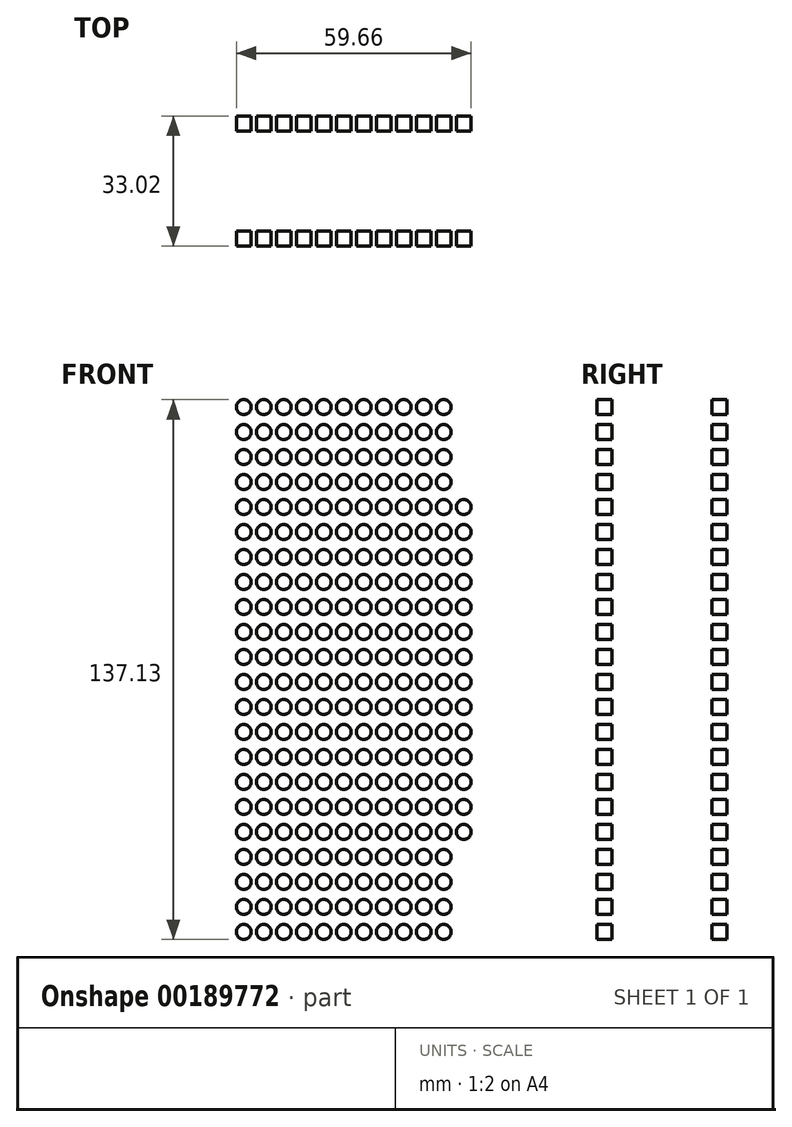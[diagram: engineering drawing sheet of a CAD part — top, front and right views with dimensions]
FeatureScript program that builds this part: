
annotation { "Feature Type Name" : "Feature", "Feature Type Description" : "" }
export const myFeature = defineFeature(function(context is Context, id is Id, definition is map)
    precondition{}
    {
        {
            var Q0;
            Q0=qCreatedBy(makeId("Front.planeOp"),FACE);
            var sketch = newSketch(context, id + "F0", { "sketchPlane" : qUnion([Q0])});
            skLineSegment(sketch, "E0.bottom", {"start": v(-63.5, 0) * mm, "end": v(63.5, 0) * mm});
            skLineSegment(sketch, "E0.top", {"start": v(-63.5, 152.4) * mm, "end": v(63.5, 152.4) * mm});
            skLineSegment(sketch, "E0.left", {"start": v(-63.5, 0) * mm, "end": v(-63.5, 152.4) * mm});
            skLineSegment(sketch, "E0.right", {"start": v(63.5, 0) * mm, "end": v(63.5, 152.4) * mm});
            skSolve(sketch);
        }
        {
            var Q0;
            Q0=makeQuery(id+"F0.imprint","IMPRINT",FACE,{"disambiguationData":[TD([[makeQuery(id+"F0.imprint","IMPRINT",EDGE,{"derivedFrom":sQuery(id+"F0.wireOp",EDGE,"E0.bottom")}),1.0]])]});
            extrude(context, id + "F1", {"entities" : qUnion([Q0]), "depth" : 33.02 * mm});
        }
        {
            var Q0;
            Q0=makeQuery(id+"F1.opExtrude","SWEPT_FACE",FACE,{"disambiguationData":[OSD([sQuery(id+"F0.wireOp",EDGE,"E0.top")])]});
            var sketch = newSketch(context, id + "F2", { "sketchPlane" : qUnion([Q0])});
            skLineSegment(sketch, "E1.bottom", {"start": v(-59.7, -3.81) * mm, "end": v(59.69, -3.81) * mm});
            skLineSegment(sketch, "E1.top", {"start": v(-59.7, -29.21) * mm, "end": v(59.69, -29.21) * mm});
            skLineSegment(sketch, "E1.left", {"start": v(-59.7, -3.81) * mm, "end": v(-59.7, -29.21) * mm});
            skLineSegment(sketch, "E1.right", {"start": v(59.69, -3.81) * mm, "end": v(59.69, -29.21) * mm});
            skSolve(sketch);
        }
        {
            var Q0;
            Q0=makeQuery(id+"F2.imprint","IMPRINT",FACE,{"disambiguationData":[TD([[makeQuery(id+"F2.imprint","IMPRINT",EDGE,{"derivedFrom":sQuery(id+"F2.wireOp",EDGE,"E1.bottom")}),-1.0]])]});
            extrude(context, id + "F3", {"entities" : qUnion([Q0]), "operationType" : NewBodyOperationType.REMOVE, "oppositeDirection" : true, "depth" : 147.32 * mm});
        }
        {
            var Q0;
            Q0=makeQuery(id+"F1.opExtrude","CAP_FACE",FACE,{"disambiguationData":[OSD([sQuery(id+"F0.wireOp",EDGE,"E0.bottom"),sQuery(id+"F0.wireOp",EDGE,"E0.top"),sQuery(id+"F0.wireOp",EDGE,"E0.left"),sQuery(id+"F0.wireOp",EDGE,"E0.right")])],"isStart":false});
            var sketch = newSketch(context, id + "F4", { "sketchPlane" : qUnion([Q0])});
            skCircle(sketch, "E2", {"center": v(0, 7.62) * mm, "radius": 1.89 * mm});
            skCircle(sketch, "E3.0.1.0", {"center": v(0, 13.97) * mm, "radius": 1.89 * mm});
            skCircle(sketch, "E3.0.2.0", {"center": v(0, 20.32) * mm, "radius": 1.89 * mm});
            skCircle(sketch, "E3.0.3.0", {"center": v(0, 26.67) * mm, "radius": 1.89 * mm});
            skCircle(sketch, "E3.0.4.0", {"center": v(0, 33.02) * mm, "radius": 1.89 * mm});
            skCircle(sketch, "E3.0.5.0", {"center": v(0, 39.37) * mm, "radius": 1.89 * mm});
            skCircle(sketch, "E3.0.6.0", {"center": v(0, 45.72) * mm, "radius": 1.89 * mm});
            skCircle(sketch, "E3.0.7.0", {"center": v(0, 52.07) * mm, "radius": 1.89 * mm});
            skCircle(sketch, "E3.0.8.0", {"center": v(0, 58.42) * mm, "radius": 1.89 * mm});
            skCircle(sketch, "E3.0.9.0", {"center": v(0, 64.77) * mm, "radius": 1.89 * mm});
            skCircle(sketch, "E3.0.10.0", {"center": v(0, 71.12) * mm, "radius": 1.89 * mm});
            skCircle(sketch, "E3.0.11.0", {"center": v(0, 77.47) * mm, "radius": 1.89 * mm});
            skCircle(sketch, "E3.0.12.0", {"center": v(0, 83.82) * mm, "radius": 1.89 * mm});
            skCircle(sketch, "E3.0.13.0", {"center": v(0, 90.17) * mm, "radius": 1.89 * mm});
            skCircle(sketch, "E3.0.14.0", {"center": v(0, 96.52) * mm, "radius": 1.89 * mm});
            skCircle(sketch, "E3.0.15.0", {"center": v(0, 102.87) * mm, "radius": 1.89 * mm});
            skCircle(sketch, "E3.0.16.0", {"center": v(0, 109.22) * mm, "radius": 1.89 * mm});
            skCircle(sketch, "E3.0.17.0", {"center": v(0, 115.57) * mm, "radius": 1.89 * mm});
            skCircle(sketch, "E3.1.0.0", {"center": v(5.08, 7.62) * mm, "radius": 1.89 * mm});
            skCircle(sketch, "E3.1.1.0", {"center": v(5.08, 13.97) * mm, "radius": 1.89 * mm});
            skCircle(sketch, "E3.1.2.0", {"center": v(5.08, 20.32) * mm, "radius": 1.89 * mm});
            skCircle(sketch, "E3.1.3.0", {"center": v(5.08, 26.67) * mm, "radius": 1.89 * mm});
            skCircle(sketch, "E3.1.4.0", {"center": v(5.08, 33.02) * mm, "radius": 1.89 * mm});
            skCircle(sketch, "E3.1.5.0", {"center": v(5.08, 39.37) * mm, "radius": 1.89 * mm});
            skCircle(sketch, "E3.1.6.0", {"center": v(5.08, 45.72) * mm, "radius": 1.89 * mm});
            skCircle(sketch, "E3.1.7.0", {"center": v(5.08, 52.07) * mm, "radius": 1.89 * mm});
            skCircle(sketch, "E3.1.8.0", {"center": v(5.08, 58.42) * mm, "radius": 1.89 * mm});
            skCircle(sketch, "E3.1.9.0", {"center": v(5.08, 64.77) * mm, "radius": 1.89 * mm});
            skCircle(sketch, "E3.1.10.0", {"center": v(5.08, 71.12) * mm, "radius": 1.89 * mm});
            skCircle(sketch, "E3.1.11.0", {"center": v(5.08, 77.47) * mm, "radius": 1.89 * mm});
            skCircle(sketch, "E3.1.12.0", {"center": v(5.08, 83.82) * mm, "radius": 1.89 * mm});
            skCircle(sketch, "E3.1.13.0", {"center": v(5.08, 90.17) * mm, "radius": 1.89 * mm});
            skCircle(sketch, "E3.1.14.0", {"center": v(5.08, 96.52) * mm, "radius": 1.89 * mm});
            skCircle(sketch, "E3.1.15.0", {"center": v(5.08, 102.87) * mm, "radius": 1.89 * mm});
            skCircle(sketch, "E3.1.16.0", {"center": v(5.08, 109.22) * mm, "radius": 1.89 * mm});
            skCircle(sketch, "E3.1.17.0", {"center": v(5.08, 115.57) * mm, "radius": 1.89 * mm});
            skCircle(sketch, "E3.2.0.0", {"center": v(10.16, 7.62) * mm, "radius": 1.89 * mm});
            skCircle(sketch, "E3.2.1.0", {"center": v(10.16, 13.97) * mm, "radius": 1.89 * mm});
            skCircle(sketch, "E3.2.2.0", {"center": v(10.16, 20.32) * mm, "radius": 1.89 * mm});
            skCircle(sketch, "E3.2.3.0", {"center": v(10.16, 26.67) * mm, "radius": 1.89 * mm});
            skCircle(sketch, "E3.2.4.0", {"center": v(10.16, 33.02) * mm, "radius": 1.89 * mm});
            skCircle(sketch, "E3.2.5.0", {"center": v(10.16, 39.37) * mm, "radius": 1.89 * mm});
            skCircle(sketch, "E3.2.6.0", {"center": v(10.16, 45.72) * mm, "radius": 1.89 * mm});
            skCircle(sketch, "E3.2.7.0", {"center": v(10.16, 52.07) * mm, "radius": 1.89 * mm});
            skCircle(sketch, "E3.2.8.0", {"center": v(10.16, 58.42) * mm, "radius": 1.89 * mm});
            skCircle(sketch, "E3.2.9.0", {"center": v(10.16, 64.77) * mm, "radius": 1.89 * mm});
            skCircle(sketch, "E3.2.10.0", {"center": v(10.16, 71.12) * mm, "radius": 1.89 * mm});
            skCircle(sketch, "E3.2.11.0", {"center": v(10.16, 77.47) * mm, "radius": 1.89 * mm});
            skCircle(sketch, "E3.2.12.0", {"center": v(10.16, 83.82) * mm, "radius": 1.89 * mm});
            skCircle(sketch, "E3.2.13.0", {"center": v(10.16, 90.17) * mm, "radius": 1.89 * mm});
            skCircle(sketch, "E3.2.14.0", {"center": v(10.16, 96.52) * mm, "radius": 1.89 * mm});
            skCircle(sketch, "E3.2.15.0", {"center": v(10.16, 102.87) * mm, "radius": 1.89 * mm});
            skCircle(sketch, "E3.2.16.0", {"center": v(10.16, 109.22) * mm, "radius": 1.89 * mm});
            skCircle(sketch, "E3.2.17.0", {"center": v(10.16, 115.57) * mm, "radius": 1.89 * mm});
            skCircle(sketch, "E3.3.0.0", {"center": v(15.24, 7.62) * mm, "radius": 1.89 * mm});
            skCircle(sketch, "E3.3.1.0", {"center": v(15.24, 13.97) * mm, "radius": 1.89 * mm});
            skCircle(sketch, "E3.3.2.0", {"center": v(15.24, 20.32) * mm, "radius": 1.89 * mm});
            skCircle(sketch, "E3.3.3.0", {"center": v(15.24, 26.67) * mm, "radius": 1.89 * mm});
            skCircle(sketch, "E3.3.4.0", {"center": v(15.24, 33.02) * mm, "radius": 1.89 * mm});
            skCircle(sketch, "E3.3.5.0", {"center": v(15.24, 39.37) * mm, "radius": 1.89 * mm});
            skCircle(sketch, "E3.3.6.0", {"center": v(15.24, 45.72) * mm, "radius": 1.89 * mm});
            skCircle(sketch, "E3.3.7.0", {"center": v(15.24, 52.07) * mm, "radius": 1.89 * mm});
            skCircle(sketch, "E3.3.8.0", {"center": v(15.24, 58.42) * mm, "radius": 1.89 * mm});
            skCircle(sketch, "E3.3.9.0", {"center": v(15.24, 64.77) * mm, "radius": 1.89 * mm});
            skCircle(sketch, "E3.3.10.0", {"center": v(15.24, 71.12) * mm, "radius": 1.89 * mm});
            skCircle(sketch, "E3.3.11.0", {"center": v(15.24, 77.47) * mm, "radius": 1.89 * mm});
            skCircle(sketch, "E3.3.12.0", {"center": v(15.24, 83.82) * mm, "radius": 1.89 * mm});
            skCircle(sketch, "E3.3.13.0", {"center": v(15.24, 90.17) * mm, "radius": 1.89 * mm});
            skCircle(sketch, "E3.3.14.0", {"center": v(15.24, 96.52) * mm, "radius": 1.89 * mm});
            skCircle(sketch, "E3.3.15.0", {"center": v(15.24, 102.87) * mm, "radius": 1.89 * mm});
            skCircle(sketch, "E3.3.16.0", {"center": v(15.24, 109.22) * mm, "radius": 1.89 * mm});
            skCircle(sketch, "E3.3.17.0", {"center": v(15.24, 115.57) * mm, "radius": 1.89 * mm});
            skCircle(sketch, "E3.4.0.0", {"center": v(20.32, 7.62) * mm, "radius": 1.89 * mm});
            skCircle(sketch, "E3.4.1.0", {"center": v(20.32, 13.97) * mm, "radius": 1.89 * mm});
            skCircle(sketch, "E3.4.2.0", {"center": v(20.32, 20.32) * mm, "radius": 1.89 * mm});
            skCircle(sketch, "E3.4.3.0", {"center": v(20.32, 26.67) * mm, "radius": 1.89 * mm});
            skCircle(sketch, "E3.4.4.0", {"center": v(20.32, 33.02) * mm, "radius": 1.89 * mm});
            skCircle(sketch, "E3.4.5.0", {"center": v(20.32, 39.37) * mm, "radius": 1.89 * mm});
            skCircle(sketch, "E3.4.6.0", {"center": v(20.32, 45.72) * mm, "radius": 1.89 * mm});
            skCircle(sketch, "E3.4.7.0", {"center": v(20.32, 52.07) * mm, "radius": 1.89 * mm});
            skCircle(sketch, "E3.4.8.0", {"center": v(20.32, 58.42) * mm, "radius": 1.89 * mm});
            skCircle(sketch, "E3.4.9.0", {"center": v(20.32, 64.77) * mm, "radius": 1.89 * mm});
            skCircle(sketch, "E3.4.10.0", {"center": v(20.32, 71.12) * mm, "radius": 1.89 * mm});
            skCircle(sketch, "E3.4.11.0", {"center": v(20.32, 77.47) * mm, "radius": 1.89 * mm});
            skCircle(sketch, "E3.4.12.0", {"center": v(20.32, 83.82) * mm, "radius": 1.89 * mm});
            skCircle(sketch, "E3.4.13.0", {"center": v(20.32, 90.17) * mm, "radius": 1.89 * mm});
            skCircle(sketch, "E3.4.14.0", {"center": v(20.32, 96.52) * mm, "radius": 1.89 * mm});
            skCircle(sketch, "E3.4.15.0", {"center": v(20.32, 102.87) * mm, "radius": 1.89 * mm});
            skCircle(sketch, "E3.4.16.0", {"center": v(20.32, 109.22) * mm, "radius": 1.89 * mm});
            skCircle(sketch, "E3.4.17.0", {"center": v(20.32, 115.57) * mm, "radius": 1.89 * mm});
            skCircle(sketch, "E3.5.0.0", {"center": v(25.4, 7.62) * mm, "radius": 1.89 * mm});
            skCircle(sketch, "E3.5.1.0", {"center": v(25.4, 13.97) * mm, "radius": 1.89 * mm});
            skCircle(sketch, "E3.5.2.0", {"center": v(25.4, 20.32) * mm, "radius": 1.89 * mm});
            skCircle(sketch, "E3.5.3.0", {"center": v(25.4, 26.67) * mm, "radius": 1.89 * mm});
            skCircle(sketch, "E3.5.4.0", {"center": v(25.4, 33.02) * mm, "radius": 1.89 * mm});
            skCircle(sketch, "E3.5.5.0", {"center": v(25.4, 39.37) * mm, "radius": 1.89 * mm});
            skCircle(sketch, "E3.5.6.0", {"center": v(25.4, 45.72) * mm, "radius": 1.89 * mm});
            skCircle(sketch, "E3.5.7.0", {"center": v(25.4, 52.07) * mm, "radius": 1.89 * mm});
            skCircle(sketch, "E3.5.8.0", {"center": v(25.4, 58.42) * mm, "radius": 1.89 * mm});
            skCircle(sketch, "E3.5.9.0", {"center": v(25.4, 64.77) * mm, "radius": 1.89 * mm});
            skCircle(sketch, "E3.5.10.0", {"center": v(25.4, 71.12) * mm, "radius": 1.89 * mm});
            skCircle(sketch, "E3.5.11.0", {"center": v(25.4, 77.47) * mm, "radius": 1.89 * mm});
            skCircle(sketch, "E3.5.12.0", {"center": v(25.4, 83.82) * mm, "radius": 1.89 * mm});
            skCircle(sketch, "E3.5.13.0", {"center": v(25.4, 90.17) * mm, "radius": 1.89 * mm});
            skCircle(sketch, "E3.5.14.0", {"center": v(25.4, 96.52) * mm, "radius": 1.89 * mm});
            skCircle(sketch, "E3.5.15.0", {"center": v(25.4, 102.87) * mm, "radius": 1.89 * mm});
            skCircle(sketch, "E3.5.16.0", {"center": v(25.4, 109.22) * mm, "radius": 1.89 * mm});
            skCircle(sketch, "E3.5.17.0", {"center": v(25.4, 115.57) * mm, "radius": 1.89 * mm});
            skCircle(sketch, "E3.6.0.0", {"center": v(30.48, 7.62) * mm, "radius": 1.89 * mm});
            skCircle(sketch, "E3.6.1.0", {"center": v(30.48, 13.97) * mm, "radius": 1.89 * mm});
            skCircle(sketch, "E3.6.2.0", {"center": v(30.48, 20.32) * mm, "radius": 1.89 * mm});
            skCircle(sketch, "E3.6.3.0", {"center": v(30.48, 26.67) * mm, "radius": 1.89 * mm});
            skCircle(sketch, "E3.6.4.0", {"center": v(30.48, 33.02) * mm, "radius": 1.89 * mm});
            skCircle(sketch, "E3.6.5.0", {"center": v(30.48, 39.37) * mm, "radius": 1.89 * mm});
            skCircle(sketch, "E3.6.6.0", {"center": v(30.48, 45.72) * mm, "radius": 1.89 * mm});
            skCircle(sketch, "E3.6.7.0", {"center": v(30.48, 52.07) * mm, "radius": 1.89 * mm});
            skCircle(sketch, "E3.6.8.0", {"center": v(30.48, 58.42) * mm, "radius": 1.89 * mm});
            skCircle(sketch, "E3.6.9.0", {"center": v(30.48, 64.77) * mm, "radius": 1.89 * mm});
            skCircle(sketch, "E3.6.10.0", {"center": v(30.48, 71.12) * mm, "radius": 1.89 * mm});
            skCircle(sketch, "E3.6.11.0", {"center": v(30.48, 77.47) * mm, "radius": 1.89 * mm});
            skCircle(sketch, "E3.6.12.0", {"center": v(30.48, 83.82) * mm, "radius": 1.89 * mm});
            skCircle(sketch, "E3.6.13.0", {"center": v(30.48, 90.17) * mm, "radius": 1.89 * mm});
            skCircle(sketch, "E3.6.14.0", {"center": v(30.48, 96.52) * mm, "radius": 1.89 * mm});
            skCircle(sketch, "E3.6.15.0", {"center": v(30.48, 102.87) * mm, "radius": 1.89 * mm});
            skCircle(sketch, "E3.6.16.0", {"center": v(30.48, 109.22) * mm, "radius": 1.89 * mm});
            skCircle(sketch, "E3.6.17.0", {"center": v(30.48, 115.57) * mm, "radius": 1.89 * mm});
            skCircle(sketch, "E3.7.0.0", {"center": v(35.56, 7.62) * mm, "radius": 1.89 * mm});
            skCircle(sketch, "E3.7.1.0", {"center": v(35.56, 13.97) * mm, "radius": 1.89 * mm});
            skCircle(sketch, "E3.7.2.0", {"center": v(35.56, 20.32) * mm, "radius": 1.89 * mm});
            skCircle(sketch, "E3.7.3.0", {"center": v(35.56, 26.67) * mm, "radius": 1.89 * mm});
            skCircle(sketch, "E3.7.4.0", {"center": v(35.56, 33.02) * mm, "radius": 1.89 * mm});
            skCircle(sketch, "E3.7.5.0", {"center": v(35.56, 39.37) * mm, "radius": 1.89 * mm});
            skCircle(sketch, "E3.7.6.0", {"center": v(35.56, 45.72) * mm, "radius": 1.89 * mm});
            skCircle(sketch, "E3.7.7.0", {"center": v(35.56, 52.07) * mm, "radius": 1.89 * mm});
            skCircle(sketch, "E3.7.8.0", {"center": v(35.56, 58.42) * mm, "radius": 1.89 * mm});
            skCircle(sketch, "E3.7.9.0", {"center": v(35.56, 64.77) * mm, "radius": 1.89 * mm});
            skCircle(sketch, "E3.7.10.0", {"center": v(35.56, 71.12) * mm, "radius": 1.89 * mm});
            skCircle(sketch, "E3.7.11.0", {"center": v(35.56, 77.47) * mm, "radius": 1.89 * mm});
            skCircle(sketch, "E3.7.12.0", {"center": v(35.56, 83.82) * mm, "radius": 1.89 * mm});
            skCircle(sketch, "E3.7.13.0", {"center": v(35.56, 90.17) * mm, "radius": 1.89 * mm});
            skCircle(sketch, "E3.7.14.0", {"center": v(35.56, 96.52) * mm, "radius": 1.89 * mm});
            skCircle(sketch, "E3.7.15.0", {"center": v(35.56, 102.87) * mm, "radius": 1.89 * mm});
            skCircle(sketch, "E3.7.16.0", {"center": v(35.56, 109.22) * mm, "radius": 1.89 * mm});
            skCircle(sketch, "E3.7.17.0", {"center": v(35.56, 115.57) * mm, "radius": 1.89 * mm});
            skLineSegment(sketch, "E3.direction1", {"start": v(0, 7.62) * mm, "end": v(5.08, 7.62) * mm, "construction": true});
            skLineSegment(sketch, "E3.direction2", {"start": v(0, 7.62) * mm, "end": v(0, 13.97) * mm, "construction": true});
            skLineSegment(sketch, "E4.MirrorCS", {"start": v(0, 7.62) * mm, "end": v(-5.08, 7.62) * mm, "construction": true});
            skCircle(sketch, "E5.0.8.0", {"center": v(40.64, 7.62) * mm, "radius": 1.89 * mm});
            skCircle(sketch, "E5.0.8.1", {"center": v(40.64, 13.97) * mm, "radius": 1.89 * mm});
            skCircle(sketch, "E5.0.8.2", {"center": v(40.64, 20.32) * mm, "radius": 1.89 * mm});
            skCircle(sketch, "E5.0.8.3", {"center": v(40.64, 26.67) * mm, "radius": 1.89 * mm});
            skCircle(sketch, "E5.0.8.4", {"center": v(40.64, 33.02) * mm, "radius": 1.89 * mm});
            skCircle(sketch, "E5.0.8.5", {"center": v(40.64, 39.37) * mm, "radius": 1.89 * mm});
            skCircle(sketch, "E5.0.8.6", {"center": v(40.64, 45.72) * mm, "radius": 1.89 * mm});
            skCircle(sketch, "E5.0.8.7", {"center": v(40.64, 52.07) * mm, "radius": 1.89 * mm});
            skCircle(sketch, "E5.0.8.8", {"center": v(40.64, 58.42) * mm, "radius": 1.89 * mm});
            skCircle(sketch, "E5.0.8.9", {"center": v(40.64, 64.77) * mm, "radius": 1.89 * mm});
            skCircle(sketch, "E5.0.8.10", {"center": v(40.64, 71.12) * mm, "radius": 1.89 * mm});
            skCircle(sketch, "E5.0.8.11", {"center": v(40.64, 77.47) * mm, "radius": 1.89 * mm});
            skCircle(sketch, "E5.0.8.12", {"center": v(40.64, 83.82) * mm, "radius": 1.89 * mm});
            skCircle(sketch, "E5.0.8.13", {"center": v(40.64, 90.17) * mm, "radius": 1.89 * mm});
            skCircle(sketch, "E5.0.8.14", {"center": v(40.64, 96.52) * mm, "radius": 1.89 * mm});
            skCircle(sketch, "E5.0.8.15", {"center": v(40.64, 102.87) * mm, "radius": 1.89 * mm});
            skCircle(sketch, "E5.0.8.16", {"center": v(40.64, 109.22) * mm, "radius": 1.89 * mm});
            skCircle(sketch, "E5.0.8.17", {"center": v(40.64, 115.57) * mm, "radius": 1.89 * mm});
            skCircle(sketch, "E5.0.9.0", {"center": v(45.72, 7.62) * mm, "radius": 1.89 * mm});
            skCircle(sketch, "E5.0.9.1", {"center": v(45.72, 13.97) * mm, "radius": 1.89 * mm});
            skCircle(sketch, "E5.0.9.2", {"center": v(45.72, 20.32) * mm, "radius": 1.89 * mm});
            skCircle(sketch, "E5.0.9.3", {"center": v(45.72, 26.67) * mm, "radius": 1.89 * mm});
            skCircle(sketch, "E5.0.9.4", {"center": v(45.72, 33.02) * mm, "radius": 1.89 * mm});
            skCircle(sketch, "E5.0.9.5", {"center": v(45.72, 39.37) * mm, "radius": 1.89 * mm});
            skCircle(sketch, "E5.0.9.6", {"center": v(45.72, 45.72) * mm, "radius": 1.89 * mm});
            skCircle(sketch, "E5.0.9.7", {"center": v(45.72, 52.07) * mm, "radius": 1.89 * mm});
            skCircle(sketch, "E5.0.9.8", {"center": v(45.72, 58.42) * mm, "radius": 1.89 * mm});
            skCircle(sketch, "E5.0.9.9", {"center": v(45.72, 64.77) * mm, "radius": 1.89 * mm});
            skCircle(sketch, "E5.0.9.10", {"center": v(45.72, 71.12) * mm, "radius": 1.89 * mm});
            skCircle(sketch, "E5.0.9.11", {"center": v(45.72, 77.47) * mm, "radius": 1.89 * mm});
            skCircle(sketch, "E5.0.9.12", {"center": v(45.72, 83.82) * mm, "radius": 1.89 * mm});
            skCircle(sketch, "E5.0.9.13", {"center": v(45.72, 90.17) * mm, "radius": 1.89 * mm});
            skCircle(sketch, "E5.0.9.14", {"center": v(45.72, 96.52) * mm, "radius": 1.89 * mm});
            skCircle(sketch, "E5.0.9.15", {"center": v(45.72, 102.87) * mm, "radius": 1.89 * mm});
            skCircle(sketch, "E5.0.9.16", {"center": v(45.72, 109.22) * mm, "radius": 1.89 * mm});
            skCircle(sketch, "E5.0.9.17", {"center": v(45.72, 115.57) * mm, "radius": 1.89 * mm});
            skCircle(sketch, "E5.0.10.0", {"center": v(50.8, 7.62) * mm, "radius": 1.89 * mm});
            skCircle(sketch, "E5.0.10.1", {"center": v(50.8, 13.97) * mm, "radius": 1.89 * mm});
            skCircle(sketch, "E5.0.10.2", {"center": v(50.8, 20.32) * mm, "radius": 1.89 * mm});
            skCircle(sketch, "E5.0.10.3", {"center": v(50.8, 26.67) * mm, "radius": 1.89 * mm});
            skCircle(sketch, "E5.0.10.4", {"center": v(50.8, 33.02) * mm, "radius": 1.89 * mm});
            skCircle(sketch, "E5.0.10.5", {"center": v(50.8, 39.37) * mm, "radius": 1.89 * mm});
            skCircle(sketch, "E5.0.10.6", {"center": v(50.8, 45.72) * mm, "radius": 1.89 * mm});
            skCircle(sketch, "E5.0.10.7", {"center": v(50.8, 52.07) * mm, "radius": 1.89 * mm});
            skCircle(sketch, "E5.0.10.8", {"center": v(50.8, 58.42) * mm, "radius": 1.89 * mm});
            skCircle(sketch, "E5.0.10.9", {"center": v(50.8, 64.77) * mm, "radius": 1.89 * mm});
            skCircle(sketch, "E5.0.10.10", {"center": v(50.8, 71.12) * mm, "radius": 1.89 * mm});
            skCircle(sketch, "E5.0.10.11", {"center": v(50.8, 77.47) * mm, "radius": 1.89 * mm});
            skCircle(sketch, "E5.0.10.12", {"center": v(50.8, 83.82) * mm, "radius": 1.89 * mm});
            skCircle(sketch, "E5.0.10.13", {"center": v(50.8, 90.17) * mm, "radius": 1.89 * mm});
            skCircle(sketch, "E5.0.10.14", {"center": v(50.8, 96.52) * mm, "radius": 1.89 * mm});
            skCircle(sketch, "E5.0.10.15", {"center": v(50.8, 102.87) * mm, "radius": 1.89 * mm});
            skCircle(sketch, "E5.0.10.16", {"center": v(50.8, 109.22) * mm, "radius": 1.89 * mm});
            skCircle(sketch, "E5.0.10.17", {"center": v(50.8, 115.57) * mm, "radius": 1.89 * mm});
            skCircle(sketch, "E5.0.11.0", {"center": v(55.88, 7.62) * mm, "radius": 1.89 * mm});
            skCircle(sketch, "E5.0.11.1", {"center": v(55.88, 13.97) * mm, "radius": 1.89 * mm});
            skCircle(sketch, "E5.0.11.2", {"center": v(55.88, 20.32) * mm, "radius": 1.89 * mm});
            skCircle(sketch, "E5.0.11.3", {"center": v(55.88, 26.67) * mm, "radius": 1.89 * mm});
            skCircle(sketch, "E5.0.11.4", {"center": v(55.88, 33.02) * mm, "radius": 1.89 * mm});
            skCircle(sketch, "E5.0.11.5", {"center": v(55.88, 39.37) * mm, "radius": 1.89 * mm});
            skCircle(sketch, "E5.0.11.6", {"center": v(55.88, 45.72) * mm, "radius": 1.89 * mm});
            skCircle(sketch, "E5.0.11.7", {"center": v(55.88, 52.07) * mm, "radius": 1.89 * mm});
            skCircle(sketch, "E5.0.11.8", {"center": v(55.88, 58.42) * mm, "radius": 1.89 * mm});
            skCircle(sketch, "E5.0.11.9", {"center": v(55.88, 64.77) * mm, "radius": 1.89 * mm});
            skCircle(sketch, "E5.0.11.10", {"center": v(55.88, 71.12) * mm, "radius": 1.89 * mm});
            skCircle(sketch, "E5.0.11.11", {"center": v(55.88, 77.47) * mm, "radius": 1.89 * mm});
            skCircle(sketch, "E5.0.11.12", {"center": v(55.88, 83.82) * mm, "radius": 1.89 * mm});
            skCircle(sketch, "E5.0.11.13", {"center": v(55.88, 90.17) * mm, "radius": 1.89 * mm});
            skCircle(sketch, "E5.0.11.14", {"center": v(55.88, 96.52) * mm, "radius": 1.89 * mm});
            skCircle(sketch, "E5.0.11.15", {"center": v(55.88, 102.87) * mm, "radius": 1.89 * mm});
            skCircle(sketch, "E5.0.11.16", {"center": v(55.88, 109.22) * mm, "radius": 1.89 * mm});
            skCircle(sketch, "E5.0.11.17", {"center": v(55.88, 115.57) * mm, "radius": 1.89 * mm});
            skCircle(sketch, "E6.0.0.18", {"center": v(0, 121.92) * mm, "radius": 1.89 * mm});
            skCircle(sketch, "E6.0.0.19", {"center": v(0, 128.27) * mm, "radius": 1.89 * mm});
            skCircle(sketch, "E6.0.0.20", {"center": v(0, 134.62) * mm, "radius": 1.89 * mm});
            skCircle(sketch, "E6.0.0.21", {"center": v(0, 140.97) * mm, "radius": 1.89 * mm});
            skCircle(sketch, "E6.0.1.18", {"center": v(5.08, 121.92) * mm, "radius": 1.89 * mm});
            skCircle(sketch, "E6.0.1.19", {"center": v(5.08, 128.27) * mm, "radius": 1.89 * mm});
            skCircle(sketch, "E6.0.1.20", {"center": v(5.08, 134.62) * mm, "radius": 1.89 * mm});
            skCircle(sketch, "E6.0.1.21", {"center": v(5.08, 140.97) * mm, "radius": 1.89 * mm});
            skCircle(sketch, "E6.0.2.18", {"center": v(10.16, 121.92) * mm, "radius": 1.89 * mm});
            skCircle(sketch, "E6.0.2.19", {"center": v(10.16, 128.27) * mm, "radius": 1.89 * mm});
            skCircle(sketch, "E6.0.2.20", {"center": v(10.16, 134.62) * mm, "radius": 1.89 * mm});
            skCircle(sketch, "E6.0.2.21", {"center": v(10.16, 140.97) * mm, "radius": 1.89 * mm});
            skCircle(sketch, "E6.0.3.18", {"center": v(15.24, 121.92) * mm, "radius": 1.89 * mm});
            skCircle(sketch, "E6.0.3.19", {"center": v(15.24, 128.27) * mm, "radius": 1.89 * mm});
            skCircle(sketch, "E6.0.3.20", {"center": v(15.24, 134.62) * mm, "radius": 1.89 * mm});
            skCircle(sketch, "E6.0.3.21", {"center": v(15.24, 140.97) * mm, "radius": 1.89 * mm});
            skCircle(sketch, "E6.0.4.18", {"center": v(20.32, 121.92) * mm, "radius": 1.89 * mm});
            skCircle(sketch, "E6.0.4.19", {"center": v(20.32, 128.27) * mm, "radius": 1.89 * mm});
            skCircle(sketch, "E6.0.4.20", {"center": v(20.32, 134.62) * mm, "radius": 1.89 * mm});
            skCircle(sketch, "E6.0.4.21", {"center": v(20.32, 140.97) * mm, "radius": 1.89 * mm});
            skCircle(sketch, "E6.0.5.18", {"center": v(25.4, 121.92) * mm, "radius": 1.89 * mm});
            skCircle(sketch, "E6.0.5.19", {"center": v(25.4, 128.27) * mm, "radius": 1.89 * mm});
            skCircle(sketch, "E6.0.5.20", {"center": v(25.4, 134.62) * mm, "radius": 1.89 * mm});
            skCircle(sketch, "E6.0.5.21", {"center": v(25.4, 140.97) * mm, "radius": 1.89 * mm});
            skCircle(sketch, "E6.0.6.18", {"center": v(30.48, 121.92) * mm, "radius": 1.89 * mm});
            skCircle(sketch, "E6.0.6.19", {"center": v(30.48, 128.27) * mm, "radius": 1.89 * mm});
            skCircle(sketch, "E6.0.6.20", {"center": v(30.48, 134.62) * mm, "radius": 1.89 * mm});
            skCircle(sketch, "E6.0.6.21", {"center": v(30.48, 140.97) * mm, "radius": 1.89 * mm});
            skCircle(sketch, "E6.0.7.18", {"center": v(35.56, 121.92) * mm, "radius": 1.89 * mm});
            skCircle(sketch, "E6.0.7.19", {"center": v(35.56, 128.27) * mm, "radius": 1.89 * mm});
            skCircle(sketch, "E6.0.7.20", {"center": v(35.56, 134.62) * mm, "radius": 1.89 * mm});
            skCircle(sketch, "E6.0.7.21", {"center": v(35.56, 140.97) * mm, "radius": 1.89 * mm});
            skCircle(sketch, "E6.0.8.18", {"center": v(40.64, 121.92) * mm, "radius": 1.89 * mm});
            skCircle(sketch, "E6.0.8.19", {"center": v(40.64, 128.27) * mm, "radius": 1.89 * mm});
            skCircle(sketch, "E6.0.8.20", {"center": v(40.64, 134.62) * mm, "radius": 1.89 * mm});
            skCircle(sketch, "E6.0.8.21", {"center": v(40.64, 140.97) * mm, "radius": 1.89 * mm});
            skCircle(sketch, "E6.0.9.18", {"center": v(45.72, 121.92) * mm, "radius": 1.89 * mm});
            skCircle(sketch, "E6.0.9.19", {"center": v(45.72, 128.27) * mm, "radius": 1.89 * mm});
            skCircle(sketch, "E6.0.9.20", {"center": v(45.72, 134.62) * mm, "radius": 1.89 * mm});
            skCircle(sketch, "E6.0.9.21", {"center": v(45.72, 140.97) * mm, "radius": 1.89 * mm});
            skCircle(sketch, "E6.0.10.18", {"center": v(50.8, 121.92) * mm, "radius": 1.89 * mm});
            skCircle(sketch, "E6.0.10.19", {"center": v(50.8, 128.27) * mm, "radius": 1.89 * mm});
            skCircle(sketch, "E6.0.10.20", {"center": v(50.8, 134.62) * mm, "radius": 1.89 * mm});
            skCircle(sketch, "E6.0.10.21", {"center": v(50.8, 140.97) * mm, "radius": 1.89 * mm});
            skCircle(sketch, "E6.0.11.18", {"center": v(55.88, 121.92) * mm, "radius": 1.89 * mm});
            skCircle(sketch, "E6.0.11.19", {"center": v(55.88, 128.27) * mm, "radius": 1.89 * mm});
            skCircle(sketch, "E6.0.11.20", {"center": v(55.88, 134.62) * mm, "radius": 1.89 * mm});
            skCircle(sketch, "E6.0.11.21", {"center": v(55.88, 140.97) * mm, "radius": 1.89 * mm});
            skCircle(sketch, "E7.MirrorC", {"center": v(-5.08, 7.62) * mm, "radius": 1.89 * mm});
            skCircle(sketch, "E8.MirrorC", {"center": v(-5.08, 33.02) * mm, "radius": 1.89 * mm});
            skCircle(sketch, "E9.MirrorC", {"center": v(-15.24, 7.62) * mm, "radius": 1.89 * mm});
            skCircle(sketch, "E10.MirrorC", {"center": v(-35.56, 83.82) * mm, "radius": 1.89 * mm});
            skCircle(sketch, "E11.MirrorC", {"center": v(-5.08, 58.42) * mm, "radius": 1.89 * mm});
            skCircle(sketch, "E12.MirrorC", {"center": v(-10.16, 20.32) * mm, "radius": 1.89 * mm});
            skCircle(sketch, "E13.MirrorC", {"center": v(-10.16, 13.97) * mm, "radius": 1.89 * mm});
            skCircle(sketch, "E14.MirrorC", {"center": v(-40.64, 64.77) * mm, "radius": 1.89 * mm});
            skCircle(sketch, "E15.MirrorC", {"center": v(-5.08, 20.32) * mm, "radius": 1.89 * mm});
            skCircle(sketch, "E16.MirrorC", {"center": v(-10.16, 7.62) * mm, "radius": 1.89 * mm});
            skCircle(sketch, "E17.MirrorC", {"center": v(-5.08, 52.07) * mm, "radius": 1.89 * mm});
            skCircle(sketch, "E18.MirrorC", {"center": v(-5.08, 13.97) * mm, "radius": 1.89 * mm});
            skCircle(sketch, "E19.MirrorC", {"center": v(-30.48, 83.82) * mm, "radius": 1.89 * mm});
            skCircle(sketch, "E20.MirrorC", {"center": v(-15.24, 20.32) * mm, "radius": 1.89 * mm});
            skCircle(sketch, "E21.MirrorC", {"center": v(-20.32, 7.62) * mm, "radius": 1.89 * mm});
            skCircle(sketch, "E22.MirrorC", {"center": v(-50.8, 39.37) * mm, "radius": 1.89 * mm});
            skCircle(sketch, "E23.MirrorC", {"center": v(-45.72, 52.07) * mm, "radius": 1.89 * mm});
            skCircle(sketch, "E24.MirrorC", {"center": v(-40.64, 128.27) * mm, "radius": 1.89 * mm});
            skCircle(sketch, "E25.MirrorC", {"center": v(-40.64, 20.32) * mm, "radius": 1.89 * mm});
            skCircle(sketch, "E26.MirrorC", {"center": v(-20.32, 128.27) * mm, "radius": 1.89 * mm});
            skCircle(sketch, "E27.MirrorC", {"center": v(-20.32, 109.22) * mm, "radius": 1.89 * mm});
            skCircle(sketch, "E28.MirrorC", {"center": v(-25.4, 96.52) * mm, "radius": 1.89 * mm});
            skCircle(sketch, "E29.MirrorC", {"center": v(-5.08, 83.82) * mm, "radius": 1.89 * mm});
            skCircle(sketch, "E30.MirrorC", {"center": v(-40.64, 90.17) * mm, "radius": 1.89 * mm});
            skCircle(sketch, "E31.MirrorC", {"center": v(-5.08, 64.77) * mm, "radius": 1.89 * mm});
            skCircle(sketch, "E32.MirrorC", {"center": v(-20.32, 134.62) * mm, "radius": 1.89 * mm});
            skCircle(sketch, "E33.MirrorC", {"center": v(-40.64, 134.62) * mm, "radius": 1.89 * mm});
            skCircle(sketch, "E34.MirrorC", {"center": v(-5.08, 71.12) * mm, "radius": 1.89 * mm});
            skCircle(sketch, "E35.MirrorC", {"center": v(-5.08, 45.72) * mm, "radius": 1.89 * mm});
            skCircle(sketch, "E36.MirrorC", {"center": v(-40.64, 77.47) * mm, "radius": 1.89 * mm});
            skCircle(sketch, "E37.MirrorC", {"center": v(-10.16, 33.02) * mm, "radius": 1.89 * mm});
            skCircle(sketch, "E38.MirrorC", {"center": v(-40.64, 96.52) * mm, "radius": 1.89 * mm});
            skCircle(sketch, "E39.MirrorC", {"center": v(-40.64, 71.12) * mm, "radius": 1.89 * mm});
            skCircle(sketch, "E40.MirrorC", {"center": v(-45.72, 58.42) * mm, "radius": 1.89 * mm});
            skCircle(sketch, "E41.MirrorC", {"center": v(-50.8, 45.72) * mm, "radius": 1.89 * mm});
            skCircle(sketch, "E42.MirrorC", {"center": v(-25.4, 121.92) * mm, "radius": 1.89 * mm});
            skCircle(sketch, "E43.MirrorC", {"center": v(-5.08, 121.92) * mm, "radius": 1.89 * mm});
            skCircle(sketch, "E44.MirrorC", {"center": v(-40.64, 140.97) * mm, "radius": 1.89 * mm});
            skCircle(sketch, "E45.MirrorC", {"center": v(-20.32, 140.97) * mm, "radius": 1.89 * mm});
            skCircle(sketch, "E46.MirrorC", {"center": v(-40.64, 102.87) * mm, "radius": 1.89 * mm});
            skCircle(sketch, "E47.MirrorC", {"center": v(-45.72, 121.92) * mm, "radius": 1.89 * mm});
            skCircle(sketch, "E48.MirrorC", {"center": v(-40.64, 109.22) * mm, "radius": 1.89 * mm});
            skCircle(sketch, "E49.MirrorC", {"center": v(-40.64, 7.62) * mm, "radius": 1.89 * mm});
            skCircle(sketch, "E50.MirrorC", {"center": v(-30.48, 77.47) * mm, "radius": 1.89 * mm});
            skCircle(sketch, "E51.MirrorC", {"center": v(-40.64, 45.72) * mm, "radius": 1.89 * mm});
            skCircle(sketch, "E52.MirrorC", {"center": v(-15.24, 13.97) * mm, "radius": 1.89 * mm});
            skCircle(sketch, "E53.MirrorC", {"center": v(-15.24, 115.57) * mm, "radius": 1.89 * mm});
            skCircle(sketch, "E54.MirrorC", {"center": v(-45.72, 45.72) * mm, "radius": 1.89 * mm});
            skCircle(sketch, "E55.MirrorC", {"center": v(-20.32, 102.87) * mm, "radius": 1.89 * mm});
            skCircle(sketch, "E56.MirrorC", {"center": v(-25.4, 90.17) * mm, "radius": 1.89 * mm});
            skCircle(sketch, "E57.MirrorC", {"center": v(-10.16, 26.67) * mm, "radius": 1.89 * mm});
            skCircle(sketch, "E58.MirrorC", {"center": v(-5.08, 39.37) * mm, "radius": 1.89 * mm});
            skCircle(sketch, "E59.MirrorC", {"center": v(-40.64, 115.57) * mm, "radius": 1.89 * mm});
            skCircle(sketch, "E60.MirrorC", {"center": v(-40.64, 13.97) * mm, "radius": 1.89 * mm});
            skCircle(sketch, "E61.MirrorC", {"center": v(-5.08, 77.47) * mm, "radius": 1.89 * mm});
            skCircle(sketch, "E62.MirrorC", {"center": v(-35.56, 77.47) * mm, "radius": 1.89 * mm});
            skCircle(sketch, "E63.MirrorC", {"center": v(-40.64, 83.82) * mm, "radius": 1.89 * mm});
            skCircle(sketch, "E64.MirrorC", {"center": v(-25.4, 77.47) * mm, "radius": 1.89 * mm});
            skCircle(sketch, "E65.MirrorC", {"center": v(-15.24, 109.22) * mm, "radius": 1.89 * mm});
            skCircle(sketch, "E66.MirrorC", {"center": v(-55.88, 96.52) * mm, "radius": 1.89 * mm});
            skCircle(sketch, "E67.MirrorC", {"center": v(-15.24, 128.27) * mm, "radius": 1.89 * mm});
            skCircle(sketch, "E68.MirrorC", {"center": v(-50.8, 13.97) * mm, "radius": 1.89 * mm});
            skCircle(sketch, "E69.MirrorC", {"center": v(-10.16, 45.72) * mm, "radius": 1.89 * mm});
            skCircle(sketch, "E70.MirrorC", {"center": v(-15.24, 33.02) * mm, "radius": 1.89 * mm});
            skCircle(sketch, "E71.MirrorC", {"center": v(-15.24, 121.92) * mm, "radius": 1.89 * mm});
            skCircle(sketch, "E72.MirrorC", {"center": v(-25.4, 83.82) * mm, "radius": 1.89 * mm});
            skCircle(sketch, "E73.MirrorC", {"center": v(-35.56, 121.92) * mm, "radius": 1.89 * mm});
            skCircle(sketch, "E74.MirrorC", {"center": v(-30.48, 64.77) * mm, "radius": 1.89 * mm});
            skCircle(sketch, "E75.MirrorC", {"center": v(-25.4, 7.62) * mm, "radius": 1.89 * mm});
            skCircle(sketch, "E76.MirrorC", {"center": v(-20.32, 96.52) * mm, "radius": 1.89 * mm});
            skCircle(sketch, "E77.MirrorC", {"center": v(-55.88, 128.27) * mm, "radius": 1.89 * mm});
            skCircle(sketch, "E78.MirrorC", {"center": v(-50.8, 7.62) * mm, "radius": 1.89 * mm});
            skCircle(sketch, "E79.MirrorC", {"center": v(-40.64, 33.02) * mm, "radius": 1.89 * mm});
            skCircle(sketch, "E80.MirrorC", {"center": v(-40.64, 39.37) * mm, "radius": 1.89 * mm});
            skCircle(sketch, "E81.MirrorC", {"center": v(-35.56, 128.27) * mm, "radius": 1.89 * mm});
            skCircle(sketch, "E82.MirrorC", {"center": v(-35.56, 52.07) * mm, "radius": 1.89 * mm});
            skCircle(sketch, "E83.MirrorC", {"center": v(-55.88, 102.87) * mm, "radius": 1.89 * mm});
            skCircle(sketch, "E84.MirrorC", {"center": v(-50.8, 109.22) * mm, "radius": 1.89 * mm});
            skCircle(sketch, "E85.MirrorC", {"center": v(-45.72, 20.32) * mm, "radius": 1.89 * mm});
            skCircle(sketch, "E86.MirrorC", {"center": v(-45.72, 26.67) * mm, "radius": 1.89 * mm});
            skCircle(sketch, "E87.MirrorC", {"center": v(-35.56, 58.42) * mm, "radius": 1.89 * mm});
            skCircle(sketch, "E88.MirrorC", {"center": v(-20.32, 20.32) * mm, "radius": 1.89 * mm});
            skCircle(sketch, "E89.MirrorC", {"center": v(-15.24, 102.87) * mm, "radius": 1.89 * mm});
            skCircle(sketch, "E90.MirrorC", {"center": v(-50.8, 115.57) * mm, "radius": 1.89 * mm});
            skCircle(sketch, "E91.MirrorC", {"center": v(-30.48, 96.52) * mm, "radius": 1.89 * mm});
            skCircle(sketch, "E92.MirrorC", {"center": v(-25.4, 109.22) * mm, "radius": 1.89 * mm});
            skCircle(sketch, "E93.MirrorC", {"center": v(-10.16, 115.57) * mm, "radius": 1.89 * mm});
            skCircle(sketch, "E94.MirrorC", {"center": v(-30.48, 71.12) * mm, "radius": 1.89 * mm});
            skCircle(sketch, "E95.MirrorC", {"center": v(-20.32, 90.17) * mm, "radius": 1.89 * mm});
            skCircle(sketch, "E96.MirrorC", {"center": v(-5.08, 26.67) * mm, "radius": 1.89 * mm});
            skCircle(sketch, "E97.MirrorC", {"center": v(-20.32, 121.92) * mm, "radius": 1.89 * mm});
            skCircle(sketch, "E98.MirrorC", {"center": v(-55.88, 121.92) * mm, "radius": 1.89 * mm});
            skCircle(sketch, "E99.MirrorC", {"center": v(-40.64, 26.67) * mm, "radius": 1.89 * mm});
            skCircle(sketch, "E100.MirrorC", {"center": v(-45.72, 13.97) * mm, "radius": 1.89 * mm});
            skCircle(sketch, "E101.MirrorC", {"center": v(-45.72, 115.57) * mm, "radius": 1.89 * mm});
            skCircle(sketch, "E102.MirrorC", {"center": v(-20.32, 83.82) * mm, "radius": 1.89 * mm});
            skCircle(sketch, "E103.MirrorC", {"center": v(-25.4, 71.12) * mm, "radius": 1.89 * mm});
            skCircle(sketch, "E104.MirrorC", {"center": v(-30.48, 58.42) * mm, "radius": 1.89 * mm});
            skCircle(sketch, "E105.MirrorC", {"center": v(-35.56, 45.72) * mm, "radius": 1.89 * mm});
            skCircle(sketch, "E106.MirrorC", {"center": v(-10.16, 109.22) * mm, "radius": 1.89 * mm});
            skCircle(sketch, "E107.MirrorC", {"center": v(-15.24, 96.52) * mm, "radius": 1.89 * mm});
            skCircle(sketch, "E108.MirrorC", {"center": v(-50.8, 140.97) * mm, "radius": 1.89 * mm});
            skCircle(sketch, "E109.MirrorC", {"center": v(-50.8, 102.87) * mm, "radius": 1.89 * mm});
            skCircle(sketch, "E110.MirrorC", {"center": v(-55.88, 90.17) * mm, "radius": 1.89 * mm});
            skCircle(sketch, "E111.MirrorC", {"center": v(-10.16, 140.97) * mm, "radius": 1.89 * mm});
            skCircle(sketch, "E112.MirrorC", {"center": v(-30.48, 140.97) * mm, "radius": 1.89 * mm});
            skCircle(sketch, "E113.MirrorC", {"center": v(-15.24, 26.67) * mm, "radius": 1.89 * mm});
            skCircle(sketch, "E114.MirrorC", {"center": v(-20.32, 13.97) * mm, "radius": 1.89 * mm});
            skCircle(sketch, "E115.MirrorC", {"center": v(-20.32, 115.57) * mm, "radius": 1.89 * mm});
            skCircle(sketch, "E116.MirrorC", {"center": v(-25.4, 102.87) * mm, "radius": 1.89 * mm});
            skCircle(sketch, "E117.MirrorC", {"center": v(-10.16, 39.37) * mm, "radius": 1.89 * mm});
            skCircle(sketch, "E118.MirrorC", {"center": v(-20.32, 77.47) * mm, "radius": 1.89 * mm});
            skCircle(sketch, "E119.MirrorC", {"center": v(-25.4, 64.77) * mm, "radius": 1.89 * mm});
            skCircle(sketch, "E120.MirrorC", {"center": v(-30.48, 52.07) * mm, "radius": 1.89 * mm});
            skCircle(sketch, "E121.MirrorC", {"center": v(-35.56, 39.37) * mm, "radius": 1.89 * mm});
            skCircle(sketch, "E122.MirrorC", {"center": v(-5.08, 115.57) * mm, "radius": 1.89 * mm});
            skCircle(sketch, "E123.MirrorC", {"center": v(-10.16, 102.87) * mm, "radius": 1.89 * mm});
            skCircle(sketch, "E124.MirrorC", {"center": v(-15.24, 90.17) * mm, "radius": 1.89 * mm});
            skCircle(sketch, "E125.MirrorC", {"center": v(-40.64, 58.42) * mm, "radius": 1.89 * mm});
            skCircle(sketch, "E126.MirrorC", {"center": v(-15.24, 140.97) * mm, "radius": 1.89 * mm});
            skCircle(sketch, "E127.MirrorC", {"center": v(-35.56, 140.97) * mm, "radius": 1.89 * mm});
            skCircle(sketch, "E128.MirrorC", {"center": v(-55.88, 140.97) * mm, "radius": 1.89 * mm});
            skCircle(sketch, "E129.MirrorC", {"center": v(-45.72, 39.37) * mm, "radius": 1.89 * mm});
            skCircle(sketch, "E130.MirrorC", {"center": v(-50.8, 26.67) * mm, "radius": 1.89 * mm});
            skCircle(sketch, "E131.MirrorC", {"center": v(-55.88, 13.97) * mm, "radius": 1.89 * mm});
            skCircle(sketch, "E132.MirrorC", {"center": v(-55.88, 115.57) * mm, "radius": 1.89 * mm});
            skCircle(sketch, "E133.MirrorC", {"center": v(-35.56, 71.12) * mm, "radius": 1.89 * mm});
            skCircle(sketch, "E134.MirrorC", {"center": v(-40.64, 52.07) * mm, "radius": 1.89 * mm});
            skCircle(sketch, "E135.MirrorC", {"center": v(-55.88, 26.67) * mm, "radius": 1.89 * mm});
            skCircle(sketch, "E136.MirrorC", {"center": v(-50.8, 134.62) * mm, "radius": 1.89 * mm});
            skCircle(sketch, "E137.MirrorC", {"center": v(-50.8, 96.52) * mm, "radius": 1.89 * mm});
            skCircle(sketch, "E138.MirrorC", {"center": v(-55.88, 83.82) * mm, "radius": 1.89 * mm});
            skCircle(sketch, "E139.MirrorC", {"center": v(-10.16, 134.62) * mm, "radius": 1.89 * mm});
            skCircle(sketch, "E140.MirrorC", {"center": v(-30.48, 134.62) * mm, "radius": 1.89 * mm});
            skCircle(sketch, "E141.MirrorC", {"center": v(-45.72, 7.62) * mm, "radius": 1.89 * mm});
            skCircle(sketch, "E142.MirrorC", {"center": v(-45.72, 109.22) * mm, "radius": 1.89 * mm});
            skCircle(sketch, "E143.MirrorC", {"center": v(-15.24, 58.42) * mm, "radius": 1.89 * mm});
            skCircle(sketch, "E144.MirrorC", {"center": v(-45.72, 128.27) * mm, "radius": 1.89 * mm});
            skCircle(sketch, "E145.MirrorC", {"center": v(-10.16, 71.12) * mm, "radius": 1.89 * mm});
            skCircle(sketch, "E146.MirrorC", {"center": v(-25.4, 33.02) * mm, "radius": 1.89 * mm});
            skCircle(sketch, "E147.MirrorC", {"center": v(-30.48, 20.32) * mm, "radius": 1.89 * mm});
            skCircle(sketch, "E148.MirrorC", {"center": v(-35.56, 7.62) * mm, "radius": 1.89 * mm});
            skCircle(sketch, "E149.MirrorC", {"center": v(-20.32, 45.72) * mm, "radius": 1.89 * mm});
            skCircle(sketch, "E150.MirrorC", {"center": v(-45.72, 77.47) * mm, "radius": 1.89 * mm});
            skCircle(sketch, "E151.MirrorC", {"center": v(-10.16, 52.07) * mm, "radius": 1.89 * mm});
            skCircle(sketch, "E152.MirrorC", {"center": v(-25.4, 115.57) * mm, "radius": 1.89 * mm});
            skCircle(sketch, "E153.MirrorC", {"center": v(-25.4, 13.97) * mm, "radius": 1.89 * mm});
            skCircle(sketch, "E154.MirrorC", {"center": v(-50.8, 90.17) * mm, "radius": 1.89 * mm});
            skCircle(sketch, "E155.MirrorC", {"center": v(-20.32, 26.67) * mm, "radius": 1.89 * mm});
            skCircle(sketch, "E156.MirrorC", {"center": v(-35.56, 109.22) * mm, "radius": 1.89 * mm});
            skCircle(sketch, "E157.MirrorC", {"center": v(-25.4, 128.27) * mm, "radius": 1.89 * mm});
            skCircle(sketch, "E158.MirrorC", {"center": v(-55.88, 52.07) * mm, "radius": 1.89 * mm});
            skCircle(sketch, "E159.MirrorC", {"center": v(-50.8, 64.77) * mm, "radius": 1.89 * mm});
            skCircle(sketch, "E160.MirrorC", {"center": v(-5.08, 128.27) * mm, "radius": 1.89 * mm});
            skCircle(sketch, "E161.MirrorC", {"center": v(-10.16, 58.42) * mm, "radius": 1.89 * mm});
            skCircle(sketch, "E162.MirrorC", {"center": v(-30.48, 7.62) * mm, "radius": 1.89 * mm});
            skCircle(sketch, "E163.MirrorC", {"center": v(-15.24, 45.72) * mm, "radius": 1.89 * mm});
            skCircle(sketch, "E164.MirrorC", {"center": v(-25.4, 20.32) * mm, "radius": 1.89 * mm});
            skCircle(sketch, "E165.MirrorC", {"center": v(-20.32, 33.02) * mm, "radius": 1.89 * mm});
            skCircle(sketch, "E166.MirrorC", {"center": v(-15.24, 64.77) * mm, "radius": 1.89 * mm});
            skCircle(sketch, "E167.MirrorC", {"center": v(-10.16, 77.47) * mm, "radius": 1.89 * mm});
            skCircle(sketch, "E168.MirrorC", {"center": v(-5.08, 90.17) * mm, "radius": 1.89 * mm});
            skCircle(sketch, "E169.MirrorC", {"center": v(-35.56, 13.97) * mm, "radius": 1.89 * mm});
            skCircle(sketch, "E170.MirrorC", {"center": v(-30.48, 26.67) * mm, "radius": 1.89 * mm});
            skCircle(sketch, "E171.MirrorC", {"center": v(-25.4, 39.37) * mm, "radius": 1.89 * mm});
            skCircle(sketch, "E172.MirrorC", {"center": v(-20.32, 52.07) * mm, "radius": 1.89 * mm});
            skCircle(sketch, "E173.MirrorC", {"center": v(-45.72, 83.82) * mm, "radius": 1.89 * mm});
            skCircle(sketch, "E174.MirrorC", {"center": v(-15.24, 39.37) * mm, "radius": 1.89 * mm});
            skCircle(sketch, "E175.MirrorC", {"center": v(-30.48, 102.87) * mm, "radius": 1.89 * mm});
            skCircle(sketch, "E176.MirrorC", {"center": v(-35.56, 115.57) * mm, "radius": 1.89 * mm});
            skCircle(sketch, "E177.MirrorC", {"center": v(-25.4, 134.62) * mm, "radius": 1.89 * mm});
            skCircle(sketch, "E178.MirrorC", {"center": v(-5.08, 134.62) * mm, "radius": 1.89 * mm});
            skCircle(sketch, "E179.MirrorC", {"center": v(-55.88, 58.42) * mm, "radius": 1.89 * mm});
            skCircle(sketch, "E180.MirrorC", {"center": v(-50.8, 71.12) * mm, "radius": 1.89 * mm});
            skCircle(sketch, "E181.MirrorC", {"center": v(-45.72, 134.62) * mm, "radius": 1.89 * mm});
            skCircle(sketch, "E182.MirrorC", {"center": v(-15.24, 71.12) * mm, "radius": 1.89 * mm});
            skCircle(sketch, "E183.MirrorC", {"center": v(-10.16, 83.82) * mm, "radius": 1.89 * mm});
            skCircle(sketch, "E184.MirrorC", {"center": v(-5.08, 96.52) * mm, "radius": 1.89 * mm});
            skCircle(sketch, "E185.MirrorC", {"center": v(-35.56, 20.32) * mm, "radius": 1.89 * mm});
            skCircle(sketch, "E186.MirrorC", {"center": v(-30.48, 33.02) * mm, "radius": 1.89 * mm});
            skCircle(sketch, "E187.MirrorC", {"center": v(-35.56, 96.52) * mm, "radius": 1.89 * mm});
            skCircle(sketch, "E188.MirrorC", {"center": v(-25.4, 45.72) * mm, "radius": 1.89 * mm});
            skCircle(sketch, "E189.MirrorC", {"center": v(-20.32, 58.42) * mm, "radius": 1.89 * mm});
            skCircle(sketch, "E190.MirrorC", {"center": v(-30.48, 109.22) * mm, "radius": 1.89 * mm});
            skCircle(sketch, "E191.MirrorC", {"center": v(-55.88, 39.37) * mm, "radius": 1.89 * mm});
            skCircle(sketch, "E192.MirrorC", {"center": v(-45.72, 64.77) * mm, "radius": 1.89 * mm});
            skCircle(sketch, "E193.MirrorC", {"center": v(-50.8, 52.07) * mm, "radius": 1.89 * mm});
            skCircle(sketch, "E194.MirrorC", {"center": v(-35.56, 90.17) * mm, "radius": 1.89 * mm});
            skCircle(sketch, "E195.MirrorC", {"center": v(-55.88, 33.02) * mm, "radius": 1.89 * mm});
            skCircle(sketch, "E196.MirrorC", {"center": v(-55.88, 45.72) * mm, "radius": 1.89 * mm});
            skCircle(sketch, "E197.MirrorC", {"center": v(-50.8, 58.42) * mm, "radius": 1.89 * mm});
            skCircle(sketch, "E198.MirrorC", {"center": v(-45.72, 90.17) * mm, "radius": 1.89 * mm});
            skCircle(sketch, "E199.MirrorC", {"center": v(-25.4, 140.97) * mm, "radius": 1.89 * mm});
            skCircle(sketch, "E200.MirrorC", {"center": v(-5.08, 140.97) * mm, "radius": 1.89 * mm});
            skCircle(sketch, "E201.MirrorC", {"center": v(-50.8, 77.47) * mm, "radius": 1.89 * mm});
            skCircle(sketch, "E202.MirrorC", {"center": v(-55.88, 64.77) * mm, "radius": 1.89 * mm});
            skCircle(sketch, "E203.MirrorC", {"center": v(-45.72, 140.97) * mm, "radius": 1.89 * mm});
            skCircle(sketch, "E204.MirrorC", {"center": v(-30.48, 90.17) * mm, "radius": 1.89 * mm});
            skCircle(sketch, "E205.MirrorC", {"center": v(-55.88, 20.32) * mm, "radius": 1.89 * mm});
            skCircle(sketch, "E206.MirrorC", {"center": v(-15.24, 77.47) * mm, "radius": 1.89 * mm});
            skCircle(sketch, "E207.MirrorC", {"center": v(-10.16, 90.17) * mm, "radius": 1.89 * mm});
            skCircle(sketch, "E208.MirrorC", {"center": v(-5.08, 102.87) * mm, "radius": 1.89 * mm});
            skCircle(sketch, "E209.MirrorC", {"center": v(-35.56, 26.67) * mm, "radius": 1.89 * mm});
            skCircle(sketch, "E210.MirrorC", {"center": v(-30.48, 39.37) * mm, "radius": 1.89 * mm});
            skCircle(sketch, "E211.MirrorC", {"center": v(-25.4, 52.07) * mm, "radius": 1.89 * mm});
            skCircle(sketch, "E212.MirrorC", {"center": v(-20.32, 64.77) * mm, "radius": 1.89 * mm});
            skCircle(sketch, "E213.MirrorC", {"center": v(-45.72, 96.52) * mm, "radius": 1.89 * mm});
            skCircle(sketch, "E214.MirrorC", {"center": v(-15.24, 134.62) * mm, "radius": 1.89 * mm});
            skCircle(sketch, "E215.MirrorC", {"center": v(-10.16, 121.92) * mm, "radius": 1.89 * mm});
            skCircle(sketch, "E216.MirrorC", {"center": v(-30.48, 121.92) * mm, "radius": 1.89 * mm});
            skCircle(sketch, "E217.MirrorC", {"center": v(-55.88, 71.12) * mm, "radius": 1.89 * mm});
            skCircle(sketch, "E218.MirrorC", {"center": v(-50.8, 83.82) * mm, "radius": 1.89 * mm});
            skCircle(sketch, "E219.MirrorC", {"center": v(-50.8, 121.92) * mm, "radius": 1.89 * mm});
            skCircle(sketch, "E220.MirrorC", {"center": v(-50.8, 33.02) * mm, "radius": 1.89 * mm});
            skCircle(sketch, "E221.MirrorC", {"center": v(-55.88, 134.62) * mm, "radius": 1.89 * mm});
            skCircle(sketch, "E222.MirrorC", {"center": v(-35.56, 134.62) * mm, "radius": 1.89 * mm});
            skCircle(sketch, "E223.MirrorC", {"center": v(-50.8, 20.32) * mm, "radius": 1.89 * mm});
            skCircle(sketch, "E224.MirrorC", {"center": v(-45.72, 33.02) * mm, "radius": 1.89 * mm});
            skCircle(sketch, "E225.MirrorC", {"center": v(-55.88, 109.22) * mm, "radius": 1.89 * mm});
            skCircle(sketch, "E226.MirrorC", {"center": v(-55.88, 7.62) * mm, "radius": 1.89 * mm});
            skCircle(sketch, "E227.MirrorC", {"center": v(-35.56, 64.77) * mm, "radius": 1.89 * mm});
            skCircle(sketch, "E228.MirrorC", {"center": v(-50.8, 128.27) * mm, "radius": 1.89 * mm});
            skCircle(sketch, "E229.MirrorC", {"center": v(-35.56, 33.02) * mm, "radius": 1.89 * mm});
            skCircle(sketch, "E230.MirrorC", {"center": v(-30.48, 45.72) * mm, "radius": 1.89 * mm});
            skCircle(sketch, "E231.MirrorC", {"center": v(-25.4, 58.42) * mm, "radius": 1.89 * mm});
            skCircle(sketch, "E232.MirrorC", {"center": v(-20.32, 71.12) * mm, "radius": 1.89 * mm});
            skCircle(sketch, "E233.MirrorC", {"center": v(-45.72, 102.87) * mm, "radius": 1.89 * mm});
            skCircle(sketch, "E234.MirrorC", {"center": v(-10.16, 64.77) * mm, "radius": 1.89 * mm});
            skCircle(sketch, "E235.MirrorC", {"center": v(-15.24, 52.07) * mm, "radius": 1.89 * mm});
            skCircle(sketch, "E236.MirrorC", {"center": v(-30.48, 115.57) * mm, "radius": 1.89 * mm});
            skCircle(sketch, "E237.MirrorC", {"center": v(-30.48, 13.97) * mm, "radius": 1.89 * mm});
            skCircle(sketch, "E238.MirrorC", {"center": v(-25.4, 26.67) * mm, "radius": 1.89 * mm});
            skCircle(sketch, "E239.MirrorC", {"center": v(-30.48, 128.27) * mm, "radius": 1.89 * mm});
            skCircle(sketch, "E240.MirrorC", {"center": v(-10.16, 128.27) * mm, "radius": 1.89 * mm});
            skCircle(sketch, "E241.MirrorC", {"center": v(-20.32, 39.37) * mm, "radius": 1.89 * mm});
            skCircle(sketch, "E242.MirrorC", {"center": v(-55.88, 77.47) * mm, "radius": 1.89 * mm});
            skCircle(sketch, "E243.MirrorC", {"center": v(-40.64, 121.92) * mm, "radius": 1.89 * mm});
            skCircle(sketch, "E244.MirrorC", {"center": v(-45.72, 71.12) * mm, "radius": 1.89 * mm});
            skCircle(sketch, "E245.MirrorC", {"center": v(-35.56, 102.87) * mm, "radius": 1.89 * mm});
            skCircle(sketch, "E246.MirrorC", {"center": v(-15.24, 83.82) * mm, "radius": 1.89 * mm});
            skCircle(sketch, "E247.MirrorC", {"center": v(-5.08, 109.22) * mm, "radius": 1.89 * mm});
            skCircle(sketch, "E248.MirrorC", {"center": v(-10.16, 96.52) * mm, "radius": 1.89 * mm});
            skSolve(sketch);
        }
        {
            var Q0;
            Q0=makeQuery(id+"F4.imprint","IMPRINT",FACE,{"disambiguationData":[TD([[makeQuery(id+"F4.imprint","IMPRINT",EDGE,{"derivedFrom":sQuery(id+"F4.wireOp",EDGE,"E128.MirrorC")}),-1.0]])]});
            var Q1;
            Q1=makeQuery(id+"F4.imprint","IMPRINT",FACE,{"disambiguationData":[TD([[makeQuery(id+"F4.imprint","IMPRINT",EDGE,{"derivedFrom":sQuery(id+"F4.wireOp",EDGE,"E81.MirrorC")}),-1.0]])]});
            var Q2;
            Q2=makeQuery(id+"F4.imprint","IMPRINT",FACE,{"disambiguationData":[TD([[makeQuery(id+"F4.imprint","IMPRINT",EDGE,{"derivedFrom":sQuery(id+"F4.wireOp",EDGE,"E181.MirrorC")}),-1.0]])]});
            var Q3;
            Q3=makeQuery(id+"F4.imprint","IMPRINT",FACE,{"disambiguationData":[TD([[makeQuery(id+"F4.imprint","IMPRINT",EDGE,{"derivedFrom":sQuery(id+"F4.wireOp",EDGE,"E24.MirrorC")}),-1.0]])]});
            var Q4;
            Q4=makeQuery(id+"F4.imprint","IMPRINT",FACE,{"disambiguationData":[TD([[makeQuery(id+"F4.imprint","IMPRINT",EDGE,{"derivedFrom":sQuery(id+"F4.wireOp",EDGE,"E136.MirrorC")}),-1.0]])]});
            var Q5;
            Q5=makeQuery(id+"F4.imprint","IMPRINT",FACE,{"disambiguationData":[TD([[makeQuery(id+"F4.imprint","IMPRINT",EDGE,{"derivedFrom":sQuery(id+"F4.wireOp",EDGE,"E3.7.15.0")}),1.0]])]});
            var Q6;
            Q6=makeQuery(id+"F4.imprint","IMPRINT",FACE,{"disambiguationData":[TD([[makeQuery(id+"F4.imprint","IMPRINT",EDGE,{"derivedFrom":sQuery(id+"F4.wireOp",EDGE,"E5.0.10.11")}),1.0]])]});
            var Q7;
            Q7=makeQuery(id+"F4.imprint","IMPRINT",FACE,{"disambiguationData":[TD([[makeQuery(id+"F4.imprint","IMPRINT",EDGE,{"derivedFrom":sQuery(id+"F4.wireOp",EDGE,"E5.0.9.13")}),1.0]])]});
            var Q8;
            Q8=makeQuery(id+"F4.imprint","IMPRINT",FACE,{"disambiguationData":[TD([[makeQuery(id+"F4.imprint","IMPRINT",EDGE,{"derivedFrom":sQuery(id+"F4.wireOp",EDGE,"E5.0.8.15")}),1.0]])]});
            var Q9;
            Q9=makeQuery(id+"F4.imprint","IMPRINT",FACE,{"disambiguationData":[TD([[makeQuery(id+"F4.imprint","IMPRINT",EDGE,{"derivedFrom":sQuery(id+"F4.wireOp",EDGE,"E14.MirrorC")}),-1.0]])]});
            var Q10;
            Q10=makeQuery(id+"F4.imprint","IMPRINT",FACE,{"disambiguationData":[TD([[makeQuery(id+"F4.imprint","IMPRINT",EDGE,{"derivedFrom":sQuery(id+"F4.wireOp",EDGE,"E6.0.9.21")}),1.0]])]});
            var Q11;
            Q11=makeQuery(id+"F4.imprint","IMPRINT",FACE,{"disambiguationData":[TD([[makeQuery(id+"F4.imprint","IMPRINT",EDGE,{"derivedFrom":sQuery(id+"F4.wireOp",EDGE,"E6.0.5.21")}),1.0]])]});
            var Q12;
            Q12=makeQuery(id+"F4.imprint","IMPRINT",FACE,{"disambiguationData":[TD([[makeQuery(id+"F4.imprint","IMPRINT",EDGE,{"derivedFrom":sQuery(id+"F4.wireOp",EDGE,"E6.0.1.21")}),1.0]])]});
            var Q13;
            Q13=makeQuery(id+"F4.imprint","IMPRINT",FACE,{"disambiguationData":[TD([[makeQuery(id+"F4.imprint","IMPRINT",EDGE,{"derivedFrom":sQuery(id+"F4.wireOp",EDGE,"E62.MirrorC")}),-1.0]])]});
            var Q14;
            Q14=makeQuery(id+"F4.imprint","IMPRINT",FACE,{"disambiguationData":[TD([[makeQuery(id+"F4.imprint","IMPRINT",EDGE,{"derivedFrom":sQuery(id+"F4.wireOp",EDGE,"E46.MirrorC")}),-1.0]])]});
            var Q15;
            Q15=makeQuery(id+"F4.imprint","IMPRINT",FACE,{"disambiguationData":[TD([[makeQuery(id+"F4.imprint","IMPRINT",EDGE,{"derivedFrom":sQuery(id+"F4.wireOp",EDGE,"E30.MirrorC")}),-1.0]])]});
            var Q16;
            Q16=makeQuery(id+"F4.imprint","IMPRINT",FACE,{"disambiguationData":[TD([[makeQuery(id+"F4.imprint","IMPRINT",EDGE,{"derivedFrom":sQuery(id+"F4.wireOp",EDGE,"E126.MirrorC")}),-1.0]])]});
            var Q17;
            Q17=makeQuery(id+"F4.imprint","IMPRINT",FACE,{"disambiguationData":[TD([[makeQuery(id+"F4.imprint","IMPRINT",EDGE,{"derivedFrom":sQuery(id+"F4.wireOp",EDGE,"E174.MirrorC")}),-1.0]])]});
            var Q18;
            Q18=makeQuery(id+"F4.imprint","IMPRINT",FACE,{"disambiguationData":[TD([[makeQuery(id+"F4.imprint","IMPRINT",EDGE,{"derivedFrom":sQuery(id+"F4.wireOp",EDGE,"E238.MirrorC")}),-1.0]])]});
            var Q19;
            Q19=makeQuery(id+"F4.imprint","IMPRINT",FACE,{"disambiguationData":[TD([[makeQuery(id+"F4.imprint","IMPRINT",EDGE,{"derivedFrom":sQuery(id+"F4.wireOp",EDGE,"E206.MirrorC")}),-1.0]])]});
            var Q20;
            Q20=makeQuery(id+"F4.imprint","IMPRINT",FACE,{"disambiguationData":[TD([[makeQuery(id+"F4.imprint","IMPRINT",EDGE,{"derivedFrom":sQuery(id+"F4.wireOp",EDGE,"E3.5.3.0")}),1.0]])]});
            var Q21;
            Q21=makeQuery(id+"F4.imprint","IMPRINT",FACE,{"disambiguationData":[TD([[makeQuery(id+"F4.imprint","IMPRINT",EDGE,{"derivedFrom":sQuery(id+"F4.wireOp",EDGE,"E3.4.5.0")}),1.0]])]});
            var Q22;
            Q22=makeQuery(id+"F4.imprint","IMPRINT",FACE,{"disambiguationData":[TD([[makeQuery(id+"F4.imprint","IMPRINT",EDGE,{"derivedFrom":sQuery(id+"F4.wireOp",EDGE,"E3.3.7.0")}),1.0]])]});
            var Q23;
            Q23=makeQuery(id+"F4.imprint","IMPRINT",FACE,{"disambiguationData":[TD([[makeQuery(id+"F4.imprint","IMPRINT",EDGE,{"derivedFrom":sQuery(id+"F4.wireOp",EDGE,"E3.2.9.0")}),1.0]])]});
            var Q24;
            Q24=makeQuery(id+"F4.imprint","IMPRINT",FACE,{"disambiguationData":[TD([[makeQuery(id+"F4.imprint","IMPRINT",EDGE,{"derivedFrom":sQuery(id+"F4.wireOp",EDGE,"E3.4.3.0")}),1.0]])]});
            var Q25;
            Q25=makeQuery(id+"F4.imprint","IMPRINT",FACE,{"disambiguationData":[TD([[makeQuery(id+"F4.imprint","IMPRINT",EDGE,{"derivedFrom":sQuery(id+"F4.wireOp",EDGE,"E3.3.5.0")}),1.0]])]});
            var Q26;
            Q26=makeQuery(id+"F4.imprint","IMPRINT",FACE,{"disambiguationData":[TD([[makeQuery(id+"F4.imprint","IMPRINT",EDGE,{"derivedFrom":sQuery(id+"F4.wireOp",EDGE,"E3.2.7.0")}),1.0]])]});
            var Q27;
            Q27=makeQuery(id+"F4.imprint","IMPRINT",FACE,{"disambiguationData":[TD([[makeQuery(id+"F4.imprint","IMPRINT",EDGE,{"derivedFrom":sQuery(id+"F4.wireOp",EDGE,"E3.7.13.0")}),1.0]])]});
            var Q28;
            Q28=makeQuery(id+"F4.imprint","IMPRINT",FACE,{"disambiguationData":[TD([[makeQuery(id+"F4.imprint","IMPRINT",EDGE,{"derivedFrom":sQuery(id+"F4.wireOp",EDGE,"E3.5.17.0")}),1.0]])]});
            var Q29;
            Q29=makeQuery(id+"F4.imprint","IMPRINT",FACE,{"disambiguationData":[TD([[makeQuery(id+"F4.imprint","IMPRINT",EDGE,{"derivedFrom":sQuery(id+"F4.wireOp",EDGE,"E3.5.1.0")}),1.0]])]});
            var Q30;
            Q30=makeQuery(id+"F4.imprint","IMPRINT",FACE,{"disambiguationData":[TD([[makeQuery(id+"F4.imprint","IMPRINT",EDGE,{"derivedFrom":sQuery(id+"F4.wireOp",EDGE,"E5.0.10.9")}),1.0]])]});
            var Q31;
            Q31=makeQuery(id+"F4.imprint","IMPRINT",FACE,{"disambiguationData":[TD([[makeQuery(id+"F4.imprint","IMPRINT",EDGE,{"derivedFrom":sQuery(id+"F4.wireOp",EDGE,"E5.0.9.11")}),1.0]])]});
            var Q32;
            Q32=makeQuery(id+"F4.imprint","IMPRINT",FACE,{"disambiguationData":[TD([[makeQuery(id+"F4.imprint","IMPRINT",EDGE,{"derivedFrom":sQuery(id+"F4.wireOp",EDGE,"E5.0.8.13")}),1.0]])]});
            var Q33;
            Q33=makeQuery(id+"F4.imprint","IMPRINT",FACE,{"disambiguationData":[TD([[makeQuery(id+"F4.imprint","IMPRINT",EDGE,{"derivedFrom":sQuery(id+"F4.wireOp",EDGE,"E6.0.9.19")}),1.0]])]});
            var Q34;
            Q34=makeQuery(id+"F4.imprint","IMPRINT",FACE,{"disambiguationData":[TD([[makeQuery(id+"F4.imprint","IMPRINT",EDGE,{"derivedFrom":sQuery(id+"F4.wireOp",EDGE,"E6.0.5.19")}),1.0]])]});
            var Q35;
            Q35=makeQuery(id+"F4.imprint","IMPRINT",FACE,{"disambiguationData":[TD([[makeQuery(id+"F4.imprint","IMPRINT",EDGE,{"derivedFrom":sQuery(id+"F4.wireOp",EDGE,"E6.0.1.19")}),1.0]])]});
            var Q36;
            Q36=makeQuery(id+"F4.imprint","IMPRINT",FACE,{"disambiguationData":[TD([[makeQuery(id+"F4.imprint","IMPRINT",EDGE,{"derivedFrom":sQuery(id+"F4.wireOp",EDGE,"E60.MirrorC")}),-1.0]])]});
            var Q37;
            Q37=makeQuery(id+"F4.imprint","IMPRINT",FACE,{"disambiguationData":[TD([[makeQuery(id+"F4.imprint","IMPRINT",EDGE,{"derivedFrom":sQuery(id+"F4.wireOp",EDGE,"E44.MirrorC")}),-1.0]])]});
            var Q38;
            Q38=makeQuery(id+"F4.imprint","IMPRINT",FACE,{"disambiguationData":[TD([[makeQuery(id+"F4.imprint","IMPRINT",EDGE,{"derivedFrom":sQuery(id+"F4.wireOp",EDGE,"E124.MirrorC")}),-1.0]])]});
            var Q39;
            Q39=makeQuery(id+"F4.imprint","IMPRINT",FACE,{"disambiguationData":[TD([[makeQuery(id+"F4.imprint","IMPRINT",EDGE,{"derivedFrom":sQuery(id+"F4.wireOp",EDGE,"E108.MirrorC")}),-1.0]])]});
            var Q40;
            Q40=makeQuery(id+"F4.imprint","IMPRINT",FACE,{"disambiguationData":[TD([[makeQuery(id+"F4.imprint","IMPRINT",EDGE,{"derivedFrom":sQuery(id+"F4.wireOp",EDGE,"E172.MirrorC")}),-1.0]])]});
            var Q41;
            Q41=makeQuery(id+"F4.imprint","IMPRINT",FACE,{"disambiguationData":[TD([[makeQuery(id+"F4.imprint","IMPRINT",EDGE,{"derivedFrom":sQuery(id+"F4.wireOp",EDGE,"E61.MirrorC")}),-1.0]])]});
            var Q42;
            Q42=makeQuery(id+"F4.imprint","IMPRINT",FACE,{"disambiguationData":[TD([[makeQuery(id+"F4.imprint","IMPRINT",EDGE,{"derivedFrom":sQuery(id+"F4.wireOp",EDGE,"E45.MirrorC")}),-1.0]])]});
            var Q43;
            Q43=makeQuery(id+"F4.imprint","IMPRINT",FACE,{"disambiguationData":[TD([[makeQuery(id+"F4.imprint","IMPRINT",EDGE,{"derivedFrom":sQuery(id+"F4.wireOp",EDGE,"E13.MirrorC")}),-1.0]])]});
            var Q44;
            Q44=makeQuery(id+"F4.imprint","IMPRINT",FACE,{"disambiguationData":[TD([[makeQuery(id+"F4.imprint","IMPRINT",EDGE,{"derivedFrom":sQuery(id+"F4.wireOp",EDGE,"E109.MirrorC")}),-1.0]])]});
            var Q45;
            Q45=makeQuery(id+"F4.imprint","IMPRINT",FACE,{"disambiguationData":[TD([[makeQuery(id+"F4.imprint","IMPRINT",EDGE,{"derivedFrom":sQuery(id+"F4.wireOp",EDGE,"E93.MirrorC")}),-1.0]])]});
            var Q46;
            Q46=makeQuery(id+"F4.imprint","IMPRINT",FACE,{"disambiguationData":[TD([[makeQuery(id+"F4.imprint","IMPRINT",EDGE,{"derivedFrom":sQuery(id+"F4.wireOp",EDGE,"E157.MirrorC")}),-1.0]])]});
            var Q47;
            Q47=makeQuery(id+"F4.imprint","IMPRINT",FACE,{"disambiguationData":[TD([[makeQuery(id+"F4.imprint","IMPRINT",EDGE,{"derivedFrom":sQuery(id+"F4.wireOp",EDGE,"E159.MirrorC")}),-1.0]])]});
            var Q48;
            Q48=makeQuery(id+"F4.imprint","IMPRINT",FACE,{"disambiguationData":[TD([[makeQuery(id+"F4.imprint","IMPRINT",EDGE,{"derivedFrom":sQuery(id+"F4.wireOp",EDGE,"E207.MirrorC")}),-1.0]])]});
            var Q49;
            Q49=makeQuery(id+"F4.imprint","IMPRINT",FACE,{"disambiguationData":[TD([[makeQuery(id+"F4.imprint","IMPRINT",EDGE,{"derivedFrom":sQuery(id+"F4.wireOp",EDGE,"E31.MirrorC")}),-1.0]])]});
            var Q50;
            Q50=makeQuery(id+"F4.imprint","IMPRINT",FACE,{"disambiguationData":[TD([[makeQuery(id+"F4.imprint","IMPRINT",EDGE,{"derivedFrom":sQuery(id+"F4.wireOp",EDGE,"E127.MirrorC")}),-1.0]])]});
            var Q51;
            Q51=makeQuery(id+"F4.imprint","IMPRINT",FACE,{"disambiguationData":[TD([[makeQuery(id+"F4.imprint","IMPRINT",EDGE,{"derivedFrom":sQuery(id+"F4.wireOp",EDGE,"E111.MirrorC")}),-1.0]])]});
            var Q52;
            Q52=makeQuery(id+"F4.imprint","IMPRINT",FACE,{"disambiguationData":[TD([[makeQuery(id+"F4.imprint","IMPRINT",EDGE,{"derivedFrom":sQuery(id+"F4.wireOp",EDGE,"E95.MirrorC")}),-1.0]])]});
            var Q53;
            Q53=makeQuery(id+"F4.imprint","IMPRINT",FACE,{"disambiguationData":[TD([[makeQuery(id+"F4.imprint","IMPRINT",EDGE,{"derivedFrom":sQuery(id+"F4.wireOp",EDGE,"E208.MirrorC")}),-1.0]])]});
            var Q54;
            Q54=makeQuery(id+"F4.imprint","IMPRINT",FACE,{"disambiguationData":[TD([[makeQuery(id+"F4.imprint","IMPRINT",EDGE,{"derivedFrom":sQuery(id+"F4.wireOp",EDGE,"E192.MirrorC")}),-1.0]])]});
            var Q55;
            Q55=makeQuery(id+"F4.imprint","IMPRINT",FACE,{"disambiguationData":[TD([[makeQuery(id+"F4.imprint","IMPRINT",EDGE,{"derivedFrom":sQuery(id+"F4.wireOp",EDGE,"E176.MirrorC")}),-1.0]])]});
            var Q56;
            Q56=makeQuery(id+"F4.imprint","IMPRINT",FACE,{"disambiguationData":[TD([[makeQuery(id+"F4.imprint","IMPRINT",EDGE,{"derivedFrom":sQuery(id+"F4.wireOp",EDGE,"E240.MirrorC")}),-1.0]])]});
            var Q57;
            Q57=makeQuery(id+"F4.imprint","IMPRINT",FACE,{"disambiguationData":[TD([[makeQuery(id+"F4.imprint","IMPRINT",EDGE,{"derivedFrom":sQuery(id+"F4.wireOp",EDGE,"E3.4.7.0")}),1.0]])]});
            var Q58;
            Q58=makeQuery(id+"F4.imprint","IMPRINT",FACE,{"disambiguationData":[TD([[makeQuery(id+"F4.imprint","IMPRINT",EDGE,{"derivedFrom":sQuery(id+"F4.wireOp",EDGE,"E3.3.9.0")}),1.0]])]});
            var Q59;
            Q59=makeQuery(id+"F4.imprint","IMPRINT",FACE,{"disambiguationData":[TD([[makeQuery(id+"F4.imprint","IMPRINT",EDGE,{"derivedFrom":sQuery(id+"F4.wireOp",EDGE,"E3.2.11.0")}),1.0]])]});
            var Q60;
            Q60=makeQuery(id+"F4.imprint","IMPRINT",FACE,{"disambiguationData":[TD([[makeQuery(id+"F4.imprint","IMPRINT",EDGE,{"derivedFrom":sQuery(id+"F4.wireOp",EDGE,"E3.1.13.0")}),1.0]])]});
            var Q61;
            Q61=makeQuery(id+"F4.imprint","IMPRINT",FACE,{"disambiguationData":[TD([[makeQuery(id+"F4.imprint","IMPRINT",EDGE,{"derivedFrom":sQuery(id+"F4.wireOp",EDGE,"E3.7.17.0")}),1.0]])]});
            var Q62;
            Q62=makeQuery(id+"F4.imprint","IMPRINT",FACE,{"disambiguationData":[TD([[makeQuery(id+"F4.imprint","IMPRINT",EDGE,{"derivedFrom":sQuery(id+"F4.wireOp",EDGE,"E3.7.1.0")}),1.0]])]});
            var Q63;
            Q63=makeQuery(id+"F4.imprint","IMPRINT",FACE,{"disambiguationData":[TD([[makeQuery(id+"F4.imprint","IMPRINT",EDGE,{"derivedFrom":sQuery(id+"F4.wireOp",EDGE,"E3.5.5.0")}),1.0]])]});
            var Q64;
            Q64=makeQuery(id+"F4.imprint","IMPRINT",FACE,{"disambiguationData":[TD([[makeQuery(id+"F4.imprint","IMPRINT",EDGE,{"derivedFrom":sQuery(id+"F4.wireOp",EDGE,"E5.0.10.13")}),1.0]])]});
            var Q65;
            Q65=makeQuery(id+"F4.imprint","IMPRINT",FACE,{"disambiguationData":[TD([[makeQuery(id+"F4.imprint","IMPRINT",EDGE,{"derivedFrom":sQuery(id+"F4.wireOp",EDGE,"E5.0.9.15")}),1.0]])]});
            var Q66;
            Q66=makeQuery(id+"F4.imprint","IMPRINT",FACE,{"disambiguationData":[TD([[makeQuery(id+"F4.imprint","IMPRINT",EDGE,{"derivedFrom":sQuery(id+"F4.wireOp",EDGE,"E5.0.8.17")}),1.0]])]});
            var Q67;
            Q67=makeQuery(id+"F4.imprint","IMPRINT",FACE,{"disambiguationData":[TD([[makeQuery(id+"F4.imprint","IMPRINT",EDGE,{"derivedFrom":sQuery(id+"F4.wireOp",EDGE,"E5.0.8.1")}),1.0]])]});
            var Q68;
            Q68=makeQuery(id+"F4.imprint","IMPRINT",FACE,{"disambiguationData":[TD([[makeQuery(id+"F4.imprint","IMPRINT",EDGE,{"derivedFrom":sQuery(id+"F4.wireOp",EDGE,"E6.0.10.19")}),1.0]])]});
            var Q69;
            Q69=makeQuery(id+"F4.imprint","IMPRINT",FACE,{"disambiguationData":[TD([[makeQuery(id+"F4.imprint","IMPRINT",EDGE,{"derivedFrom":sQuery(id+"F4.wireOp",EDGE,"E6.0.2.19")}),1.0]])]});
            var Q70;
            Q70=makeQuery(id+"F4.imprint","IMPRINT",FACE,{"disambiguationData":[TD([[makeQuery(id+"F4.imprint","IMPRINT",EDGE,{"derivedFrom":sQuery(id+"F4.wireOp",EDGE,"E64.MirrorC")}),-1.0]])]});
            var Q71;
            Q71=makeQuery(id+"F4.imprint","IMPRINT",FACE,{"disambiguationData":[TD([[makeQuery(id+"F4.imprint","IMPRINT",EDGE,{"derivedFrom":sQuery(id+"F4.wireOp",EDGE,"E96.MirrorC")}),-1.0]])]});
            var Q72;
            Q72=makeQuery(id+"F4.imprint","IMPRINT",FACE,{"disambiguationData":[TD([[makeQuery(id+"F4.imprint","IMPRINT",EDGE,{"derivedFrom":sQuery(id+"F4.wireOp",EDGE,"E80.MirrorC")}),-1.0]])]});
            var Q73;
            Q73=makeQuery(id+"F4.imprint","IMPRINT",FACE,{"disambiguationData":[TD([[makeQuery(id+"F4.imprint","IMPRINT",EDGE,{"derivedFrom":sQuery(id+"F4.wireOp",EDGE,"E144.MirrorC")}),-1.0]])]});
            var Q74;
            Q74=makeQuery(id+"F4.imprint","IMPRINT",FACE,{"disambiguationData":[TD([[makeQuery(id+"F4.imprint","IMPRINT",EDGE,{"derivedFrom":sQuery(id+"F4.wireOp",EDGE,"E160.MirrorC")}),-1.0]])]});
            var Q75;
            Q75=makeQuery(id+"F4.imprint","IMPRINT",FACE,{"disambiguationData":[TD([[makeQuery(id+"F4.imprint","IMPRINT",EDGE,{"derivedFrom":sQuery(id+"F4.wireOp",EDGE,"E241.MirrorC")}),-1.0]])]});
            var Q76;
            Q76=makeQuery(id+"F4.imprint","IMPRINT",FACE,{"disambiguationData":[TD([[makeQuery(id+"F4.imprint","IMPRINT",EDGE,{"derivedFrom":sQuery(id+"F4.wireOp",EDGE,"E17.MirrorC")}),-1.0]])]});
            var Q77;
            Q77=makeQuery(id+"F4.imprint","IMPRINT",FACE,{"disambiguationData":[TD([[makeQuery(id+"F4.imprint","IMPRINT",EDGE,{"derivedFrom":sQuery(id+"F4.wireOp",EDGE,"E129.MirrorC")}),-1.0]])]});
            var Q78;
            Q78=makeQuery(id+"F4.imprint","IMPRINT",FACE,{"disambiguationData":[TD([[makeQuery(id+"F4.imprint","IMPRINT",EDGE,{"derivedFrom":sQuery(id+"F4.wireOp",EDGE,"E113.MirrorC")}),-1.0]])]});
            var Q79;
            Q79=makeQuery(id+"F4.imprint","IMPRINT",FACE,{"disambiguationData":[TD([[makeQuery(id+"F4.imprint","IMPRINT",EDGE,{"derivedFrom":sQuery(id+"F4.wireOp",EDGE,"E209.MirrorC")}),-1.0]])]});
            var Q80;
            Q80=makeQuery(id+"F4.imprint","IMPRINT",FACE,{"disambiguationData":[TD([[makeQuery(id+"F4.imprint","IMPRINT",EDGE,{"derivedFrom":sQuery(id+"F4.wireOp",EDGE,"E193.MirrorC")}),-1.0]])]});
            var Q81;
            Q81=makeQuery(id+"F4.imprint","IMPRINT",FACE,{"disambiguationData":[TD([[makeQuery(id+"F4.imprint","IMPRINT",EDGE,{"derivedFrom":sQuery(id+"F4.wireOp",EDGE,"E3.4.9.0")}),1.0]])]});
            var Q82;
            Q82=makeQuery(id+"F4.imprint","IMPRINT",FACE,{"disambiguationData":[TD([[makeQuery(id+"F4.imprint","IMPRINT",EDGE,{"derivedFrom":sQuery(id+"F4.wireOp",EDGE,"E3.3.11.0")}),1.0]])]});
            var Q83;
            Q83=makeQuery(id+"F4.imprint","IMPRINT",FACE,{"disambiguationData":[TD([[makeQuery(id+"F4.imprint","IMPRINT",EDGE,{"derivedFrom":sQuery(id+"F4.wireOp",EDGE,"E3.2.13.0")}),1.0]])]});
            var Q84;
            Q84=makeQuery(id+"F4.imprint","IMPRINT",FACE,{"disambiguationData":[TD([[makeQuery(id+"F4.imprint","IMPRINT",EDGE,{"derivedFrom":sQuery(id+"F4.wireOp",EDGE,"E3.1.15.0")}),1.0]])]});
            var Q85;
            Q85=makeQuery(id+"F4.imprint","IMPRINT",FACE,{"disambiguationData":[TD([[makeQuery(id+"F4.imprint","IMPRINT",EDGE,{"derivedFrom":sQuery(id+"F4.wireOp",EDGE,"E3.7.3.0")}),1.0]])]});
            var Q86;
            Q86=makeQuery(id+"F4.imprint","IMPRINT",FACE,{"disambiguationData":[TD([[makeQuery(id+"F4.imprint","IMPRINT",EDGE,{"derivedFrom":sQuery(id+"F4.wireOp",EDGE,"E3.5.7.0")}),1.0]])]});
            var Q87;
            Q87=makeQuery(id+"F4.imprint","IMPRINT",FACE,{"disambiguationData":[TD([[makeQuery(id+"F4.imprint","IMPRINT",EDGE,{"derivedFrom":sQuery(id+"F4.wireOp",EDGE,"E5.0.10.15")}),1.0]])]});
            var Q88;
            Q88=makeQuery(id+"F4.imprint","IMPRINT",FACE,{"disambiguationData":[TD([[makeQuery(id+"F4.imprint","IMPRINT",EDGE,{"derivedFrom":sQuery(id+"F4.wireOp",EDGE,"E5.0.9.17")}),1.0]])]});
            var Q89;
            Q89=makeQuery(id+"F4.imprint","IMPRINT",FACE,{"disambiguationData":[TD([[makeQuery(id+"F4.imprint","IMPRINT",EDGE,{"derivedFrom":sQuery(id+"F4.wireOp",EDGE,"E5.0.9.1")}),1.0]])]});
            var Q90;
            Q90=makeQuery(id+"F4.imprint","IMPRINT",FACE,{"disambiguationData":[TD([[makeQuery(id+"F4.imprint","IMPRINT",EDGE,{"derivedFrom":sQuery(id+"F4.wireOp",EDGE,"E5.0.8.3")}),1.0]])]});
            var Q91;
            Q91=makeQuery(id+"F4.imprint","IMPRINT",FACE,{"disambiguationData":[TD([[makeQuery(id+"F4.imprint","IMPRINT",EDGE,{"derivedFrom":sQuery(id+"F4.wireOp",EDGE,"E6.0.10.21")}),1.0]])]});
            var Q92;
            Q92=makeQuery(id+"F4.imprint","IMPRINT",FACE,{"disambiguationData":[TD([[makeQuery(id+"F4.imprint","IMPRINT",EDGE,{"derivedFrom":sQuery(id+"F4.wireOp",EDGE,"E6.0.2.21")}),1.0]])]});
            var Q93;
            Q93=makeQuery(id+"F4.imprint","IMPRINT",FACE,{"disambiguationData":[TD([[makeQuery(id+"F4.imprint","IMPRINT",EDGE,{"derivedFrom":sQuery(id+"F4.wireOp",EDGE,"E18.MirrorC")}),-1.0]])]});
            var Q94;
            Q94=makeQuery(id+"F4.imprint","IMPRINT",FACE,{"disambiguationData":[TD([[makeQuery(id+"F4.imprint","IMPRINT",EDGE,{"derivedFrom":sQuery(id+"F4.wireOp",EDGE,"E130.MirrorC")}),-1.0]])]});
            var Q95;
            Q95=makeQuery(id+"F4.imprint","IMPRINT",FACE,{"disambiguationData":[TD([[makeQuery(id+"F4.imprint","IMPRINT",EDGE,{"derivedFrom":sQuery(id+"F4.wireOp",EDGE,"E114.MirrorC")}),-1.0]])]});
            var Q96;
            Q96=makeQuery(id+"F4.imprint","IMPRINT",FACE,{"disambiguationData":[TD([[makeQuery(id+"F4.imprint","IMPRINT",EDGE,{"derivedFrom":sQuery(id+"F4.wireOp",EDGE,"E82.MirrorC")}),-1.0]])]});
            var Q97;
            Q97=makeQuery(id+"F4.imprint","IMPRINT",FACE,{"disambiguationData":[TD([[makeQuery(id+"F4.imprint","IMPRINT",EDGE,{"derivedFrom":sQuery(id+"F4.wireOp",EDGE,"E194.MirrorC")}),-1.0]])]});
            var Q98;
            Q98=makeQuery(id+"F4.imprint","IMPRINT",FACE,{"disambiguationData":[TD([[makeQuery(id+"F4.imprint","IMPRINT",EDGE,{"derivedFrom":sQuery(id+"F4.wireOp",EDGE,"E67.MirrorC")}),-1.0]])]});
            var Q99;
            Q99=makeQuery(id+"F4.imprint","IMPRINT",FACE,{"disambiguationData":[TD([[makeQuery(id+"F4.imprint","IMPRINT",EDGE,{"derivedFrom":sQuery(id+"F4.wireOp",EDGE,"E115.MirrorC")}),-1.0]])]});
            var Q100;
            Q100=makeQuery(id+"F4.imprint","IMPRINT",FACE,{"disambiguationData":[TD([[makeQuery(id+"F4.imprint","IMPRINT",EDGE,{"derivedFrom":sQuery(id+"F4.wireOp",EDGE,"E99.MirrorC")}),-1.0]])]});
            var Q101;
            Q101=makeQuery(id+"F4.imprint","IMPRINT",FACE,{"disambiguationData":[TD([[makeQuery(id+"F4.imprint","IMPRINT",EDGE,{"derivedFrom":sQuery(id+"F4.wireOp",EDGE,"E227.MirrorC")}),-1.0]])]});
            var Q102;
            Q102=makeQuery(id+"F4.imprint","IMPRINT",FACE,{"disambiguationData":[TD([[makeQuery(id+"F4.imprint","IMPRINT",EDGE,{"derivedFrom":sQuery(id+"F4.wireOp",EDGE,"E211.MirrorC")}),-1.0]])]});
            var Q103;
            Q103=makeQuery(id+"F4.imprint","IMPRINT",FACE,{"disambiguationData":[TD([[makeQuery(id+"F4.imprint","IMPRINT",EDGE,{"derivedFrom":sQuery(id+"F4.wireOp",EDGE,"E3.4.11.0")}),1.0]])]});
            var Q104;
            Q104=makeQuery(id+"F4.imprint","IMPRINT",FACE,{"disambiguationData":[TD([[makeQuery(id+"F4.imprint","IMPRINT",EDGE,{"derivedFrom":sQuery(id+"F4.wireOp",EDGE,"E3.3.13.0")}),1.0]])]});
            var Q105;
            Q105=makeQuery(id+"F4.imprint","IMPRINT",FACE,{"disambiguationData":[TD([[makeQuery(id+"F4.imprint","IMPRINT",EDGE,{"derivedFrom":sQuery(id+"F4.wireOp",EDGE,"E3.2.15.0")}),1.0]])]});
            var Q106;
            Q106=makeQuery(id+"F4.imprint","IMPRINT",FACE,{"disambiguationData":[TD([[makeQuery(id+"F4.imprint","IMPRINT",EDGE,{"derivedFrom":sQuery(id+"F4.wireOp",EDGE,"E3.1.17.0")}),1.0]])]});
            var Q107;
            Q107=makeQuery(id+"F4.imprint","IMPRINT",FACE,{"disambiguationData":[TD([[makeQuery(id+"F4.imprint","IMPRINT",EDGE,{"derivedFrom":sQuery(id+"F4.wireOp",EDGE,"E3.7.5.0")}),1.0]])]});
            var Q108;
            Q108=makeQuery(id+"F4.imprint","IMPRINT",FACE,{"disambiguationData":[TD([[makeQuery(id+"F4.imprint","IMPRINT",EDGE,{"derivedFrom":sQuery(id+"F4.wireOp",EDGE,"E3.5.9.0")}),1.0]])]});
            var Q109;
            Q109=makeQuery(id+"F4.imprint","IMPRINT",FACE,{"disambiguationData":[TD([[makeQuery(id+"F4.imprint","IMPRINT",EDGE,{"derivedFrom":sQuery(id+"F4.wireOp",EDGE,"E5.0.10.17")}),1.0]])]});
            var Q110;
            Q110=makeQuery(id+"F4.imprint","IMPRINT",FACE,{"disambiguationData":[TD([[makeQuery(id+"F4.imprint","IMPRINT",EDGE,{"derivedFrom":sQuery(id+"F4.wireOp",EDGE,"E5.0.10.1")}),1.0]])]});
            var Q111;
            Q111=makeQuery(id+"F4.imprint","IMPRINT",FACE,{"disambiguationData":[TD([[makeQuery(id+"F4.imprint","IMPRINT",EDGE,{"derivedFrom":sQuery(id+"F4.wireOp",EDGE,"E5.0.9.3")}),1.0]])]});
            var Q112;
            Q112=makeQuery(id+"F4.imprint","IMPRINT",FACE,{"disambiguationData":[TD([[makeQuery(id+"F4.imprint","IMPRINT",EDGE,{"derivedFrom":sQuery(id+"F4.wireOp",EDGE,"E5.0.8.5")}),1.0]])]});
            var Q113;
            Q113=makeQuery(id+"F4.imprint","IMPRINT",FACE,{"disambiguationData":[TD([[makeQuery(id+"F4.imprint","IMPRINT",EDGE,{"derivedFrom":sQuery(id+"F4.wireOp",EDGE,"E6.0.7.19")}),1.0]])]});
            var Q114;
            Q114=makeQuery(id+"F4.imprint","IMPRINT",FACE,{"disambiguationData":[TD([[makeQuery(id+"F4.imprint","IMPRINT",EDGE,{"derivedFrom":sQuery(id+"F4.wireOp",EDGE,"E6.0.3.19")}),1.0]])]});
            var Q115;
            Q115=makeQuery(id+"F4.imprint","IMPRINT",FACE,{"disambiguationData":[TD([[makeQuery(id+"F4.imprint","IMPRINT",EDGE,{"derivedFrom":sQuery(id+"F4.wireOp",EDGE,"E68.MirrorC")}),-1.0]])]});
            var Q116;
            Q116=makeQuery(id+"F4.imprint","IMPRINT",FACE,{"disambiguationData":[TD([[makeQuery(id+"F4.imprint","IMPRINT",EDGE,{"derivedFrom":sQuery(id+"F4.wireOp",EDGE,"E52.MirrorC")}),-1.0]])]});
            var Q117;
            Q117=makeQuery(id+"F4.imprint","IMPRINT",FACE,{"disambiguationData":[TD([[makeQuery(id+"F4.imprint","IMPRINT",EDGE,{"derivedFrom":sQuery(id+"F4.wireOp",EDGE,"E36.MirrorC")}),-1.0]])]});
            var Q118;
            Q118=makeQuery(id+"F4.imprint","IMPRINT",FACE,{"disambiguationData":[TD([[makeQuery(id+"F4.imprint","IMPRINT",EDGE,{"derivedFrom":sQuery(id+"F4.wireOp",EDGE,"E116.MirrorC")}),-1.0]])]});
            var Q119;
            Q119=makeQuery(id+"F4.imprint","IMPRINT",FACE,{"disambiguationData":[TD([[makeQuery(id+"F4.imprint","IMPRINT",EDGE,{"derivedFrom":sQuery(id+"F4.wireOp",EDGE,"E100.MirrorC")}),-1.0]])]});
            var Q120;
            Q120=makeQuery(id+"F4.imprint","IMPRINT",FACE,{"disambiguationData":[TD([[makeQuery(id+"F4.imprint","IMPRINT",EDGE,{"derivedFrom":sQuery(id+"F4.wireOp",EDGE,"E228.MirrorC")}),-1.0]])]});
            var Q121;
            Q121=makeQuery(id+"F4.imprint","IMPRINT",FACE,{"disambiguationData":[TD([[makeQuery(id+"F4.imprint","IMPRINT",EDGE,{"derivedFrom":sQuery(id+"F4.wireOp",EDGE,"E212.MirrorC")}),-1.0]])]});
            var Q122;
            Q122=makeQuery(id+"F4.imprint","IMPRINT",FACE,{"disambiguationData":[TD([[makeQuery(id+"F4.imprint","IMPRINT",EDGE,{"derivedFrom":sQuery(id+"F4.wireOp",EDGE,"E101.MirrorC")}),-1.0]])]});
            var Q123;
            Q123=makeQuery(id+"F4.imprint","IMPRINT",FACE,{"disambiguationData":[TD([[makeQuery(id+"F4.imprint","IMPRINT",EDGE,{"derivedFrom":sQuery(id+"F4.wireOp",EDGE,"E53.MirrorC")}),-1.0]])]});
            var Q124;
            Q124=makeQuery(id+"F4.imprint","IMPRINT",FACE,{"disambiguationData":[TD([[makeQuery(id+"F4.imprint","IMPRINT",EDGE,{"derivedFrom":sQuery(id+"F4.wireOp",EDGE,"E117.MirrorC")}),-1.0]])]});
            var Q125;
            Q125=makeQuery(id+"F4.imprint","IMPRINT",FACE,{"disambiguationData":[TD([[makeQuery(id+"F4.imprint","IMPRINT",EDGE,{"derivedFrom":sQuery(id+"F4.wireOp",EDGE,"E245.MirrorC")}),-1.0]])]});
            var Q126;
            Q126=makeQuery(id+"F4.imprint","IMPRINT",FACE,{"disambiguationData":[TD([[makeQuery(id+"F4.imprint","IMPRINT",EDGE,{"derivedFrom":sQuery(id+"F4.wireOp",EDGE,"E3.2.17.0")}),1.0]])]});
            var Q127;
            Q127=makeQuery(id+"F4.imprint","IMPRINT",FACE,{"disambiguationData":[TD([[makeQuery(id+"F4.imprint","IMPRINT",EDGE,{"derivedFrom":sQuery(id+"F4.wireOp",EDGE,"E3.2.1.0")}),1.0]])]});
            var Q128;
            Q128=makeQuery(id+"F4.imprint","IMPRINT",FACE,{"disambiguationData":[TD([[makeQuery(id+"F4.imprint","IMPRINT",EDGE,{"derivedFrom":sQuery(id+"F4.wireOp",EDGE,"E3.5.11.0")}),1.0]])]});
            var Q129;
            Q129=makeQuery(id+"F4.imprint","IMPRINT",FACE,{"disambiguationData":[TD([[makeQuery(id+"F4.imprint","IMPRINT",EDGE,{"derivedFrom":sQuery(id+"F4.wireOp",EDGE,"E3.4.13.0")}),1.0]])]});
            var Q130;
            Q130=makeQuery(id+"F4.imprint","IMPRINT",FACE,{"disambiguationData":[TD([[makeQuery(id+"F4.imprint","IMPRINT",EDGE,{"derivedFrom":sQuery(id+"F4.wireOp",EDGE,"E3.3.15.0")}),1.0]])]});
            var Q131;
            Q131=makeQuery(id+"F4.imprint","IMPRINT",FACE,{"disambiguationData":[TD([[makeQuery(id+"F4.imprint","IMPRINT",EDGE,{"derivedFrom":sQuery(id+"F4.wireOp",EDGE,"E5.0.9.5")}),1.0]])]});
            var Q132;
            Q132=makeQuery(id+"F4.imprint","IMPRINT",FACE,{"disambiguationData":[TD([[makeQuery(id+"F4.imprint","IMPRINT",EDGE,{"derivedFrom":sQuery(id+"F4.wireOp",EDGE,"E5.0.8.7")}),1.0]])]});
            var Q133;
            Q133=makeQuery(id+"F4.imprint","IMPRINT",FACE,{"disambiguationData":[TD([[makeQuery(id+"F4.imprint","IMPRINT",EDGE,{"derivedFrom":sQuery(id+"F4.wireOp",EDGE,"E3.7.7.0")}),1.0]])]});
            var Q134;
            Q134=makeQuery(id+"F4.imprint","IMPRINT",FACE,{"disambiguationData":[TD([[makeQuery(id+"F4.imprint","IMPRINT",EDGE,{"derivedFrom":sQuery(id+"F4.wireOp",EDGE,"E6.0.3.21")}),1.0]])]});
            var Q135;
            Q135=makeQuery(id+"F4.imprint","IMPRINT",FACE,{"disambiguationData":[TD([[makeQuery(id+"F4.imprint","IMPRINT",EDGE,{"derivedFrom":sQuery(id+"F4.wireOp",EDGE,"E5.0.10.3")}),1.0]])]});
            var Q136;
            Q136=makeQuery(id+"F4.imprint","IMPRINT",FACE,{"disambiguationData":[TD([[makeQuery(id+"F4.imprint","IMPRINT",EDGE,{"derivedFrom":sQuery(id+"F4.wireOp",EDGE,"E22.MirrorC")}),-1.0]])]});
            var Q137;
            Q137=makeQuery(id+"F4.imprint","IMPRINT",FACE,{"disambiguationData":[TD([[makeQuery(id+"F4.imprint","IMPRINT",EDGE,{"derivedFrom":sQuery(id+"F4.wireOp",EDGE,"E6.0.7.21")}),1.0]])]});
            var Q138;
            Q138=makeQuery(id+"F4.imprint","IMPRINT",FACE,{"disambiguationData":[TD([[makeQuery(id+"F4.imprint","IMPRINT",EDGE,{"derivedFrom":sQuery(id+"F4.wireOp",EDGE,"E86.MirrorC")}),-1.0]])]});
            var Q139;
            Q139=makeQuery(id+"F4.imprint","IMPRINT",FACE,{"disambiguationData":[TD([[makeQuery(id+"F4.imprint","IMPRINT",EDGE,{"derivedFrom":sQuery(id+"F4.wireOp",EDGE,"E150.MirrorC")}),-1.0]])]});
            var Q140;
            Q140=makeQuery(id+"F4.imprint","IMPRINT",FACE,{"disambiguationData":[TD([[makeQuery(id+"F4.imprint","IMPRINT",EDGE,{"derivedFrom":sQuery(id+"F4.wireOp",EDGE,"E134.MirrorC")}),-1.0]])]});
            var Q141;
            Q141=makeQuery(id+"F4.imprint","IMPRINT",FACE,{"disambiguationData":[TD([[makeQuery(id+"F4.imprint","IMPRINT",EDGE,{"derivedFrom":sQuery(id+"F4.wireOp",EDGE,"E118.MirrorC")}),-1.0]])]});
            var Q142;
            Q142=makeQuery(id+"F4.imprint","IMPRINT",FACE,{"disambiguationData":[TD([[makeQuery(id+"F4.imprint","IMPRINT",EDGE,{"derivedFrom":sQuery(id+"F4.wireOp",EDGE,"E198.MirrorC")}),-1.0]])]});
            var Q143;
            Q143=makeQuery(id+"F4.imprint","IMPRINT",FACE,{"disambiguationData":[TD([[makeQuery(id+"F4.imprint","IMPRINT",EDGE,{"derivedFrom":sQuery(id+"F4.wireOp",EDGE,"E166.MirrorC")}),-1.0]])]});
            var Q144;
            Q144=makeQuery(id+"F4.imprint","IMPRINT",FACE,{"disambiguationData":[TD([[makeQuery(id+"F4.imprint","IMPRINT",EDGE,{"derivedFrom":sQuery(id+"F4.wireOp",EDGE,"E23.MirrorC")}),-1.0]])]});
            var Q145;
            Q145=makeQuery(id+"F4.imprint","IMPRINT",FACE,{"disambiguationData":[TD([[makeQuery(id+"F4.imprint","IMPRINT",EDGE,{"derivedFrom":sQuery(id+"F4.wireOp",EDGE,"E55.MirrorC")}),-1.0]])]});
            var Q146;
            Q146=makeQuery(id+"F4.imprint","IMPRINT",FACE,{"disambiguationData":[TD([[makeQuery(id+"F4.imprint","IMPRINT",EDGE,{"derivedFrom":sQuery(id+"F4.wireOp",EDGE,"E151.MirrorC")}),-1.0]])]});
            var Q147;
            Q147=makeQuery(id+"F4.imprint","IMPRINT",FACE,{"disambiguationData":[TD([[makeQuery(id+"F4.imprint","IMPRINT",EDGE,{"derivedFrom":sQuery(id+"F4.wireOp",EDGE,"E119.MirrorC")}),-1.0]])]});
            var Q148;
            Q148=makeQuery(id+"F4.imprint","IMPRINT",FACE,{"disambiguationData":[TD([[makeQuery(id+"F4.imprint","IMPRINT",EDGE,{"derivedFrom":sQuery(id+"F4.wireOp",EDGE,"E199.MirrorC")}),-1.0]])]});
            var Q149;
            Q149=makeQuery(id+"F4.imprint","IMPRINT",FACE,{"disambiguationData":[TD([[makeQuery(id+"F4.imprint","IMPRINT",EDGE,{"derivedFrom":sQuery(id+"F4.wireOp",EDGE,"E167.MirrorC")}),-1.0]])]});
            var Q150;
            Q150=makeQuery(id+"F4.imprint","IMPRINT",FACE,{"disambiguationData":[TD([[makeQuery(id+"F4.imprint","IMPRINT",EDGE,{"derivedFrom":sQuery(id+"F4.wireOp",EDGE,"E5.0.9.7")}),1.0]])]});
            var Q151;
            Q151=makeQuery(id+"F4.imprint","IMPRINT",FACE,{"disambiguationData":[TD([[makeQuery(id+"F4.imprint","IMPRINT",EDGE,{"derivedFrom":sQuery(id+"F4.wireOp",EDGE,"E5.0.8.9")}),1.0]])]});
            var Q152;
            Q152=makeQuery(id+"F4.imprint","IMPRINT",FACE,{"disambiguationData":[TD([[makeQuery(id+"F4.imprint","IMPRINT",EDGE,{"derivedFrom":sQuery(id+"F4.wireOp",EDGE,"E3.7.9.0")}),1.0]])]});
            var Q153;
            Q153=makeQuery(id+"F4.imprint","IMPRINT",FACE,{"disambiguationData":[TD([[makeQuery(id+"F4.imprint","IMPRINT",EDGE,{"derivedFrom":sQuery(id+"F4.wireOp",EDGE,"E6.0.4.19")}),1.0]])]});
            var Q154;
            Q154=makeQuery(id+"F4.imprint","IMPRINT",FACE,{"disambiguationData":[TD([[makeQuery(id+"F4.imprint","IMPRINT",EDGE,{"derivedFrom":sQuery(id+"F4.wireOp",EDGE,"E5.0.10.5")}),1.0]])]});
            var Q155;
            Q155=makeQuery(id+"F4.imprint","IMPRINT",FACE,{"disambiguationData":[TD([[makeQuery(id+"F4.imprint","IMPRINT",EDGE,{"derivedFrom":sQuery(id+"F4.wireOp",EDGE,"E6.0.8.19")}),1.0]])]});
            var Q156;
            Q156=makeQuery(id+"F4.imprint","IMPRINT",FACE,{"disambiguationData":[TD([[makeQuery(id+"F4.imprint","IMPRINT",EDGE,{"derivedFrom":sQuery(id+"F4.wireOp",EDGE,"E56.MirrorC")}),-1.0]])]});
            var Q157;
            Q157=makeQuery(id+"F4.imprint","IMPRINT",FACE,{"disambiguationData":[TD([[makeQuery(id+"F4.imprint","IMPRINT",EDGE,{"derivedFrom":sQuery(id+"F4.wireOp",EDGE,"E152.MirrorC")}),-1.0]])]});
            var Q158;
            Q158=makeQuery(id+"F4.imprint","IMPRINT",FACE,{"disambiguationData":[TD([[makeQuery(id+"F4.imprint","IMPRINT",EDGE,{"derivedFrom":sQuery(id+"F4.wireOp",EDGE,"E200.MirrorC")}),-1.0]])]});
            var Q159;
            Q159=makeQuery(id+"F4.imprint","IMPRINT",FACE,{"disambiguationData":[TD([[makeQuery(id+"F4.imprint","IMPRINT",EDGE,{"derivedFrom":sQuery(id+"F4.wireOp",EDGE,"E168.MirrorC")}),-1.0]])]});
            var Q160;
            Q160=makeQuery(id+"F4.imprint","IMPRINT",FACE,{"disambiguationData":[TD([[makeQuery(id+"F4.imprint","IMPRINT",EDGE,{"derivedFrom":sQuery(id+"F4.wireOp",EDGE,"E3.3.1.0")}),1.0]])]});
            var Q161;
            Q161=makeQuery(id+"F4.imprint","IMPRINT",FACE,{"disambiguationData":[TD([[makeQuery(id+"F4.imprint","IMPRINT",EDGE,{"derivedFrom":sQuery(id+"F4.wireOp",EDGE,"E3.2.3.0")}),1.0]])]});
            var Q162;
            Q162=makeQuery(id+"F4.imprint","IMPRINT",FACE,{"disambiguationData":[TD([[makeQuery(id+"F4.imprint","IMPRINT",EDGE,{"derivedFrom":sQuery(id+"F4.wireOp",EDGE,"E3.5.13.0")}),1.0]])]});
            var Q163;
            Q163=makeQuery(id+"F4.imprint","IMPRINT",FACE,{"disambiguationData":[TD([[makeQuery(id+"F4.imprint","IMPRINT",EDGE,{"derivedFrom":sQuery(id+"F4.wireOp",EDGE,"E3.4.15.0")}),1.0]])]});
            var Q164;
            Q164=makeQuery(id+"F4.imprint","IMPRINT",FACE,{"disambiguationData":[TD([[makeQuery(id+"F4.imprint","IMPRINT",EDGE,{"derivedFrom":sQuery(id+"F4.wireOp",EDGE,"E3.3.17.0")}),1.0]])]});
            var Q165;
            Q165=makeQuery(id+"F4.imprint","IMPRINT",FACE,{"disambiguationData":[TD([[makeQuery(id+"F4.imprint","IMPRINT",EDGE,{"derivedFrom":sQuery(id+"F4.wireOp",EDGE,"E89.MirrorC")}),-1.0]])]});
            var Q166;
            Q166=makeQuery(id+"F4.imprint","IMPRINT",FACE,{"disambiguationData":[TD([[makeQuery(id+"F4.imprint","IMPRINT",EDGE,{"derivedFrom":sQuery(id+"F4.wireOp",EDGE,"E57.MirrorC")}),-1.0]])]});
            var Q167;
            Q167=makeQuery(id+"F4.imprint","IMPRINT",FACE,{"disambiguationData":[TD([[makeQuery(id+"F4.imprint","IMPRINT",EDGE,{"derivedFrom":sQuery(id+"F4.wireOp",EDGE,"E153.MirrorC")}),-1.0]])]});
            var Q168;
            Q168=makeQuery(id+"F4.imprint","IMPRINT",FACE,{"disambiguationData":[TD([[makeQuery(id+"F4.imprint","IMPRINT",EDGE,{"derivedFrom":sQuery(id+"F4.wireOp",EDGE,"E121.MirrorC")}),-1.0]])]});
            var Q169;
            Q169=makeQuery(id+"F4.imprint","IMPRINT",FACE,{"disambiguationData":[TD([[makeQuery(id+"F4.imprint","IMPRINT",EDGE,{"derivedFrom":sQuery(id+"F4.wireOp",EDGE,"E201.MirrorC")}),-1.0]])]});
            var Q170;
            Q170=makeQuery(id+"F4.imprint","IMPRINT",FACE,{"disambiguationData":[TD([[makeQuery(id+"F4.imprint","IMPRINT",EDGE,{"derivedFrom":sQuery(id+"F4.wireOp",EDGE,"E169.MirrorC")}),-1.0]])]});
            var Q171;
            Q171=makeQuery(id+"F4.imprint","IMPRINT",FACE,{"disambiguationData":[TD([[makeQuery(id+"F4.imprint","IMPRINT",EDGE,{"derivedFrom":sQuery(id+"F4.wireOp",EDGE,"E233.MirrorC")}),-1.0]])]});
            var Q172;
            Q172=makeQuery(id+"F4.imprint","IMPRINT",FACE,{"disambiguationData":[TD([[makeQuery(id+"F4.imprint","IMPRINT",EDGE,{"derivedFrom":sQuery(id+"F4.wireOp",EDGE,"E26.MirrorC")}),-1.0]])]});
            var Q173;
            Q173=makeQuery(id+"F4.imprint","IMPRINT",FACE,{"disambiguationData":[TD([[makeQuery(id+"F4.imprint","IMPRINT",EDGE,{"derivedFrom":sQuery(id+"F4.wireOp",EDGE,"E6.0.8.21")}),1.0]])]});
            var Q174;
            Q174=makeQuery(id+"F4.imprint","IMPRINT",FACE,{"disambiguationData":[TD([[makeQuery(id+"F4.imprint","IMPRINT",EDGE,{"derivedFrom":sQuery(id+"F4.wireOp",EDGE,"E90.MirrorC")}),-1.0]])]});
            var Q175;
            Q175=makeQuery(id+"F4.imprint","IMPRINT",FACE,{"disambiguationData":[TD([[makeQuery(id+"F4.imprint","IMPRINT",EDGE,{"derivedFrom":sQuery(id+"F4.wireOp",EDGE,"E58.MirrorC")}),-1.0]])]});
            var Q176;
            Q176=makeQuery(id+"F4.imprint","IMPRINT",FACE,{"disambiguationData":[TD([[makeQuery(id+"F4.imprint","IMPRINT",EDGE,{"derivedFrom":sQuery(id+"F4.wireOp",EDGE,"E154.MirrorC")}),-1.0]])]});
            var Q177;
            Q177=makeQuery(id+"F4.imprint","IMPRINT",FACE,{"disambiguationData":[TD([[makeQuery(id+"F4.imprint","IMPRINT",EDGE,{"derivedFrom":sQuery(id+"F4.wireOp",EDGE,"E122.MirrorC")}),-1.0]])]});
            var Q178;
            Q178=makeQuery(id+"F4.imprint","IMPRINT",FACE,{"disambiguationData":[TD([[makeQuery(id+"F4.imprint","IMPRINT",EDGE,{"derivedFrom":sQuery(id+"F4.wireOp",EDGE,"E234.MirrorC")}),-1.0]])]});
            var Q179;
            Q179=makeQuery(id+"F4.imprint","IMPRINT",FACE,{"disambiguationData":[TD([[makeQuery(id+"F4.imprint","IMPRINT",EDGE,{"derivedFrom":sQuery(id+"F4.wireOp",EDGE,"E3.3.3.0")}),1.0]])]});
            var Q180;
            Q180=makeQuery(id+"F4.imprint","IMPRINT",FACE,{"disambiguationData":[TD([[makeQuery(id+"F4.imprint","IMPRINT",EDGE,{"derivedFrom":sQuery(id+"F4.wireOp",EDGE,"E3.2.5.0")}),1.0]])]});
            var Q181;
            Q181=makeQuery(id+"F4.imprint","IMPRINT",FACE,{"disambiguationData":[TD([[makeQuery(id+"F4.imprint","IMPRINT",EDGE,{"derivedFrom":sQuery(id+"F4.wireOp",EDGE,"E3.5.15.0")}),1.0]])]});
            var Q182;
            Q182=makeQuery(id+"F4.imprint","IMPRINT",FACE,{"disambiguationData":[TD([[makeQuery(id+"F4.imprint","IMPRINT",EDGE,{"derivedFrom":sQuery(id+"F4.wireOp",EDGE,"E3.4.17.0")}),1.0]])]});
            var Q183;
            Q183=makeQuery(id+"F4.imprint","IMPRINT",FACE,{"disambiguationData":[TD([[makeQuery(id+"F4.imprint","IMPRINT",EDGE,{"derivedFrom":sQuery(id+"F4.wireOp",EDGE,"E3.4.1.0")}),1.0]])]});
            var Q184;
            Q184=makeQuery(id+"F4.imprint","IMPRINT",FACE,{"disambiguationData":[TD([[makeQuery(id+"F4.imprint","IMPRINT",EDGE,{"derivedFrom":sQuery(id+"F4.wireOp",EDGE,"E5.0.9.9")}),1.0]])]});
            var Q185;
            Q185=makeQuery(id+"F4.imprint","IMPRINT",FACE,{"disambiguationData":[TD([[makeQuery(id+"F4.imprint","IMPRINT",EDGE,{"derivedFrom":sQuery(id+"F4.wireOp",EDGE,"E5.0.8.11")}),1.0]])]});
            var Q186;
            Q186=makeQuery(id+"F4.imprint","IMPRINT",FACE,{"disambiguationData":[TD([[makeQuery(id+"F4.imprint","IMPRINT",EDGE,{"derivedFrom":sQuery(id+"F4.wireOp",EDGE,"E3.7.11.0")}),1.0]])]});
            var Q187;
            Q187=makeQuery(id+"F4.imprint","IMPRINT",FACE,{"disambiguationData":[TD([[makeQuery(id+"F4.imprint","IMPRINT",EDGE,{"derivedFrom":sQuery(id+"F4.wireOp",EDGE,"E6.0.4.21")}),1.0]])]});
            var Q188;
            Q188=makeQuery(id+"F4.imprint","IMPRINT",FACE,{"disambiguationData":[TD([[makeQuery(id+"F4.imprint","IMPRINT",EDGE,{"derivedFrom":sQuery(id+"F4.wireOp",EDGE,"E5.0.10.7")}),1.0]])]});
            var Q189;
            Q189=makeQuery(id+"F4.imprint","IMPRINT",FACE,{"disambiguationData":[TD([[makeQuery(id+"F4.imprint","IMPRINT",EDGE,{"derivedFrom":sQuery(id+"F4.wireOp",EDGE,"E59.MirrorC")}),-1.0]])]});
            var Q190;
            Q190=makeQuery(id+"F4.imprint","IMPRINT",FACE,{"disambiguationData":[TD([[makeQuery(id+"F4.imprint","IMPRINT",EDGE,{"derivedFrom":sQuery(id+"F4.wireOp",EDGE,"E155.MirrorC")}),-1.0]])]});
            var Q191;
            Q191=makeQuery(id+"F4.imprint","IMPRINT",FACE,{"disambiguationData":[TD([[makeQuery(id+"F4.imprint","IMPRINT",EDGE,{"derivedFrom":sQuery(id+"F4.wireOp",EDGE,"E123.MirrorC")}),-1.0]])]});
            var Q192;
            Q192=makeQuery(id+"F4.imprint","IMPRINT",FACE,{"disambiguationData":[TD([[makeQuery(id+"F4.imprint","IMPRINT",EDGE,{"derivedFrom":sQuery(id+"F4.wireOp",EDGE,"E203.MirrorC")}),-1.0]])]});
            var Q193;
            Q193=makeQuery(id+"F4.imprint","IMPRINT",FACE,{"disambiguationData":[TD([[makeQuery(id+"F4.imprint","IMPRINT",EDGE,{"derivedFrom":sQuery(id+"F4.wireOp",EDGE,"E171.MirrorC")}),-1.0]])]});
            var Q194;
            Q194=makeQuery(id+"F4.imprint","IMPRINT",FACE,{"disambiguationData":[TD([[makeQuery(id+"F4.imprint","IMPRINT",EDGE,{"derivedFrom":sQuery(id+"F4.wireOp",EDGE,"E235.MirrorC")}),-1.0]])]});
            var Q195;
            Q195=makeQuery(id+"F4.imprint","IMPRINT",FACE,{"disambiguationData":[TD([[makeQuery(id+"F4.imprint","IMPRINT",EDGE,{"derivedFrom":sQuery(id+"F4.wireOp",EDGE,"E3.1.11.0")}),1.0]])]});
            var Q196;
            Q196=makeQuery(id+"F4.imprint","IMPRINT",FACE,{"disambiguationData":[TD([[makeQuery(id+"F4.imprint","IMPRINT",EDGE,{"derivedFrom":sQuery(id+"F4.wireOp",EDGE,"E3.1.9.0")}),1.0]])]});
            var Q197;
            Q197=makeQuery(id+"F4.imprint","IMPRINT",FACE,{"disambiguationData":[TD([[makeQuery(id+"F4.imprint","IMPRINT",EDGE,{"derivedFrom":sQuery(id+"F4.wireOp",EDGE,"E3.1.1.0")}),1.0]])]});
            var Q198;
            Q198=makeQuery(id+"F4.imprint","IMPRINT",FACE,{"disambiguationData":[TD([[makeQuery(id+"F4.imprint","IMPRINT",EDGE,{"derivedFrom":sQuery(id+"F4.wireOp",EDGE,"E3.1.3.0")}),1.0]])]});
            var Q199;
            Q199=makeQuery(id+"F4.imprint","IMPRINT",FACE,{"disambiguationData":[TD([[makeQuery(id+"F4.imprint","IMPRINT",EDGE,{"derivedFrom":sQuery(id+"F4.wireOp",EDGE,"E3.1.5.0")}),1.0]])]});
            var Q200;
            Q200=makeQuery(id+"F4.imprint","IMPRINT",FACE,{"disambiguationData":[TD([[makeQuery(id+"F4.imprint","IMPRINT",EDGE,{"derivedFrom":sQuery(id+"F4.wireOp",EDGE,"E3.1.7.0")}),1.0]])]});
            var Q201;
            Q201=makeQuery(id+"F4.imprint","IMPRINT",FACE,{"disambiguationData":[TD([[makeQuery(id+"F4.imprint","IMPRINT",EDGE,{"derivedFrom":sQuery(id+"F4.wireOp",EDGE,"E3.6.17.0")}),1.0]])]});
            var Q202;
            Q202=makeQuery(id+"F4.imprint","IMPRINT",FACE,{"disambiguationData":[TD([[makeQuery(id+"F4.imprint","IMPRINT",EDGE,{"derivedFrom":sQuery(id+"F4.wireOp",EDGE,"E3.6.1.0")}),1.0]])]});
            var Q203;
            Q203=makeQuery(id+"F4.imprint","IMPRINT",FACE,{"disambiguationData":[TD([[makeQuery(id+"F4.imprint","IMPRINT",EDGE,{"derivedFrom":sQuery(id+"F4.wireOp",EDGE,"E5.0.11.9")}),1.0]])]});
            var Q204;
            Q204=makeQuery(id+"F4.imprint","IMPRINT",FACE,{"disambiguationData":[TD([[makeQuery(id+"F4.imprint","IMPRINT",EDGE,{"derivedFrom":sQuery(id+"F4.wireOp",EDGE,"E78.MirrorC")}),-1.0]])]});
            var Q205;
            Q205=makeQuery(id+"F4.imprint","IMPRINT",FACE,{"disambiguationData":[TD([[makeQuery(id+"F4.imprint","IMPRINT",EDGE,{"derivedFrom":sQuery(id+"F4.wireOp",EDGE,"E142.MirrorC")}),-1.0]])]});
            var Q206;
            Q206=makeQuery(id+"F4.imprint","IMPRINT",FACE,{"disambiguationData":[TD([[makeQuery(id+"F4.imprint","IMPRINT",EDGE,{"derivedFrom":sQuery(id+"F4.wireOp",EDGE,"E110.MirrorC")}),-1.0]])]});
            var Q207;
            Q207=makeQuery(id+"F4.imprint","IMPRINT",FACE,{"disambiguationData":[TD([[makeQuery(id+"F4.imprint","IMPRINT",EDGE,{"derivedFrom":sQuery(id+"F4.wireOp",EDGE,"E94.MirrorC")}),-1.0]])]});
            var Q208;
            Q208=makeQuery(id+"F4.imprint","IMPRINT",FACE,{"disambiguationData":[TD([[makeQuery(id+"F4.imprint","IMPRINT",EDGE,{"derivedFrom":sQuery(id+"F4.wireOp",EDGE,"E158.MirrorC")}),-1.0]])]});
            var Q209;
            Q209=makeQuery(id+"F4.imprint","IMPRINT",FACE,{"disambiguationData":[TD([[makeQuery(id+"F4.imprint","IMPRINT",EDGE,{"derivedFrom":sQuery(id+"F4.wireOp",EDGE,"E222.MirrorC")}),-1.0]])]});
            var Q210;
            Q210=makeQuery(id+"F4.imprint","IMPRINT",FACE,{"disambiguationData":[TD([[makeQuery(id+"F4.imprint","IMPRINT",EDGE,{"derivedFrom":sQuery(id+"F4.wireOp",EDGE,"E190.MirrorC")}),-1.0]])]});
            var Q211;
            Q211=makeQuery(id+"F4.imprint","IMPRINT",FACE,{"disambiguationData":[TD([[makeQuery(id+"F4.imprint","IMPRINT",EDGE,{"derivedFrom":sQuery(id+"F4.wireOp",EDGE,"E3.6.15.0")}),1.0]])]});
            var Q212;
            Q212=makeQuery(id+"F4.imprint","IMPRINT",FACE,{"disambiguationData":[TD([[makeQuery(id+"F4.imprint","IMPRINT",EDGE,{"derivedFrom":sQuery(id+"F4.wireOp",EDGE,"E5.0.11.7")}),1.0]])]});
            var Q213;
            Q213=makeQuery(id+"F4.imprint","IMPRINT",FACE,{"disambiguationData":[TD([[makeQuery(id+"F4.imprint","IMPRINT",EDGE,{"derivedFrom":sQuery(id+"F4.wireOp",EDGE,"E28.MirrorC")}),-1.0]])]});
            var Q214;
            Q214=makeQuery(id+"F4.imprint","IMPRINT",FACE,{"disambiguationData":[TD([[makeQuery(id+"F4.imprint","IMPRINT",EDGE,{"derivedFrom":sQuery(id+"F4.wireOp",EDGE,"E12.MirrorC")}),-1.0]])]});
            var Q215;
            Q215=makeQuery(id+"F4.imprint","IMPRINT",FACE,{"disambiguationData":[TD([[makeQuery(id+"F4.imprint","IMPRINT",EDGE,{"derivedFrom":sQuery(id+"F4.wireOp",EDGE,"E92.MirrorC")}),-1.0]])]});
            var Q216;
            Q216=makeQuery(id+"F4.imprint","IMPRINT",FACE,{"disambiguationData":[TD([[makeQuery(id+"F4.imprint","IMPRINT",EDGE,{"derivedFrom":sQuery(id+"F4.wireOp",EDGE,"E76.MirrorC")}),-1.0]])]});
            var Q217;
            Q217=makeQuery(id+"F4.imprint","IMPRINT",FACE,{"disambiguationData":[TD([[makeQuery(id+"F4.imprint","IMPRINT",EDGE,{"derivedFrom":sQuery(id+"F4.wireOp",EDGE,"E156.MirrorC")}),-1.0]])]});
            var Q218;
            Q218=makeQuery(id+"F4.imprint","IMPRINT",FACE,{"disambiguationData":[TD([[makeQuery(id+"F4.imprint","IMPRINT",EDGE,{"derivedFrom":sQuery(id+"F4.wireOp",EDGE,"E140.MirrorC")}),-1.0]])]});
            var Q219;
            Q219=makeQuery(id+"F4.imprint","IMPRINT",FACE,{"disambiguationData":[TD([[makeQuery(id+"F4.imprint","IMPRINT",EDGE,{"derivedFrom":sQuery(id+"F4.wireOp",EDGE,"E220.MirrorC")}),-1.0]])]});
            var Q220;
            Q220=makeQuery(id+"F4.imprint","IMPRINT",FACE,{"disambiguationData":[TD([[makeQuery(id+"F4.imprint","IMPRINT",EDGE,{"derivedFrom":sQuery(id+"F4.wireOp",EDGE,"E204.MirrorC")}),-1.0]])]});
            var Q221;
            Q221=makeQuery(id+"F4.imprint","IMPRINT",FACE,{"disambiguationData":[TD([[makeQuery(id+"F4.imprint","IMPRINT",EDGE,{"derivedFrom":sQuery(id+"F4.wireOp",EDGE,"E188.MirrorC")}),-1.0]])]});
            var Q222;
            Q222=makeQuery(id+"F4.imprint","IMPRINT",FACE,{"disambiguationData":[TD([[makeQuery(id+"F4.imprint","IMPRINT",EDGE,{"derivedFrom":sQuery(id+"F4.wireOp",EDGE,"E236.MirrorC")}),-1.0]])]});
            var Q223;
            Q223=makeQuery(id+"F4.imprint","IMPRINT",FACE,{"disambiguationData":[TD([[makeQuery(id+"F4.imprint","IMPRINT",EDGE,{"derivedFrom":sQuery(id+"F4.wireOp",EDGE,"E3.4.4.0")}),1.0]])]});
            var Q224;
            Q224=makeQuery(id+"F4.imprint","IMPRINT",FACE,{"disambiguationData":[TD([[makeQuery(id+"F4.imprint","IMPRINT",EDGE,{"derivedFrom":sQuery(id+"F4.wireOp",EDGE,"E3.3.6.0")}),1.0]])]});
            var Q225;
            Q225=makeQuery(id+"F4.imprint","IMPRINT",FACE,{"disambiguationData":[TD([[makeQuery(id+"F4.imprint","IMPRINT",EDGE,{"derivedFrom":sQuery(id+"F4.wireOp",EDGE,"E3.2.8.0")}),1.0]])]});
            var Q226;
            Q226=makeQuery(id+"F4.imprint","IMPRINT",FACE,{"disambiguationData":[TD([[makeQuery(id+"F4.imprint","IMPRINT",EDGE,{"derivedFrom":sQuery(id+"F4.wireOp",EDGE,"E3.7.14.0")}),1.0]])]});
            var Q227;
            Q227=makeQuery(id+"F4.imprint","IMPRINT",FACE,{"disambiguationData":[TD([[makeQuery(id+"F4.imprint","IMPRINT",EDGE,{"derivedFrom":sQuery(id+"F4.wireOp",EDGE,"E3.6.16.0")}),1.0]])]});
            var Q228;
            Q228=makeQuery(id+"F4.imprint","IMPRINT",FACE,{"disambiguationData":[TD([[makeQuery(id+"F4.imprint","IMPRINT",EDGE,{"derivedFrom":sQuery(id+"F4.wireOp",EDGE,"E3.6.0.0")}),1.0]])]});
            var Q229;
            Q229=makeQuery(id+"F4.imprint","IMPRINT",FACE,{"disambiguationData":[TD([[makeQuery(id+"F4.imprint","IMPRINT",EDGE,{"derivedFrom":sQuery(id+"F4.wireOp",EDGE,"E3.5.2.0")}),1.0]])]});
            var Q230;
            Q230=makeQuery(id+"F4.imprint","IMPRINT",FACE,{"disambiguationData":[TD([[makeQuery(id+"F4.imprint","IMPRINT",EDGE,{"derivedFrom":sQuery(id+"F4.wireOp",EDGE,"E5.0.10.10")}),1.0]])]});
            var Q231;
            Q231=makeQuery(id+"F4.imprint","IMPRINT",FACE,{"disambiguationData":[TD([[makeQuery(id+"F4.imprint","IMPRINT",EDGE,{"derivedFrom":sQuery(id+"F4.wireOp",EDGE,"E5.0.9.12")}),1.0]])]});
            var Q232;
            Q232=makeQuery(id+"F4.imprint","IMPRINT",FACE,{"disambiguationData":[TD([[makeQuery(id+"F4.imprint","IMPRINT",EDGE,{"derivedFrom":sQuery(id+"F4.wireOp",EDGE,"E5.0.8.14")}),1.0]])]});
            var Q233;
            Q233=makeQuery(id+"F4.imprint","IMPRINT",FACE,{"disambiguationData":[TD([[makeQuery(id+"F4.imprint","IMPRINT",EDGE,{"derivedFrom":sQuery(id+"F4.wireOp",EDGE,"E6.0.9.20")}),1.0]])]});
            var Q234;
            Q234=makeQuery(id+"F4.imprint","IMPRINT",FACE,{"disambiguationData":[TD([[makeQuery(id+"F4.imprint","IMPRINT",EDGE,{"derivedFrom":sQuery(id+"F4.wireOp",EDGE,"E6.0.5.20")}),1.0]])]});
            var Q235;
            Q235=makeQuery(id+"F4.imprint","IMPRINT",FACE,{"disambiguationData":[TD([[makeQuery(id+"F4.imprint","IMPRINT",EDGE,{"derivedFrom":sQuery(id+"F4.wireOp",EDGE,"E6.0.1.20")}),1.0]])]});
            var Q236;
            Q236=makeQuery(id+"F4.imprint","IMPRINT",FACE,{"disambiguationData":[TD([[makeQuery(id+"F4.imprint","IMPRINT",EDGE,{"derivedFrom":sQuery(id+"F4.wireOp",EDGE,"E5.0.11.8")}),1.0]])]});
            var Q237;
            Q237=makeQuery(id+"F4.imprint","IMPRINT",FACE,{"disambiguationData":[TD([[makeQuery(id+"F4.imprint","IMPRINT",EDGE,{"derivedFrom":sQuery(id+"F4.wireOp",EDGE,"E29.MirrorC")}),-1.0]])]});
            var Q238;
            Q238=makeQuery(id+"F4.imprint","IMPRINT",FACE,{"disambiguationData":[TD([[makeQuery(id+"F4.imprint","IMPRINT",EDGE,{"derivedFrom":sQuery(id+"F4.wireOp",EDGE,"E125.MirrorC")}),-1.0]])]});
            var Q239;
            Q239=makeQuery(id+"F4.imprint","IMPRINT",FACE,{"disambiguationData":[TD([[makeQuery(id+"F4.imprint","IMPRINT",EDGE,{"derivedFrom":sQuery(id+"F4.wireOp",EDGE,"E77.MirrorC")}),-1.0]])]});
            var Q240;
            Q240=makeQuery(id+"F4.imprint","IMPRINT",FACE,{"disambiguationData":[TD([[makeQuery(id+"F4.imprint","IMPRINT",EDGE,{"derivedFrom":sQuery(id+"F4.wireOp",EDGE,"E141.MirrorC")}),-1.0]])]});
            var Q241;
            Q241=makeQuery(id+"F4.imprint","IMPRINT",FACE,{"disambiguationData":[TD([[makeQuery(id+"F4.imprint","IMPRINT",EDGE,{"derivedFrom":sQuery(id+"F4.wireOp",EDGE,"E221.MirrorC")}),-1.0]])]});
            var Q242;
            Q242=makeQuery(id+"F4.imprint","IMPRINT",FACE,{"disambiguationData":[TD([[makeQuery(id+"F4.imprint","IMPRINT",EDGE,{"derivedFrom":sQuery(id+"F4.wireOp",EDGE,"E205.MirrorC")}),-1.0]])]});
            var Q243;
            Q243=makeQuery(id+"F4.imprint","IMPRINT",FACE,{"disambiguationData":[TD([[makeQuery(id+"F4.imprint","IMPRINT",EDGE,{"derivedFrom":sQuery(id+"F4.wireOp",EDGE,"E189.MirrorC")}),-1.0]])]});
            var Q244;
            Q244=makeQuery(id+"F4.imprint","IMPRINT",FACE,{"disambiguationData":[TD([[makeQuery(id+"F4.imprint","IMPRINT",EDGE,{"derivedFrom":sQuery(id+"F4.wireOp",EDGE,"E173.MirrorC")}),-1.0]])]});
            var Q245;
            Q245=makeQuery(id+"F4.imprint","IMPRINT",FACE,{"disambiguationData":[TD([[makeQuery(id+"F4.imprint","IMPRINT",EDGE,{"derivedFrom":sQuery(id+"F4.wireOp",EDGE,"E237.MirrorC")}),-1.0]])]});
            var Q246;
            Q246=makeQuery(id+"F4.imprint","IMPRINT",FACE,{"disambiguationData":[TD([[makeQuery(id+"F4.imprint","IMPRINT",EDGE,{"derivedFrom":sQuery(id+"F4.wireOp",EDGE,"E223.MirrorC")}),-1.0]])]});
            var Q247;
            Q247=makeQuery(id+"F4.imprint","IMPRINT",FACE,{"disambiguationData":[TD([[makeQuery(id+"F4.imprint","IMPRINT",EDGE,{"derivedFrom":sQuery(id+"F4.wireOp",EDGE,"E191.MirrorC")}),-1.0]])]});
            var Q248;
            Q248=makeQuery(id+"F4.imprint","IMPRINT",FACE,{"disambiguationData":[TD([[makeQuery(id+"F4.imprint","IMPRINT",EDGE,{"derivedFrom":sQuery(id+"F4.wireOp",EDGE,"E175.MirrorC")}),-1.0]])]});
            var Q249;
            Q249=makeQuery(id+"F4.imprint","IMPRINT",FACE,{"disambiguationData":[TD([[makeQuery(id+"F4.imprint","IMPRINT",EDGE,{"derivedFrom":sQuery(id+"F4.wireOp",EDGE,"E239.MirrorC")}),-1.0]])]});
            var Q250;
            Q250=makeQuery(id+"F4.imprint","IMPRINT",FACE,{"disambiguationData":[TD([[makeQuery(id+"F4.imprint","IMPRINT",EDGE,{"derivedFrom":sQuery(id+"F4.wireOp",EDGE,"E3.4.6.0")}),1.0]])]});
            var Q251;
            Q251=makeQuery(id+"F4.imprint","IMPRINT",FACE,{"disambiguationData":[TD([[makeQuery(id+"F4.imprint","IMPRINT",EDGE,{"derivedFrom":sQuery(id+"F4.wireOp",EDGE,"E3.3.8.0")}),1.0]])]});
            var Q252;
            Q252=makeQuery(id+"F4.imprint","IMPRINT",FACE,{"disambiguationData":[TD([[makeQuery(id+"F4.imprint","IMPRINT",EDGE,{"derivedFrom":sQuery(id+"F4.wireOp",EDGE,"E3.2.10.0")}),1.0]])]});
            var Q253;
            Q253=makeQuery(id+"F4.imprint","IMPRINT",FACE,{"disambiguationData":[TD([[makeQuery(id+"F4.imprint","IMPRINT",EDGE,{"derivedFrom":sQuery(id+"F4.wireOp",EDGE,"E3.1.12.0")}),1.0]])]});
            var Q254;
            Q254=makeQuery(id+"F4.imprint","IMPRINT",FACE,{"disambiguationData":[TD([[makeQuery(id+"F4.imprint","IMPRINT",EDGE,{"derivedFrom":sQuery(id+"F4.wireOp",EDGE,"E3.7.16.0")}),1.0]])]});
            var Q255;
            Q255=makeQuery(id+"F4.imprint","IMPRINT",FACE,{"disambiguationData":[TD([[makeQuery(id+"F4.imprint","IMPRINT",EDGE,{"derivedFrom":sQuery(id+"F4.wireOp",EDGE,"E3.7.0.0")}),1.0]])]});
            var Q256;
            Q256=makeQuery(id+"F4.imprint","IMPRINT",FACE,{"disambiguationData":[TD([[makeQuery(id+"F4.imprint","IMPRINT",EDGE,{"derivedFrom":sQuery(id+"F4.wireOp",EDGE,"E3.6.2.0")}),1.0]])]});
            var Q257;
            Q257=makeQuery(id+"F4.imprint","IMPRINT",FACE,{"disambiguationData":[TD([[makeQuery(id+"F4.imprint","IMPRINT",EDGE,{"derivedFrom":sQuery(id+"F4.wireOp",EDGE,"E3.5.4.0")}),1.0]])]});
            var Q258;
            Q258=makeQuery(id+"F4.imprint","IMPRINT",FACE,{"disambiguationData":[TD([[makeQuery(id+"F4.imprint","IMPRINT",EDGE,{"derivedFrom":sQuery(id+"F4.wireOp",EDGE,"E5.0.10.12")}),1.0]])]});
            var Q259;
            Q259=makeQuery(id+"F4.imprint","IMPRINT",FACE,{"disambiguationData":[TD([[makeQuery(id+"F4.imprint","IMPRINT",EDGE,{"derivedFrom":sQuery(id+"F4.wireOp",EDGE,"E5.0.9.14")}),1.0]])]});
            var Q260;
            Q260=makeQuery(id+"F4.imprint","IMPRINT",FACE,{"disambiguationData":[TD([[makeQuery(id+"F4.imprint","IMPRINT",EDGE,{"derivedFrom":sQuery(id+"F4.wireOp",EDGE,"E5.0.8.16")}),1.0]])]});
            var Q261;
            Q261=makeQuery(id+"F4.imprint","IMPRINT",FACE,{"disambiguationData":[TD([[makeQuery(id+"F4.imprint","IMPRINT",EDGE,{"derivedFrom":sQuery(id+"F4.wireOp",EDGE,"E5.0.8.0")}),1.0]])]});
            var Q262;
            Q262=makeQuery(id+"F4.imprint","IMPRINT",FACE,{"disambiguationData":[TD([[makeQuery(id+"F4.imprint","IMPRINT",EDGE,{"derivedFrom":sQuery(id+"F4.wireOp",EDGE,"E6.0.10.18")}),1.0]])]});
            var Q263;
            Q263=makeQuery(id+"F4.imprint","IMPRINT",FACE,{"disambiguationData":[TD([[makeQuery(id+"F4.imprint","IMPRINT",EDGE,{"derivedFrom":sQuery(id+"F4.wireOp",EDGE,"E6.0.6.18")}),1.0]])]});
            var Q264;
            Q264=makeQuery(id+"F4.imprint","IMPRINT",FACE,{"disambiguationData":[TD([[makeQuery(id+"F4.imprint","IMPRINT",EDGE,{"derivedFrom":sQuery(id+"F4.wireOp",EDGE,"E6.0.2.18")}),1.0]])]});
            var Q265;
            Q265=makeQuery(id+"F4.imprint","IMPRINT",FACE,{"disambiguationData":[TD([[makeQuery(id+"F4.imprint","IMPRINT",EDGE,{"derivedFrom":sQuery(id+"F4.wireOp",EDGE,"E5.0.11.10")}),1.0]])]});
            var Q266;
            Q266=makeQuery(id+"F4.imprint","IMPRINT",FACE,{"disambiguationData":[TD([[makeQuery(id+"F4.imprint","IMPRINT",EDGE,{"derivedFrom":sQuery(id+"F4.wireOp",EDGE,"E63.MirrorC")}),-1.0]])]});
            var Q267;
            Q267=makeQuery(id+"F4.imprint","IMPRINT",FACE,{"disambiguationData":[TD([[makeQuery(id+"F4.imprint","IMPRINT",EDGE,{"derivedFrom":sQuery(id+"F4.wireOp",EDGE,"E47.MirrorC")}),-1.0]])]});
            var Q268;
            Q268=makeQuery(id+"F4.imprint","IMPRINT",FACE,{"disambiguationData":[TD([[makeQuery(id+"F4.imprint","IMPRINT",EDGE,{"derivedFrom":sQuery(id+"F4.wireOp",EDGE,"E15.MirrorC")}),-1.0]])]});
            var Q269;
            Q269=makeQuery(id+"F4.imprint","IMPRINT",FACE,{"disambiguationData":[TD([[makeQuery(id+"F4.imprint","IMPRINT",EDGE,{"derivedFrom":sQuery(id+"F4.wireOp",EDGE,"E79.MirrorC")}),-1.0]])]});
            var Q270;
            Q270=makeQuery(id+"F4.imprint","IMPRINT",FACE,{"disambiguationData":[TD([[makeQuery(id+"F4.imprint","IMPRINT",EDGE,{"derivedFrom":sQuery(id+"F4.wireOp",EDGE,"E143.MirrorC")}),-1.0]])]});
            var Q271;
            Q271=makeQuery(id+"F4.imprint","IMPRINT",FACE,{"disambiguationData":[TD([[makeQuery(id+"F4.imprint","IMPRINT",EDGE,{"derivedFrom":sQuery(id+"F4.wireOp",EDGE,"E224.MirrorC")}),-1.0]])]});
            var Q272;
            Q272=makeQuery(id+"F4.imprint","IMPRINT",FACE,{"disambiguationData":[TD([[makeQuery(id+"F4.imprint","IMPRINT",EDGE,{"derivedFrom":sQuery(id+"F4.wireOp",EDGE,"E3.6.3.0")}),1.0]])]});
            var Q273;
            Q273=makeQuery(id+"F4.imprint","IMPRINT",FACE,{"disambiguationData":[TD([[makeQuery(id+"F4.imprint","IMPRINT",EDGE,{"derivedFrom":sQuery(id+"F4.wireOp",EDGE,"E6.0.6.19")}),1.0]])]});
            var Q274;
            Q274=makeQuery(id+"F4.imprint","IMPRINT",FACE,{"disambiguationData":[TD([[makeQuery(id+"F4.imprint","IMPRINT",EDGE,{"derivedFrom":sQuery(id+"F4.wireOp",EDGE,"E5.0.11.11")}),1.0]])]});
            var Q275;
            Q275=makeQuery(id+"F4.imprint","IMPRINT",FACE,{"disambiguationData":[TD([[makeQuery(id+"F4.imprint","IMPRINT",EDGE,{"derivedFrom":sQuery(id+"F4.wireOp",EDGE,"E48.MirrorC")}),-1.0]])]});
            var Q276;
            Q276=makeQuery(id+"F4.imprint","IMPRINT",FACE,{"disambiguationData":[TD([[makeQuery(id+"F4.imprint","IMPRINT",EDGE,{"derivedFrom":sQuery(id+"F4.wireOp",EDGE,"E32.MirrorC")}),-1.0]])]});
            var Q277;
            Q277=makeQuery(id+"F4.imprint","IMPRINT",FACE,{"disambiguationData":[TD([[makeQuery(id+"F4.imprint","IMPRINT",EDGE,{"derivedFrom":sQuery(id+"F4.wireOp",EDGE,"E16.MirrorC")}),-1.0]])]});
            var Q278;
            Q278=makeQuery(id+"F4.imprint","IMPRINT",FACE,{"disambiguationData":[TD([[makeQuery(id+"F4.imprint","IMPRINT",EDGE,{"derivedFrom":sQuery(id+"F4.wireOp",EDGE,"E112.MirrorC")}),-1.0]])]});
            var Q279;
            Q279=makeQuery(id+"F4.imprint","IMPRINT",FACE,{"disambiguationData":[TD([[makeQuery(id+"F4.imprint","IMPRINT",EDGE,{"derivedFrom":sQuery(id+"F4.wireOp",EDGE,"E3.4.8.0")}),1.0]])]});
            var Q280;
            Q280=makeQuery(id+"F4.imprint","IMPRINT",FACE,{"disambiguationData":[TD([[makeQuery(id+"F4.imprint","IMPRINT",EDGE,{"derivedFrom":sQuery(id+"F4.wireOp",EDGE,"E3.3.10.0")}),1.0]])]});
            var Q281;
            Q281=makeQuery(id+"F4.imprint","IMPRINT",FACE,{"disambiguationData":[TD([[makeQuery(id+"F4.imprint","IMPRINT",EDGE,{"derivedFrom":sQuery(id+"F4.wireOp",EDGE,"E3.2.12.0")}),1.0]])]});
            var Q282;
            Q282=makeQuery(id+"F4.imprint","IMPRINT",FACE,{"disambiguationData":[TD([[makeQuery(id+"F4.imprint","IMPRINT",EDGE,{"derivedFrom":sQuery(id+"F4.wireOp",EDGE,"E3.1.14.0")}),1.0]])]});
            var Q283;
            Q283=makeQuery(id+"F4.imprint","IMPRINT",FACE,{"disambiguationData":[TD([[makeQuery(id+"F4.imprint","IMPRINT",EDGE,{"derivedFrom":sQuery(id+"F4.wireOp",EDGE,"E3.7.2.0")}),1.0]])]});
            var Q284;
            Q284=makeQuery(id+"F4.imprint","IMPRINT",FACE,{"disambiguationData":[TD([[makeQuery(id+"F4.imprint","IMPRINT",EDGE,{"derivedFrom":sQuery(id+"F4.wireOp",EDGE,"E3.6.4.0")}),1.0]])]});
            var Q285;
            Q285=makeQuery(id+"F4.imprint","IMPRINT",FACE,{"disambiguationData":[TD([[makeQuery(id+"F4.imprint","IMPRINT",EDGE,{"derivedFrom":sQuery(id+"F4.wireOp",EDGE,"E3.5.6.0")}),1.0]])]});
            var Q286;
            Q286=makeQuery(id+"F4.imprint","IMPRINT",FACE,{"disambiguationData":[TD([[makeQuery(id+"F4.imprint","IMPRINT",EDGE,{"derivedFrom":sQuery(id+"F4.wireOp",EDGE,"E5.0.10.14")}),1.0]])]});
            var Q287;
            Q287=makeQuery(id+"F4.imprint","IMPRINT",FACE,{"disambiguationData":[TD([[makeQuery(id+"F4.imprint","IMPRINT",EDGE,{"derivedFrom":sQuery(id+"F4.wireOp",EDGE,"E5.0.9.16")}),1.0]])]});
            var Q288;
            Q288=makeQuery(id+"F4.imprint","IMPRINT",FACE,{"disambiguationData":[TD([[makeQuery(id+"F4.imprint","IMPRINT",EDGE,{"derivedFrom":sQuery(id+"F4.wireOp",EDGE,"E5.0.9.0")}),1.0]])]});
            var Q289;
            Q289=makeQuery(id+"F4.imprint","IMPRINT",FACE,{"disambiguationData":[TD([[makeQuery(id+"F4.imprint","IMPRINT",EDGE,{"derivedFrom":sQuery(id+"F4.wireOp",EDGE,"E5.0.8.2")}),1.0]])]});
            var Q290;
            Q290=makeQuery(id+"F4.imprint","IMPRINT",FACE,{"disambiguationData":[TD([[makeQuery(id+"F4.imprint","IMPRINT",EDGE,{"derivedFrom":sQuery(id+"F4.wireOp",EDGE,"E6.0.10.20")}),1.0]])]});
            var Q291;
            Q291=makeQuery(id+"F4.imprint","IMPRINT",FACE,{"disambiguationData":[TD([[makeQuery(id+"F4.imprint","IMPRINT",EDGE,{"derivedFrom":sQuery(id+"F4.wireOp",EDGE,"E6.0.6.20")}),1.0]])]});
            var Q292;
            Q292=makeQuery(id+"F4.imprint","IMPRINT",FACE,{"disambiguationData":[TD([[makeQuery(id+"F4.imprint","IMPRINT",EDGE,{"derivedFrom":sQuery(id+"F4.wireOp",EDGE,"E6.0.2.20")}),1.0]])]});
            var Q293;
            Q293=makeQuery(id+"F4.imprint","IMPRINT",FACE,{"disambiguationData":[TD([[makeQuery(id+"F4.imprint","IMPRINT",EDGE,{"derivedFrom":sQuery(id+"F4.wireOp",EDGE,"E5.0.11.12")}),1.0]])]});
            var Q294;
            Q294=makeQuery(id+"F4.imprint","IMPRINT",FACE,{"disambiguationData":[TD([[makeQuery(id+"F4.imprint","IMPRINT",EDGE,{"derivedFrom":sQuery(id+"F4.wireOp",EDGE,"E65.MirrorC")}),-1.0]])]});
            var Q295;
            Q295=makeQuery(id+"F4.imprint","IMPRINT",FACE,{"disambiguationData":[TD([[makeQuery(id+"F4.imprint","IMPRINT",EDGE,{"derivedFrom":sQuery(id+"F4.wireOp",EDGE,"E49.MirrorC")}),-1.0]])]});
            var Q296;
            Q296=makeQuery(id+"F4.imprint","IMPRINT",FACE,{"disambiguationData":[TD([[makeQuery(id+"F4.imprint","IMPRINT",EDGE,{"derivedFrom":sQuery(id+"F4.wireOp",EDGE,"E33.MirrorC")}),-1.0]])]});
            var Q297;
            Q297=makeQuery(id+"F4.imprint","IMPRINT",FACE,{"disambiguationData":[TD([[makeQuery(id+"F4.imprint","IMPRINT",EDGE,{"derivedFrom":sQuery(id+"F4.wireOp",EDGE,"E97.MirrorC")}),-1.0]])]});
            var Q298;
            Q298=makeQuery(id+"F4.imprint","IMPRINT",FACE,{"disambiguationData":[TD([[makeQuery(id+"F4.imprint","IMPRINT",EDGE,{"derivedFrom":sQuery(id+"F4.wireOp",EDGE,"E145.MirrorC")}),-1.0]])]});
            var Q299;
            Q299=makeQuery(id+"F4.imprint","IMPRINT",FACE,{"disambiguationData":[TD([[makeQuery(id+"F4.imprint","IMPRINT",EDGE,{"derivedFrom":sQuery(id+"F4.wireOp",EDGE,"E161.MirrorC")}),-1.0]])]});
            var Q300;
            Q300=makeQuery(id+"F4.imprint","IMPRINT",FACE,{"disambiguationData":[TD([[makeQuery(id+"F4.imprint","IMPRINT",EDGE,{"derivedFrom":sQuery(id+"F4.wireOp",EDGE,"E225.MirrorC")}),-1.0]])]});
            var Q301;
            Q301=makeQuery(id+"F4.imprint","IMPRINT",FACE,{"disambiguationData":[TD([[makeQuery(id+"F4.imprint","IMPRINT",EDGE,{"derivedFrom":sQuery(id+"F4.wireOp",EDGE,"E177.MirrorC")}),-1.0]])]});
            var Q302;
            Q302=makeQuery(id+"F4.imprint","IMPRINT",FACE,{"disambiguationData":[TD([[makeQuery(id+"F4.imprint","IMPRINT",EDGE,{"derivedFrom":sQuery(id+"F4.wireOp",EDGE,"E3.6.5.0")}),1.0]])]});
            var Q303;
            Q303=makeQuery(id+"F4.imprint","IMPRINT",FACE,{"disambiguationData":[TD([[makeQuery(id+"F4.imprint","IMPRINT",EDGE,{"derivedFrom":sQuery(id+"F4.wireOp",EDGE,"E6.0.6.21")}),1.0]])]});
            var Q304;
            Q304=makeQuery(id+"F4.imprint","IMPRINT",FACE,{"disambiguationData":[TD([[makeQuery(id+"F4.imprint","IMPRINT",EDGE,{"derivedFrom":sQuery(id+"F4.wireOp",EDGE,"E5.0.11.13")}),1.0]])]});
            var Q305;
            Q305=makeQuery(id+"F4.imprint","IMPRINT",FACE,{"disambiguationData":[TD([[makeQuery(id+"F4.imprint","IMPRINT",EDGE,{"derivedFrom":sQuery(id+"F4.wireOp",EDGE,"E66.MirrorC")}),-1.0]])]});
            var Q306;
            Q306=makeQuery(id+"F4.imprint","IMPRINT",FACE,{"disambiguationData":[TD([[makeQuery(id+"F4.imprint","IMPRINT",EDGE,{"derivedFrom":sQuery(id+"F4.wireOp",EDGE,"E50.MirrorC")}),-1.0]])]});
            var Q307;
            Q307=makeQuery(id+"F4.imprint","IMPRINT",FACE,{"disambiguationData":[TD([[makeQuery(id+"F4.imprint","IMPRINT",EDGE,{"derivedFrom":sQuery(id+"F4.wireOp",EDGE,"E34.MirrorC")}),-1.0]])]});
            var Q308;
            Q308=makeQuery(id+"F4.imprint","IMPRINT",FACE,{"disambiguationData":[TD([[makeQuery(id+"F4.imprint","IMPRINT",EDGE,{"derivedFrom":sQuery(id+"F4.wireOp",EDGE,"E98.MirrorC")}),-1.0]])]});
            var Q309;
            Q309=makeQuery(id+"F4.imprint","IMPRINT",FACE,{"disambiguationData":[TD([[makeQuery(id+"F4.imprint","IMPRINT",EDGE,{"derivedFrom":sQuery(id+"F4.wireOp",EDGE,"E146.MirrorC")}),-1.0]])]});
            var Q310;
            Q310=makeQuery(id+"F4.imprint","IMPRINT",FACE,{"disambiguationData":[TD([[makeQuery(id+"F4.imprint","IMPRINT",EDGE,{"derivedFrom":sQuery(id+"F4.wireOp",EDGE,"E162.MirrorC")}),-1.0]])]});
            var Q311;
            Q311=makeQuery(id+"F4.imprint","IMPRINT",FACE,{"disambiguationData":[TD([[makeQuery(id+"F4.imprint","IMPRINT",EDGE,{"derivedFrom":sQuery(id+"F4.wireOp",EDGE,"E226.MirrorC")}),-1.0]])]});
            var Q312;
            Q312=makeQuery(id+"F4.imprint","IMPRINT",FACE,{"disambiguationData":[TD([[makeQuery(id+"F4.imprint","IMPRINT",EDGE,{"derivedFrom":sQuery(id+"F4.wireOp",EDGE,"E210.MirrorC")}),-1.0]])]});
            var Q313;
            Q313=makeQuery(id+"F4.imprint","IMPRINT",FACE,{"disambiguationData":[TD([[makeQuery(id+"F4.imprint","IMPRINT",EDGE,{"derivedFrom":sQuery(id+"F4.wireOp",EDGE,"E178.MirrorC")}),-1.0]])]});
            var Q314;
            Q314=makeQuery(id+"F4.imprint","IMPRINT",FACE,{"disambiguationData":[TD([[makeQuery(id+"F4.imprint","IMPRINT",EDGE,{"derivedFrom":sQuery(id+"F4.wireOp",EDGE,"E242.MirrorC")}),-1.0]])]});
            var Q315;
            Q315=makeQuery(id+"F4.imprint","IMPRINT",FACE,{"disambiguationData":[TD([[makeQuery(id+"F4.imprint","IMPRINT",EDGE,{"derivedFrom":sQuery(id+"F4.wireOp",EDGE,"E3.4.10.0")}),1.0]])]});
            var Q316;
            Q316=makeQuery(id+"F4.imprint","IMPRINT",FACE,{"disambiguationData":[TD([[makeQuery(id+"F4.imprint","IMPRINT",EDGE,{"derivedFrom":sQuery(id+"F4.wireOp",EDGE,"E3.3.12.0")}),1.0]])]});
            var Q317;
            Q317=makeQuery(id+"F4.imprint","IMPRINT",FACE,{"disambiguationData":[TD([[makeQuery(id+"F4.imprint","IMPRINT",EDGE,{"derivedFrom":sQuery(id+"F4.wireOp",EDGE,"E3.2.14.0")}),1.0]])]});
            var Q318;
            Q318=makeQuery(id+"F4.imprint","IMPRINT",FACE,{"disambiguationData":[TD([[makeQuery(id+"F4.imprint","IMPRINT",EDGE,{"derivedFrom":sQuery(id+"F4.wireOp",EDGE,"E3.1.16.0")}),1.0]])]});
            var Q319;
            Q319=makeQuery(id+"F4.imprint","IMPRINT",FACE,{"disambiguationData":[TD([[makeQuery(id+"F4.imprint","IMPRINT",EDGE,{"derivedFrom":sQuery(id+"F4.wireOp",EDGE,"E3.7.4.0")}),1.0]])]});
            var Q320;
            Q320=makeQuery(id+"F4.imprint","IMPRINT",FACE,{"disambiguationData":[TD([[makeQuery(id+"F4.imprint","IMPRINT",EDGE,{"derivedFrom":sQuery(id+"F4.wireOp",EDGE,"E3.6.6.0")}),1.0]])]});
            var Q321;
            Q321=makeQuery(id+"F4.imprint","IMPRINT",FACE,{"disambiguationData":[TD([[makeQuery(id+"F4.imprint","IMPRINT",EDGE,{"derivedFrom":sQuery(id+"F4.wireOp",EDGE,"E3.5.8.0")}),1.0]])]});
            var Q322;
            Q322=makeQuery(id+"F4.imprint","IMPRINT",FACE,{"disambiguationData":[TD([[makeQuery(id+"F4.imprint","IMPRINT",EDGE,{"derivedFrom":sQuery(id+"F4.wireOp",EDGE,"E5.0.10.16")}),1.0]])]});
            var Q323;
            Q323=makeQuery(id+"F4.imprint","IMPRINT",FACE,{"disambiguationData":[TD([[makeQuery(id+"F4.imprint","IMPRINT",EDGE,{"derivedFrom":sQuery(id+"F4.wireOp",EDGE,"E5.0.10.0")}),1.0]])]});
            var Q324;
            Q324=makeQuery(id+"F4.imprint","IMPRINT",FACE,{"disambiguationData":[TD([[makeQuery(id+"F4.imprint","IMPRINT",EDGE,{"derivedFrom":sQuery(id+"F4.wireOp",EDGE,"E5.0.9.2")}),1.0]])]});
            var Q325;
            Q325=makeQuery(id+"F4.imprint","IMPRINT",FACE,{"disambiguationData":[TD([[makeQuery(id+"F4.imprint","IMPRINT",EDGE,{"derivedFrom":sQuery(id+"F4.wireOp",EDGE,"E5.0.8.4")}),1.0]])]});
            var Q326;
            Q326=makeQuery(id+"F4.imprint","IMPRINT",FACE,{"disambiguationData":[TD([[makeQuery(id+"F4.imprint","IMPRINT",EDGE,{"derivedFrom":sQuery(id+"F4.wireOp",EDGE,"E6.0.11.18")}),1.0]])]});
            var Q327;
            Q327=makeQuery(id+"F4.imprint","IMPRINT",FACE,{"disambiguationData":[TD([[makeQuery(id+"F4.imprint","IMPRINT",EDGE,{"derivedFrom":sQuery(id+"F4.wireOp",EDGE,"E6.0.7.18")}),1.0]])]});
            var Q328;
            Q328=makeQuery(id+"F4.imprint","IMPRINT",FACE,{"disambiguationData":[TD([[makeQuery(id+"F4.imprint","IMPRINT",EDGE,{"derivedFrom":sQuery(id+"F4.wireOp",EDGE,"E6.0.3.18")}),1.0]])]});
            var Q329;
            Q329=makeQuery(id+"F4.imprint","IMPRINT",FACE,{"disambiguationData":[TD([[makeQuery(id+"F4.imprint","IMPRINT",EDGE,{"derivedFrom":sQuery(id+"F4.wireOp",EDGE,"E5.0.11.14")}),1.0]])]});
            var Q330;
            Q330=makeQuery(id+"F4.imprint","IMPRINT",FACE,{"disambiguationData":[TD([[makeQuery(id+"F4.imprint","IMPRINT",EDGE,{"derivedFrom":sQuery(id+"F4.wireOp",EDGE,"E51.MirrorC")}),-1.0]])]});
            var Q331;
            Q331=makeQuery(id+"F4.imprint","IMPRINT",FACE,{"disambiguationData":[TD([[makeQuery(id+"F4.imprint","IMPRINT",EDGE,{"derivedFrom":sQuery(id+"F4.wireOp",EDGE,"E35.MirrorC")}),-1.0]])]});
            var Q332;
            Q332=makeQuery(id+"F4.imprint","IMPRINT",FACE,{"disambiguationData":[TD([[makeQuery(id+"F4.imprint","IMPRINT",EDGE,{"derivedFrom":sQuery(id+"F4.wireOp",EDGE,"E19.MirrorC")}),-1.0]])]});
            var Q333;
            Q333=makeQuery(id+"F4.imprint","IMPRINT",FACE,{"disambiguationData":[TD([[makeQuery(id+"F4.imprint","IMPRINT",EDGE,{"derivedFrom":sQuery(id+"F4.wireOp",EDGE,"E131.MirrorC")}),-1.0]])]});
            var Q334;
            Q334=makeQuery(id+"F4.imprint","IMPRINT",FACE,{"disambiguationData":[TD([[makeQuery(id+"F4.imprint","IMPRINT",EDGE,{"derivedFrom":sQuery(id+"F4.wireOp",EDGE,"E83.MirrorC")}),-1.0]])]});
            var Q335;
            Q335=makeQuery(id+"F4.imprint","IMPRINT",FACE,{"disambiguationData":[TD([[makeQuery(id+"F4.imprint","IMPRINT",EDGE,{"derivedFrom":sQuery(id+"F4.wireOp",EDGE,"E147.MirrorC")}),-1.0]])]});
            var Q336;
            Q336=makeQuery(id+"F4.imprint","IMPRINT",FACE,{"disambiguationData":[TD([[makeQuery(id+"F4.imprint","IMPRINT",EDGE,{"derivedFrom":sQuery(id+"F4.wireOp",EDGE,"E163.MirrorC")}),-1.0]])]});
            var Q337;
            Q337=makeQuery(id+"F4.imprint","IMPRINT",FACE,{"disambiguationData":[TD([[makeQuery(id+"F4.imprint","IMPRINT",EDGE,{"derivedFrom":sQuery(id+"F4.wireOp",EDGE,"E195.MirrorC")}),-1.0]])]});
            var Q338;
            Q338=makeQuery(id+"F4.imprint","IMPRINT",FACE,{"disambiguationData":[TD([[makeQuery(id+"F4.imprint","IMPRINT",EDGE,{"derivedFrom":sQuery(id+"F4.wireOp",EDGE,"E179.MirrorC")}),-1.0]])]});
            var Q339;
            Q339=makeQuery(id+"F4.imprint","IMPRINT",FACE,{"disambiguationData":[TD([[makeQuery(id+"F4.imprint","IMPRINT",EDGE,{"derivedFrom":sQuery(id+"F4.wireOp",EDGE,"E243.MirrorC")}),-1.0]])]});
            var Q340;
            Q340=makeQuery(id+"F4.imprint","IMPRINT",FACE,{"disambiguationData":[TD([[makeQuery(id+"F4.imprint","IMPRINT",EDGE,{"derivedFrom":sQuery(id+"F4.wireOp",EDGE,"E3.6.7.0")}),1.0]])]});
            var Q341;
            Q341=makeQuery(id+"F4.imprint","IMPRINT",FACE,{"disambiguationData":[TD([[makeQuery(id+"F4.imprint","IMPRINT",EDGE,{"derivedFrom":sQuery(id+"F4.wireOp",EDGE,"E6.0.11.19")}),1.0]])]});
            var Q342;
            Q342=makeQuery(id+"F4.imprint","IMPRINT",FACE,{"disambiguationData":[TD([[makeQuery(id+"F4.imprint","IMPRINT",EDGE,{"derivedFrom":sQuery(id+"F4.wireOp",EDGE,"E5.0.11.15")}),1.0]])]});
            var Q343;
            Q343=makeQuery(id+"F4.imprint","IMPRINT",FACE,{"disambiguationData":[TD([[makeQuery(id+"F4.imprint","IMPRINT",EDGE,{"derivedFrom":sQuery(id+"F4.wireOp",EDGE,"E20.MirrorC")}),-1.0]])]});
            var Q344;
            Q344=makeQuery(id+"F4.imprint","IMPRINT",FACE,{"disambiguationData":[TD([[makeQuery(id+"F4.imprint","IMPRINT",EDGE,{"derivedFrom":sQuery(id+"F4.wireOp",EDGE,"E132.MirrorC")}),-1.0]])]});
            var Q345;
            Q345=makeQuery(id+"F4.imprint","IMPRINT",FACE,{"disambiguationData":[TD([[makeQuery(id+"F4.imprint","IMPRINT",EDGE,{"derivedFrom":sQuery(id+"F4.wireOp",EDGE,"E84.MirrorC")}),-1.0]])]});
            var Q346;
            Q346=makeQuery(id+"F4.imprint","IMPRINT",FACE,{"disambiguationData":[TD([[makeQuery(id+"F4.imprint","IMPRINT",EDGE,{"derivedFrom":sQuery(id+"F4.wireOp",EDGE,"E148.MirrorC")}),-1.0]])]});
            var Q347;
            Q347=makeQuery(id+"F4.imprint","IMPRINT",FACE,{"disambiguationData":[TD([[makeQuery(id+"F4.imprint","IMPRINT",EDGE,{"derivedFrom":sQuery(id+"F4.wireOp",EDGE,"E164.MirrorC")}),-1.0]])]});
            var Q348;
            Q348=makeQuery(id+"F4.imprint","IMPRINT",FACE,{"disambiguationData":[TD([[makeQuery(id+"F4.imprint","IMPRINT",EDGE,{"derivedFrom":sQuery(id+"F4.wireOp",EDGE,"E196.MirrorC")}),-1.0]])]});
            var Q349;
            Q349=makeQuery(id+"F4.imprint","IMPRINT",FACE,{"disambiguationData":[TD([[makeQuery(id+"F4.imprint","IMPRINT",EDGE,{"derivedFrom":sQuery(id+"F4.wireOp",EDGE,"E180.MirrorC")}),-1.0]])]});
            var Q350;
            Q350=makeQuery(id+"F4.imprint","IMPRINT",FACE,{"disambiguationData":[TD([[makeQuery(id+"F4.imprint","IMPRINT",EDGE,{"derivedFrom":sQuery(id+"F4.wireOp",EDGE,"E244.MirrorC")}),-1.0]])]});
            var Q351;
            Q351=makeQuery(id+"F4.imprint","IMPRINT",FACE,{"disambiguationData":[TD([[makeQuery(id+"F4.imprint","IMPRINT",EDGE,{"derivedFrom":sQuery(id+"F4.wireOp",EDGE,"E3.2.16.0")}),1.0]])]});
            var Q352;
            Q352=makeQuery(id+"F4.imprint","IMPRINT",FACE,{"disambiguationData":[TD([[makeQuery(id+"F4.imprint","IMPRINT",EDGE,{"derivedFrom":sQuery(id+"F4.wireOp",EDGE,"E3.2.0.0")}),1.0]])]});
            var Q353;
            Q353=makeQuery(id+"F4.imprint","IMPRINT",FACE,{"disambiguationData":[TD([[makeQuery(id+"F4.imprint","IMPRINT",EDGE,{"derivedFrom":sQuery(id+"F4.wireOp",EDGE,"E3.6.8.0")}),1.0]])]});
            var Q354;
            Q354=makeQuery(id+"F4.imprint","IMPRINT",FACE,{"disambiguationData":[TD([[makeQuery(id+"F4.imprint","IMPRINT",EDGE,{"derivedFrom":sQuery(id+"F4.wireOp",EDGE,"E3.5.10.0")}),1.0]])]});
            var Q355;
            Q355=makeQuery(id+"F4.imprint","IMPRINT",FACE,{"disambiguationData":[TD([[makeQuery(id+"F4.imprint","IMPRINT",EDGE,{"derivedFrom":sQuery(id+"F4.wireOp",EDGE,"E3.4.12.0")}),1.0]])]});
            var Q356;
            Q356=makeQuery(id+"F4.imprint","IMPRINT",FACE,{"disambiguationData":[TD([[makeQuery(id+"F4.imprint","IMPRINT",EDGE,{"derivedFrom":sQuery(id+"F4.wireOp",EDGE,"E3.3.14.0")}),1.0]])]});
            var Q357;
            Q357=makeQuery(id+"F4.imprint","IMPRINT",FACE,{"disambiguationData":[TD([[makeQuery(id+"F4.imprint","IMPRINT",EDGE,{"derivedFrom":sQuery(id+"F4.wireOp",EDGE,"E5.0.9.4")}),1.0]])]});
            var Q358;
            Q358=makeQuery(id+"F4.imprint","IMPRINT",FACE,{"disambiguationData":[TD([[makeQuery(id+"F4.imprint","IMPRINT",EDGE,{"derivedFrom":sQuery(id+"F4.wireOp",EDGE,"E5.0.8.6")}),1.0]])]});
            var Q359;
            Q359=makeQuery(id+"F4.imprint","IMPRINT",FACE,{"disambiguationData":[TD([[makeQuery(id+"F4.imprint","IMPRINT",EDGE,{"derivedFrom":sQuery(id+"F4.wireOp",EDGE,"E3.7.6.0")}),1.0]])]});
            var Q360;
            Q360=makeQuery(id+"F4.imprint","IMPRINT",FACE,{"disambiguationData":[TD([[makeQuery(id+"F4.imprint","IMPRINT",EDGE,{"derivedFrom":sQuery(id+"F4.wireOp",EDGE,"E6.0.3.20")}),1.0]])]});
            var Q361;
            Q361=makeQuery(id+"F4.imprint","IMPRINT",FACE,{"disambiguationData":[TD([[makeQuery(id+"F4.imprint","IMPRINT",EDGE,{"derivedFrom":sQuery(id+"F4.wireOp",EDGE,"E5.0.11.16")}),1.0]])]});
            var Q362;
            Q362=makeQuery(id+"F4.imprint","IMPRINT",FACE,{"disambiguationData":[TD([[makeQuery(id+"F4.imprint","IMPRINT",EDGE,{"derivedFrom":sQuery(id+"F4.wireOp",EDGE,"E5.0.11.0")}),1.0]])]});
            var Q363;
            Q363=makeQuery(id+"F4.imprint","IMPRINT",FACE,{"disambiguationData":[TD([[makeQuery(id+"F4.imprint","IMPRINT",EDGE,{"derivedFrom":sQuery(id+"F4.wireOp",EDGE,"E5.0.10.2")}),1.0]])]});
            var Q364;
            Q364=makeQuery(id+"F4.imprint","IMPRINT",FACE,{"disambiguationData":[TD([[makeQuery(id+"F4.imprint","IMPRINT",EDGE,{"derivedFrom":sQuery(id+"F4.wireOp",EDGE,"E37.MirrorC")}),-1.0]])]});
            var Q365;
            Q365=makeQuery(id+"F4.imprint","IMPRINT",FACE,{"disambiguationData":[TD([[makeQuery(id+"F4.imprint","IMPRINT",EDGE,{"derivedFrom":sQuery(id+"F4.wireOp",EDGE,"E21.MirrorC")}),-1.0]])]});
            var Q366;
            Q366=makeQuery(id+"F4.imprint","IMPRINT",FACE,{"disambiguationData":[TD([[makeQuery(id+"F4.imprint","IMPRINT",EDGE,{"derivedFrom":sQuery(id+"F4.wireOp",EDGE,"E6.0.11.20")}),1.0]])]});
            var Q367;
            Q367=makeQuery(id+"F4.imprint","IMPRINT",FACE,{"disambiguationData":[TD([[makeQuery(id+"F4.imprint","IMPRINT",EDGE,{"derivedFrom":sQuery(id+"F4.wireOp",EDGE,"E6.0.7.20")}),1.0]])]});
            var Q368;
            Q368=makeQuery(id+"F4.imprint","IMPRINT",FACE,{"disambiguationData":[TD([[makeQuery(id+"F4.imprint","IMPRINT",EDGE,{"derivedFrom":sQuery(id+"F4.wireOp",EDGE,"E85.MirrorC")}),-1.0]])]});
            var Q369;
            Q369=makeQuery(id+"F4.imprint","IMPRINT",FACE,{"disambiguationData":[TD([[makeQuery(id+"F4.imprint","IMPRINT",EDGE,{"derivedFrom":sQuery(id+"F4.wireOp",EDGE,"E69.MirrorC")}),-1.0]])]});
            var Q370;
            Q370=makeQuery(id+"F4.imprint","IMPRINT",FACE,{"disambiguationData":[TD([[makeQuery(id+"F4.imprint","IMPRINT",EDGE,{"derivedFrom":sQuery(id+"F4.wireOp",EDGE,"E149.MirrorC")}),-1.0]])]});
            var Q371;
            Q371=makeQuery(id+"F4.imprint","IMPRINT",FACE,{"disambiguationData":[TD([[makeQuery(id+"F4.imprint","IMPRINT",EDGE,{"derivedFrom":sQuery(id+"F4.wireOp",EDGE,"E133.MirrorC")}),-1.0]])]});
            var Q372;
            Q372=makeQuery(id+"F4.imprint","IMPRINT",FACE,{"disambiguationData":[TD([[makeQuery(id+"F4.imprint","IMPRINT",EDGE,{"derivedFrom":sQuery(id+"F4.wireOp",EDGE,"E197.MirrorC")}),-1.0]])]});
            var Q373;
            Q373=makeQuery(id+"F4.imprint","IMPRINT",FACE,{"disambiguationData":[TD([[makeQuery(id+"F4.imprint","IMPRINT",EDGE,{"derivedFrom":sQuery(id+"F4.wireOp",EDGE,"E165.MirrorC")}),-1.0]])]});
            var Q374;
            Q374=makeQuery(id+"F4.imprint","IMPRINT",FACE,{"disambiguationData":[TD([[makeQuery(id+"F4.imprint","IMPRINT",EDGE,{"derivedFrom":sQuery(id+"F4.wireOp",EDGE,"E229.MirrorC")}),-1.0]])]});
            var Q375;
            Q375=makeQuery(id+"F4.imprint","IMPRINT",FACE,{"disambiguationData":[TD([[makeQuery(id+"F4.imprint","IMPRINT",EDGE,{"derivedFrom":sQuery(id+"F4.wireOp",EDGE,"E213.MirrorC")}),-1.0]])]});
            var Q376;
            Q376=makeQuery(id+"F4.imprint","IMPRINT",FACE,{"disambiguationData":[TD([[makeQuery(id+"F4.imprint","IMPRINT",EDGE,{"derivedFrom":sQuery(id+"F4.wireOp",EDGE,"E3.6.9.0")}),1.0]])]});
            var Q377;
            Q377=makeQuery(id+"F4.imprint","IMPRINT",FACE,{"disambiguationData":[TD([[makeQuery(id+"F4.imprint","IMPRINT",EDGE,{"derivedFrom":sQuery(id+"F4.wireOp",EDGE,"E5.0.11.17")}),1.0]])]});
            var Q378;
            Q378=makeQuery(id+"F4.imprint","IMPRINT",FACE,{"disambiguationData":[TD([[makeQuery(id+"F4.imprint","IMPRINT",EDGE,{"derivedFrom":sQuery(id+"F4.wireOp",EDGE,"E5.0.11.1")}),1.0]])]});
            var Q379;
            Q379=makeQuery(id+"F4.imprint","IMPRINT",FACE,{"disambiguationData":[TD([[makeQuery(id+"F4.imprint","IMPRINT",EDGE,{"derivedFrom":sQuery(id+"F4.wireOp",EDGE,"E38.MirrorC")}),-1.0]])]});
            var Q380;
            Q380=makeQuery(id+"F4.imprint","IMPRINT",FACE,{"disambiguationData":[TD([[makeQuery(id+"F4.imprint","IMPRINT",EDGE,{"derivedFrom":sQuery(id+"F4.wireOp",EDGE,"E6.0.11.21")}),1.0]])]});
            var Q381;
            Q381=makeQuery(id+"F4.imprint","IMPRINT",FACE,{"disambiguationData":[TD([[makeQuery(id+"F4.imprint","IMPRINT",EDGE,{"derivedFrom":sQuery(id+"F4.wireOp",EDGE,"E102.MirrorC")}),-1.0]])]});
            var Q382;
            Q382=makeQuery(id+"F4.imprint","IMPRINT",FACE,{"disambiguationData":[TD([[makeQuery(id+"F4.imprint","IMPRINT",EDGE,{"derivedFrom":sQuery(id+"F4.wireOp",EDGE,"E70.MirrorC")}),-1.0]])]});
            var Q383;
            Q383=makeQuery(id+"F4.imprint","IMPRINT",FACE,{"disambiguationData":[TD([[makeQuery(id+"F4.imprint","IMPRINT",EDGE,{"derivedFrom":sQuery(id+"F4.wireOp",EDGE,"E54.MirrorC")}),-1.0]])]});
            var Q384;
            Q384=makeQuery(id+"F4.imprint","IMPRINT",FACE,{"disambiguationData":[TD([[makeQuery(id+"F4.imprint","IMPRINT",EDGE,{"derivedFrom":sQuery(id+"F4.wireOp",EDGE,"E182.MirrorC")}),-1.0]])]});
            var Q385;
            Q385=makeQuery(id+"F4.imprint","IMPRINT",FACE,{"disambiguationData":[TD([[makeQuery(id+"F4.imprint","IMPRINT",EDGE,{"derivedFrom":sQuery(id+"F4.wireOp",EDGE,"E246.MirrorC")}),-1.0]])]});
            var Q386;
            Q386=makeQuery(id+"F4.imprint","IMPRINT",FACE,{"disambiguationData":[TD([[makeQuery(id+"F4.imprint","IMPRINT",EDGE,{"derivedFrom":sQuery(id+"F4.wireOp",EDGE,"E230.MirrorC")}),-1.0]])]});
            var Q387;
            Q387=makeQuery(id+"F4.imprint","IMPRINT",FACE,{"disambiguationData":[TD([[makeQuery(id+"F4.imprint","IMPRINT",EDGE,{"derivedFrom":sQuery(id+"F4.wireOp",EDGE,"E214.MirrorC")}),-1.0]])]});
            var Q388;
            Q388=makeQuery(id+"F4.imprint","IMPRINT",FACE,{"disambiguationData":[TD([[makeQuery(id+"F4.imprint","IMPRINT",EDGE,{"derivedFrom":sQuery(id+"F4.wireOp",EDGE,"E3.6.10.0")}),1.0]])]});
            var Q389;
            Q389=makeQuery(id+"F4.imprint","IMPRINT",FACE,{"disambiguationData":[TD([[makeQuery(id+"F4.imprint","IMPRINT",EDGE,{"derivedFrom":sQuery(id+"F4.wireOp",EDGE,"E3.5.12.0")}),1.0]])]});
            var Q390;
            Q390=makeQuery(id+"F4.imprint","IMPRINT",FACE,{"disambiguationData":[TD([[makeQuery(id+"F4.imprint","IMPRINT",EDGE,{"derivedFrom":sQuery(id+"F4.wireOp",EDGE,"E3.4.14.0")}),1.0]])]});
            var Q391;
            Q391=makeQuery(id+"F4.imprint","IMPRINT",FACE,{"disambiguationData":[TD([[makeQuery(id+"F4.imprint","IMPRINT",EDGE,{"derivedFrom":sQuery(id+"F4.wireOp",EDGE,"E3.3.16.0")}),1.0]])]});
            var Q392;
            Q392=makeQuery(id+"F4.imprint","IMPRINT",FACE,{"disambiguationData":[TD([[makeQuery(id+"F4.imprint","IMPRINT",EDGE,{"derivedFrom":sQuery(id+"F4.wireOp",EDGE,"E5.0.9.6")}),1.0]])]});
            var Q393;
            Q393=makeQuery(id+"F4.imprint","IMPRINT",FACE,{"disambiguationData":[TD([[makeQuery(id+"F4.imprint","IMPRINT",EDGE,{"derivedFrom":sQuery(id+"F4.wireOp",EDGE,"E5.0.8.8")}),1.0]])]});
            var Q394;
            Q394=makeQuery(id+"F4.imprint","IMPRINT",FACE,{"disambiguationData":[TD([[makeQuery(id+"F4.imprint","IMPRINT",EDGE,{"derivedFrom":sQuery(id+"F4.wireOp",EDGE,"E3.7.8.0")}),1.0]])]});
            var Q395;
            Q395=makeQuery(id+"F4.imprint","IMPRINT",FACE,{"disambiguationData":[TD([[makeQuery(id+"F4.imprint","IMPRINT",EDGE,{"derivedFrom":sQuery(id+"F4.wireOp",EDGE,"E6.0.4.18")}),1.0]])]});
            var Q396;
            Q396=makeQuery(id+"F4.imprint","IMPRINT",FACE,{"disambiguationData":[TD([[makeQuery(id+"F4.imprint","IMPRINT",EDGE,{"derivedFrom":sQuery(id+"F4.wireOp",EDGE,"E6.0.0.18")}),1.0]])]});
            var Q397;
            Q397=makeQuery(id+"F4.imprint","IMPRINT",FACE,{"disambiguationData":[TD([[makeQuery(id+"F4.imprint","IMPRINT",EDGE,{"derivedFrom":sQuery(id+"F4.wireOp",EDGE,"E5.0.11.2")}),1.0]])]});
            var Q398;
            Q398=makeQuery(id+"F4.imprint","IMPRINT",FACE,{"disambiguationData":[TD([[makeQuery(id+"F4.imprint","IMPRINT",EDGE,{"derivedFrom":sQuery(id+"F4.wireOp",EDGE,"E5.0.10.4")}),1.0]])]});
            var Q399;
            Q399=makeQuery(id+"F4.imprint","IMPRINT",FACE,{"disambiguationData":[TD([[makeQuery(id+"F4.imprint","IMPRINT",EDGE,{"derivedFrom":sQuery(id+"F4.wireOp",EDGE,"E39.MirrorC")}),-1.0]])]});
            var Q400;
            Q400=makeQuery(id+"F4.imprint","IMPRINT",FACE,{"disambiguationData":[TD([[makeQuery(id+"F4.imprint","IMPRINT",EDGE,{"derivedFrom":sQuery(id+"F4.wireOp",EDGE,"E6.0.8.18")}),1.0]])]});
            var Q401;
            Q401=makeQuery(id+"F4.imprint","IMPRINT",FACE,{"disambiguationData":[TD([[makeQuery(id+"F4.imprint","IMPRINT",EDGE,{"derivedFrom":sQuery(id+"F4.wireOp",EDGE,"E103.MirrorC")}),-1.0]])]});
            var Q402;
            Q402=makeQuery(id+"F4.imprint","IMPRINT",FACE,{"disambiguationData":[TD([[makeQuery(id+"F4.imprint","IMPRINT",EDGE,{"derivedFrom":sQuery(id+"F4.wireOp",EDGE,"E87.MirrorC")}),-1.0]])]});
            var Q403;
            Q403=makeQuery(id+"F4.imprint","IMPRINT",FACE,{"disambiguationData":[TD([[makeQuery(id+"F4.imprint","IMPRINT",EDGE,{"derivedFrom":sQuery(id+"F4.wireOp",EDGE,"E71.MirrorC")}),-1.0]])]});
            var Q404;
            Q404=makeQuery(id+"F4.imprint","IMPRINT",FACE,{"disambiguationData":[TD([[makeQuery(id+"F4.imprint","IMPRINT",EDGE,{"derivedFrom":sQuery(id+"F4.wireOp",EDGE,"E135.MirrorC")}),-1.0]])]});
            var Q405;
            Q405=makeQuery(id+"F4.imprint","IMPRINT",FACE,{"disambiguationData":[TD([[makeQuery(id+"F4.imprint","IMPRINT",EDGE,{"derivedFrom":sQuery(id+"F4.wireOp",EDGE,"E183.MirrorC")}),-1.0]])]});
            var Q406;
            Q406=makeQuery(id+"F4.imprint","IMPRINT",FACE,{"disambiguationData":[TD([[makeQuery(id+"F4.imprint","IMPRINT",EDGE,{"derivedFrom":sQuery(id+"F4.wireOp",EDGE,"E3.3.0.0")}),1.0]])]});
            var Q407;
            Q407=makeQuery(id+"F4.imprint","IMPRINT",FACE,{"disambiguationData":[TD([[makeQuery(id+"F4.imprint","IMPRINT",EDGE,{"derivedFrom":sQuery(id+"F4.wireOp",EDGE,"E3.2.2.0")}),1.0]])]});
            var Q408;
            Q408=makeQuery(id+"F4.imprint","IMPRINT",FACE,{"disambiguationData":[TD([[makeQuery(id+"F4.imprint","IMPRINT",EDGE,{"derivedFrom":sQuery(id+"F4.wireOp",EDGE,"E247.MirrorC")}),-1.0]])]});
            var Q409;
            Q409=makeQuery(id+"F4.imprint","IMPRINT",FACE,{"disambiguationData":[TD([[makeQuery(id+"F4.imprint","IMPRINT",EDGE,{"derivedFrom":sQuery(id+"F4.wireOp",EDGE,"E231.MirrorC")}),-1.0]])]});
            var Q410;
            Q410=makeQuery(id+"F4.imprint","IMPRINT",FACE,{"disambiguationData":[TD([[makeQuery(id+"F4.imprint","IMPRINT",EDGE,{"derivedFrom":sQuery(id+"F4.wireOp",EDGE,"E215.MirrorC")}),-1.0]])]});
            var Q411;
            Q411=makeQuery(id+"F4.imprint","IMPRINT",FACE,{"disambiguationData":[TD([[makeQuery(id+"F4.imprint","IMPRINT",EDGE,{"derivedFrom":sQuery(id+"F4.wireOp",EDGE,"E6.0.0.19")}),1.0]])]});
            var Q412;
            Q412=makeQuery(id+"F4.imprint","IMPRINT",FACE,{"disambiguationData":[TD([[makeQuery(id+"F4.imprint","IMPRINT",EDGE,{"derivedFrom":sQuery(id+"F4.wireOp",EDGE,"E5.0.11.3")}),1.0]])]});
            var Q413;
            Q413=makeQuery(id+"F4.imprint","IMPRINT",FACE,{"disambiguationData":[TD([[makeQuery(id+"F4.imprint","IMPRINT",EDGE,{"derivedFrom":sQuery(id+"F4.wireOp",EDGE,"E40.MirrorC")}),-1.0]])]});
            var Q414;
            Q414=makeQuery(id+"F4.imprint","IMPRINT",FACE,{"disambiguationData":[TD([[makeQuery(id+"F4.imprint","IMPRINT",EDGE,{"derivedFrom":sQuery(id+"F4.wireOp",EDGE,"E8.MirrorC")}),-1.0]])]});
            var Q415;
            Q415=makeQuery(id+"F4.imprint","IMPRINT",FACE,{"disambiguationData":[TD([[makeQuery(id+"F4.imprint","IMPRINT",EDGE,{"derivedFrom":sQuery(id+"F4.wireOp",EDGE,"E104.MirrorC")}),-1.0]])]});
            var Q416;
            Q416=makeQuery(id+"F4.imprint","IMPRINT",FACE,{"disambiguationData":[TD([[makeQuery(id+"F4.imprint","IMPRINT",EDGE,{"derivedFrom":sQuery(id+"F4.wireOp",EDGE,"E88.MirrorC")}),-1.0]])]});
            var Q417;
            Q417=makeQuery(id+"F4.imprint","IMPRINT",FACE,{"disambiguationData":[TD([[makeQuery(id+"F4.imprint","IMPRINT",EDGE,{"derivedFrom":sQuery(id+"F4.wireOp",EDGE,"E72.MirrorC")}),-1.0]])]});
            var Q418;
            Q418=makeQuery(id+"F4.imprint","IMPRINT",FACE,{"disambiguationData":[TD([[makeQuery(id+"F4.imprint","IMPRINT",EDGE,{"derivedFrom":sQuery(id+"F4.wireOp",EDGE,"E120.MirrorC")}),-1.0]])]});
            var Q419;
            Q419=makeQuery(id+"F4.imprint","IMPRINT",FACE,{"disambiguationData":[TD([[makeQuery(id+"F4.imprint","IMPRINT",EDGE,{"derivedFrom":sQuery(id+"F4.wireOp",EDGE,"E184.MirrorC")}),-1.0]])]});
            var Q420;
            Q420=makeQuery(id+"F4.imprint","IMPRINT",FACE,{"disambiguationData":[TD([[makeQuery(id+"F4.imprint","IMPRINT",EDGE,{"derivedFrom":sQuery(id+"F4.wireOp",EDGE,"E248.MirrorC")}),-1.0]])]});
            var Q421;
            Q421=makeQuery(id+"F4.imprint","IMPRINT",FACE,{"disambiguationData":[TD([[makeQuery(id+"F4.imprint","IMPRINT",EDGE,{"derivedFrom":sQuery(id+"F4.wireOp",EDGE,"E232.MirrorC")}),-1.0]])]});
            var Q422;
            Q422=makeQuery(id+"F4.imprint","IMPRINT",FACE,{"disambiguationData":[TD([[makeQuery(id+"F4.imprint","IMPRINT",EDGE,{"derivedFrom":sQuery(id+"F4.wireOp",EDGE,"E216.MirrorC")}),-1.0]])]});
            var Q423;
            Q423=makeQuery(id+"F4.imprint","IMPRINT",FACE,{"disambiguationData":[TD([[makeQuery(id+"F4.imprint","IMPRINT",EDGE,{"derivedFrom":sQuery(id+"F4.wireOp",EDGE,"E3.6.11.0")}),1.0]])]});
            var Q424;
            Q424=makeQuery(id+"F4.imprint","IMPRINT",FACE,{"disambiguationData":[TD([[makeQuery(id+"F4.imprint","IMPRINT",EDGE,{"derivedFrom":sQuery(id+"F4.wireOp",EDGE,"E6.0.4.20")}),1.0]])]});
            var Q425;
            Q425=makeQuery(id+"F4.imprint","IMPRINT",FACE,{"disambiguationData":[TD([[makeQuery(id+"F4.imprint","IMPRINT",EDGE,{"derivedFrom":sQuery(id+"F4.wireOp",EDGE,"E6.0.0.20")}),1.0]])]});
            var Q426;
            Q426=makeQuery(id+"F4.imprint","IMPRINT",FACE,{"disambiguationData":[TD([[makeQuery(id+"F4.imprint","IMPRINT",EDGE,{"derivedFrom":sQuery(id+"F4.wireOp",EDGE,"E5.0.11.4")}),1.0]])]});
            var Q427;
            Q427=makeQuery(id+"F4.imprint","IMPRINT",FACE,{"disambiguationData":[TD([[makeQuery(id+"F4.imprint","IMPRINT",EDGE,{"derivedFrom":sQuery(id+"F4.wireOp",EDGE,"E5.0.10.6")}),1.0]])]});
            var Q428;
            Q428=makeQuery(id+"F4.imprint","IMPRINT",FACE,{"disambiguationData":[TD([[makeQuery(id+"F4.imprint","IMPRINT",EDGE,{"derivedFrom":sQuery(id+"F4.wireOp",EDGE,"E41.MirrorC")}),-1.0]])]});
            var Q429;
            Q429=makeQuery(id+"F4.imprint","IMPRINT",FACE,{"disambiguationData":[TD([[makeQuery(id+"F4.imprint","IMPRINT",EDGE,{"derivedFrom":sQuery(id+"F4.wireOp",EDGE,"E25.MirrorC")}),-1.0]])]});
            var Q430;
            Q430=makeQuery(id+"F4.imprint","IMPRINT",FACE,{"disambiguationData":[TD([[makeQuery(id+"F4.imprint","IMPRINT",EDGE,{"derivedFrom":sQuery(id+"F4.wireOp",EDGE,"E9.MirrorC")}),-1.0]])]});
            var Q431;
            Q431=makeQuery(id+"F4.imprint","IMPRINT",FACE,{"disambiguationData":[TD([[makeQuery(id+"F4.imprint","IMPRINT",EDGE,{"derivedFrom":sQuery(id+"F4.wireOp",EDGE,"E6.0.8.20")}),1.0]])]});
            var Q432;
            Q432=makeQuery(id+"F4.imprint","IMPRINT",FACE,{"disambiguationData":[TD([[makeQuery(id+"F4.imprint","IMPRINT",EDGE,{"derivedFrom":sQuery(id+"F4.wireOp",EDGE,"E105.MirrorC")}),-1.0]])]});
            var Q433;
            Q433=makeQuery(id+"F4.imprint","IMPRINT",FACE,{"disambiguationData":[TD([[makeQuery(id+"F4.imprint","IMPRINT",EDGE,{"derivedFrom":sQuery(id+"F4.wireOp",EDGE,"E73.MirrorC")}),-1.0]])]});
            var Q434;
            Q434=makeQuery(id+"F4.imprint","IMPRINT",FACE,{"disambiguationData":[TD([[makeQuery(id+"F4.imprint","IMPRINT",EDGE,{"derivedFrom":sQuery(id+"F4.wireOp",EDGE,"E137.MirrorC")}),-1.0]])]});
            var Q435;
            Q435=makeQuery(id+"F4.imprint","IMPRINT",FACE,{"disambiguationData":[TD([[makeQuery(id+"F4.imprint","IMPRINT",EDGE,{"derivedFrom":sQuery(id+"F4.wireOp",EDGE,"E185.MirrorC")}),-1.0]])]});
            var Q436;
            Q436=makeQuery(id+"F4.imprint","IMPRINT",FACE,{"disambiguationData":[TD([[makeQuery(id+"F4.imprint","IMPRINT",EDGE,{"derivedFrom":sQuery(id+"F4.wireOp",EDGE,"E217.MirrorC")}),-1.0]])]});
            var Q437;
            Q437=makeQuery(id+"F4.imprint","IMPRINT",FACE,{"disambiguationData":[TD([[makeQuery(id+"F4.imprint","IMPRINT",EDGE,{"derivedFrom":sQuery(id+"F4.wireOp",EDGE,"E3.3.2.0")}),1.0]])]});
            var Q438;
            Q438=makeQuery(id+"F4.imprint","IMPRINT",FACE,{"disambiguationData":[TD([[makeQuery(id+"F4.imprint","IMPRINT",EDGE,{"derivedFrom":sQuery(id+"F4.wireOp",EDGE,"E3.2.4.0")}),1.0]])]});
            var Q439;
            Q439=makeQuery(id+"F4.imprint","IMPRINT",FACE,{"disambiguationData":[TD([[makeQuery(id+"F4.imprint","IMPRINT",EDGE,{"derivedFrom":sQuery(id+"F4.wireOp",EDGE,"E3.6.12.0")}),1.0]])]});
            var Q440;
            Q440=makeQuery(id+"F4.imprint","IMPRINT",FACE,{"disambiguationData":[TD([[makeQuery(id+"F4.imprint","IMPRINT",EDGE,{"derivedFrom":sQuery(id+"F4.wireOp",EDGE,"E3.5.14.0")}),1.0]])]});
            var Q441;
            Q441=makeQuery(id+"F4.imprint","IMPRINT",FACE,{"disambiguationData":[TD([[makeQuery(id+"F4.imprint","IMPRINT",EDGE,{"derivedFrom":sQuery(id+"F4.wireOp",EDGE,"E3.4.16.0")}),1.0]])]});
            var Q442;
            Q442=makeQuery(id+"F4.imprint","IMPRINT",FACE,{"disambiguationData":[TD([[makeQuery(id+"F4.imprint","IMPRINT",EDGE,{"derivedFrom":sQuery(id+"F4.wireOp",EDGE,"E3.4.0.0")}),1.0]])]});
            var Q443;
            Q443=makeQuery(id+"F4.imprint","IMPRINT",FACE,{"disambiguationData":[TD([[makeQuery(id+"F4.imprint","IMPRINT",EDGE,{"derivedFrom":sQuery(id+"F4.wireOp",EDGE,"E5.0.9.8")}),1.0]])]});
            var Q444;
            Q444=makeQuery(id+"F4.imprint","IMPRINT",FACE,{"disambiguationData":[TD([[makeQuery(id+"F4.imprint","IMPRINT",EDGE,{"derivedFrom":sQuery(id+"F4.wireOp",EDGE,"E5.0.8.10")}),1.0]])]});
            var Q445;
            Q445=makeQuery(id+"F4.imprint","IMPRINT",FACE,{"disambiguationData":[TD([[makeQuery(id+"F4.imprint","IMPRINT",EDGE,{"derivedFrom":sQuery(id+"F4.wireOp",EDGE,"E3.7.10.0")}),1.0]])]});
            var Q446;
            Q446=makeQuery(id+"F4.imprint","IMPRINT",FACE,{"disambiguationData":[TD([[makeQuery(id+"F4.imprint","IMPRINT",EDGE,{"derivedFrom":sQuery(id+"F4.wireOp",EDGE,"E42.MirrorC")}),-1.0]])]});
            var Q447;
            Q447=makeQuery(id+"F4.imprint","IMPRINT",FACE,{"disambiguationData":[TD([[makeQuery(id+"F4.imprint","IMPRINT",EDGE,{"derivedFrom":sQuery(id+"F4.wireOp",EDGE,"E10.MirrorC")}),-1.0]])]});
            var Q448;
            Q448=makeQuery(id+"F4.imprint","IMPRINT",FACE,{"disambiguationData":[TD([[makeQuery(id+"F4.imprint","IMPRINT",EDGE,{"derivedFrom":sQuery(id+"F4.wireOp",EDGE,"E106.MirrorC")}),-1.0]])]});
            var Q449;
            Q449=makeQuery(id+"F4.imprint","IMPRINT",FACE,{"disambiguationData":[TD([[makeQuery(id+"F4.imprint","IMPRINT",EDGE,{"derivedFrom":sQuery(id+"F4.wireOp",EDGE,"E74.MirrorC")}),-1.0]])]});
            var Q450;
            Q450=makeQuery(id+"F4.imprint","IMPRINT",FACE,{"disambiguationData":[TD([[makeQuery(id+"F4.imprint","IMPRINT",EDGE,{"derivedFrom":sQuery(id+"F4.wireOp",EDGE,"E138.MirrorC")}),-1.0]])]});
            var Q451;
            Q451=makeQuery(id+"F4.imprint","IMPRINT",FACE,{"disambiguationData":[TD([[makeQuery(id+"F4.imprint","IMPRINT",EDGE,{"derivedFrom":sQuery(id+"F4.wireOp",EDGE,"E202.MirrorC")}),-1.0]])]});
            var Q452;
            Q452=makeQuery(id+"F4.imprint","IMPRINT",FACE,{"disambiguationData":[TD([[makeQuery(id+"F4.imprint","IMPRINT",EDGE,{"derivedFrom":sQuery(id+"F4.wireOp",EDGE,"E186.MirrorC")}),-1.0]])]});
            var Q453;
            Q453=makeQuery(id+"F4.imprint","IMPRINT",FACE,{"disambiguationData":[TD([[makeQuery(id+"F4.imprint","IMPRINT",EDGE,{"derivedFrom":sQuery(id+"F4.wireOp",EDGE,"E170.MirrorC")}),-1.0]])]});
            var Q454;
            Q454=makeQuery(id+"F4.imprint","IMPRINT",FACE,{"disambiguationData":[TD([[makeQuery(id+"F4.imprint","IMPRINT",EDGE,{"derivedFrom":sQuery(id+"F4.wireOp",EDGE,"E218.MirrorC")}),-1.0]])]});
            var Q455;
            Q455=makeQuery(id+"F4.imprint","IMPRINT",FACE,{"disambiguationData":[TD([[makeQuery(id+"F4.imprint","IMPRINT",EDGE,{"derivedFrom":sQuery(id+"F4.wireOp",EDGE,"E3.6.13.0")}),1.0]])]});
            var Q456;
            Q456=makeQuery(id+"F4.imprint","IMPRINT",FACE,{"disambiguationData":[TD([[makeQuery(id+"F4.imprint","IMPRINT",EDGE,{"derivedFrom":sQuery(id+"F4.wireOp",EDGE,"E6.0.0.21")}),1.0]])]});
            var Q457;
            Q457=makeQuery(id+"F4.imprint","IMPRINT",FACE,{"disambiguationData":[TD([[makeQuery(id+"F4.imprint","IMPRINT",EDGE,{"derivedFrom":sQuery(id+"F4.wireOp",EDGE,"E5.0.11.5")}),1.0]])]});
            var Q458;
            Q458=makeQuery(id+"F4.imprint","IMPRINT",FACE,{"disambiguationData":[TD([[makeQuery(id+"F4.imprint","IMPRINT",EDGE,{"derivedFrom":sQuery(id+"F4.wireOp",EDGE,"E107.MirrorC")}),-1.0]])]});
            var Q459;
            Q459=makeQuery(id+"F4.imprint","IMPRINT",FACE,{"disambiguationData":[TD([[makeQuery(id+"F4.imprint","IMPRINT",EDGE,{"derivedFrom":sQuery(id+"F4.wireOp",EDGE,"E91.MirrorC")}),-1.0]])]});
            var Q460;
            Q460=makeQuery(id+"F4.imprint","IMPRINT",FACE,{"disambiguationData":[TD([[makeQuery(id+"F4.imprint","IMPRINT",EDGE,{"derivedFrom":sQuery(id+"F4.wireOp",EDGE,"E75.MirrorC")}),-1.0]])]});
            var Q461;
            Q461=makeQuery(id+"F4.imprint","IMPRINT",FACE,{"disambiguationData":[TD([[makeQuery(id+"F4.imprint","IMPRINT",EDGE,{"derivedFrom":sQuery(id+"F4.wireOp",EDGE,"E139.MirrorC")}),-1.0]])]});
            var Q462;
            Q462=makeQuery(id+"F4.imprint","IMPRINT",FACE,{"disambiguationData":[TD([[makeQuery(id+"F4.imprint","IMPRINT",EDGE,{"derivedFrom":sQuery(id+"F4.wireOp",EDGE,"E187.MirrorC")}),-1.0]])]});
            var Q463;
            Q463=makeQuery(id+"F4.imprint","IMPRINT",FACE,{"disambiguationData":[TD([[makeQuery(id+"F4.imprint","IMPRINT",EDGE,{"derivedFrom":sQuery(id+"F4.wireOp",EDGE,"E219.MirrorC")}),-1.0]])]});
            var Q464;
            Q464=makeQuery(id+"F4.imprint","IMPRINT",FACE,{"disambiguationData":[TD([[makeQuery(id+"F4.imprint","IMPRINT",EDGE,{"derivedFrom":sQuery(id+"F4.wireOp",EDGE,"E3.3.4.0")}),1.0]])]});
            var Q465;
            Q465=makeQuery(id+"F4.imprint","IMPRINT",FACE,{"disambiguationData":[TD([[makeQuery(id+"F4.imprint","IMPRINT",EDGE,{"derivedFrom":sQuery(id+"F4.wireOp",EDGE,"E3.2.6.0")}),1.0]])]});
            var Q466;
            Q466=makeQuery(id+"F4.imprint","IMPRINT",FACE,{"disambiguationData":[TD([[makeQuery(id+"F4.imprint","IMPRINT",EDGE,{"derivedFrom":sQuery(id+"F4.wireOp",EDGE,"E3.6.14.0")}),1.0]])]});
            var Q467;
            Q467=makeQuery(id+"F4.imprint","IMPRINT",FACE,{"disambiguationData":[TD([[makeQuery(id+"F4.imprint","IMPRINT",EDGE,{"derivedFrom":sQuery(id+"F4.wireOp",EDGE,"E3.5.16.0")}),1.0]])]});
            var Q468;
            Q468=makeQuery(id+"F4.imprint","IMPRINT",FACE,{"disambiguationData":[TD([[makeQuery(id+"F4.imprint","IMPRINT",EDGE,{"derivedFrom":sQuery(id+"F4.wireOp",EDGE,"E3.5.0.0")}),1.0]])]});
            var Q469;
            Q469=makeQuery(id+"F4.imprint","IMPRINT",FACE,{"disambiguationData":[TD([[makeQuery(id+"F4.imprint","IMPRINT",EDGE,{"derivedFrom":sQuery(id+"F4.wireOp",EDGE,"E3.4.2.0")}),1.0]])]});
            var Q470;
            Q470=makeQuery(id+"F4.imprint","IMPRINT",FACE,{"disambiguationData":[TD([[makeQuery(id+"F4.imprint","IMPRINT",EDGE,{"derivedFrom":sQuery(id+"F4.wireOp",EDGE,"E5.0.9.10")}),1.0]])]});
            var Q471;
            Q471=makeQuery(id+"F4.imprint","IMPRINT",FACE,{"disambiguationData":[TD([[makeQuery(id+"F4.imprint","IMPRINT",EDGE,{"derivedFrom":sQuery(id+"F4.wireOp",EDGE,"E5.0.8.12")}),1.0]])]});
            var Q472;
            Q472=makeQuery(id+"F4.imprint","IMPRINT",FACE,{"disambiguationData":[TD([[makeQuery(id+"F4.imprint","IMPRINT",EDGE,{"derivedFrom":sQuery(id+"F4.wireOp",EDGE,"E3.7.12.0")}),1.0]])]});
            var Q473;
            Q473=makeQuery(id+"F4.imprint","IMPRINT",FACE,{"disambiguationData":[TD([[makeQuery(id+"F4.imprint","IMPRINT",EDGE,{"derivedFrom":sQuery(id+"F4.wireOp",EDGE,"E6.0.5.18")}),1.0]])]});
            var Q474;
            Q474=makeQuery(id+"F4.imprint","IMPRINT",FACE,{"disambiguationData":[TD([[makeQuery(id+"F4.imprint","IMPRINT",EDGE,{"derivedFrom":sQuery(id+"F4.wireOp",EDGE,"E6.0.1.18")}),1.0]])]});
            var Q475;
            Q475=makeQuery(id+"F4.imprint","IMPRINT",FACE,{"disambiguationData":[TD([[makeQuery(id+"F4.imprint","IMPRINT",EDGE,{"derivedFrom":sQuery(id+"F4.wireOp",EDGE,"E5.0.11.6")}),1.0]])]});
            var Q476;
            Q476=makeQuery(id+"F4.imprint","IMPRINT",FACE,{"disambiguationData":[TD([[makeQuery(id+"F4.imprint","IMPRINT",EDGE,{"derivedFrom":sQuery(id+"F4.wireOp",EDGE,"E5.0.10.8")}),1.0]])]});
            var Q477;
            Q477=makeQuery(id+"F4.imprint","IMPRINT",FACE,{"disambiguationData":[TD([[makeQuery(id+"F4.imprint","IMPRINT",EDGE,{"derivedFrom":sQuery(id+"F4.wireOp",EDGE,"E43.MirrorC")}),-1.0]])]});
            var Q478;
            Q478=makeQuery(id+"F4.imprint","IMPRINT",FACE,{"disambiguationData":[TD([[makeQuery(id+"F4.imprint","IMPRINT",EDGE,{"derivedFrom":sQuery(id+"F4.wireOp",EDGE,"E27.MirrorC")}),-1.0]])]});
            var Q479;
            Q479=makeQuery(id+"F4.imprint","IMPRINT",FACE,{"disambiguationData":[TD([[makeQuery(id+"F4.imprint","IMPRINT",EDGE,{"derivedFrom":sQuery(id+"F4.wireOp",EDGE,"E11.MirrorC")}),-1.0]])]});
            var Q480;
            Q480=makeQuery(id+"F4.imprint","IMPRINT",FACE,{"disambiguationData":[TD([[makeQuery(id+"F4.imprint","IMPRINT",EDGE,{"derivedFrom":sQuery(id+"F4.wireOp",EDGE,"E6.0.9.18")}),1.0]])]});
            var Q481;
            Q481=makeQuery(id+"F4.imprint","IMPRINT",FACE,{"disambiguationData":[TD([[makeQuery(id+"F4.imprint","IMPRINT",EDGE,{"derivedFrom":sQuery(id+"F4.wireOp",EDGE,"E3.1.10.0")}),1.0]])]});
            var Q482;
            Q482=makeQuery(id+"F4.imprint","IMPRINT",FACE,{"disambiguationData":[TD([[makeQuery(id+"F4.imprint","IMPRINT",EDGE,{"derivedFrom":sQuery(id+"F4.wireOp",EDGE,"E3.0.2.0")}),1.0]])]});
            var Q483;
            Q483=makeQuery(id+"F4.imprint","IMPRINT",FACE,{"disambiguationData":[TD([[makeQuery(id+"F4.imprint","IMPRINT",EDGE,{"derivedFrom":sQuery(id+"F4.wireOp",EDGE,"E3.0.3.0")}),1.0]])]});
            var Q484;
            Q484=makeQuery(id+"F4.imprint","IMPRINT",FACE,{"disambiguationData":[TD([[makeQuery(id+"F4.imprint","IMPRINT",EDGE,{"derivedFrom":sQuery(id+"F4.wireOp",EDGE,"E3.1.2.0")}),1.0]])]});
            var Q485;
            Q485=makeQuery(id+"F4.imprint","IMPRINT",FACE,{"disambiguationData":[TD([[makeQuery(id+"F4.imprint","IMPRINT",EDGE,{"derivedFrom":sQuery(id+"F4.wireOp",EDGE,"E3.1.4.0")}),1.0]])]});
            var Q486;
            Q486=makeQuery(id+"F4.imprint","IMPRINT",FACE,{"disambiguationData":[TD([[makeQuery(id+"F4.imprint","IMPRINT",EDGE,{"derivedFrom":sQuery(id+"F4.wireOp",EDGE,"E3.1.6.0")}),1.0]])]});
            var Q487;
            Q487=makeQuery(id+"F4.imprint","IMPRINT",FACE,{"disambiguationData":[TD([[makeQuery(id+"F4.imprint","IMPRINT",EDGE,{"derivedFrom":sQuery(id+"F4.wireOp",EDGE,"E3.1.8.0")}),1.0]])]});
            var Q488;
            Q488=makeQuery(id+"F4.imprint","IMPRINT",FACE,{"disambiguationData":[TD([[makeQuery(id+"F4.imprint","IMPRINT",EDGE,{"derivedFrom":sQuery(id+"F4.wireOp",EDGE,"E7.MirrorC")}),-1.0]])]});
            var Q489;
            Q489=makeQuery(id+"F4.imprint","IMPRINT",FACE,{"disambiguationData":[TD([[makeQuery(id+"F4.imprint","IMPRINT",EDGE,{"derivedFrom":sQuery(id+"F4.wireOp",EDGE,"E3.0.1.0")}),1.0]])]});
            var Q490;
            Q490=makeQuery(id+"F4.imprint","IMPRINT",FACE,{"disambiguationData":[TD([[makeQuery(id+"F4.imprint","IMPRINT",EDGE,{"derivedFrom":sQuery(id+"F4.wireOp",EDGE,"E3.1.0.0")}),1.0]])]});
            var Q491;
            Q491=makeQuery(id+"F4.imprint","IMPRINT",FACE,{"disambiguationData":[TD([[makeQuery(id+"F4.imprint","IMPRINT",EDGE,{"derivedFrom":sQuery(id+"F4.wireOp",EDGE,"E3.0.15.0")}),-1.0]])]});
            var Q492;
            Q492=makeQuery(id+"F4.imprint","IMPRINT",FACE,{"disambiguationData":[TD([[makeQuery(id+"F4.imprint","IMPRINT",EDGE,{"derivedFrom":sQuery(id+"F4.wireOp",EDGE,"E3.0.14.0")}),-1.0]])]});
            var Q493;
            Q493=makeQuery(id+"F4.imprint","IMPRINT",FACE,{"disambiguationData":[TD([[makeQuery(id+"F4.imprint","IMPRINT",EDGE,{"derivedFrom":sQuery(id+"F4.wireOp",EDGE,"E3.0.13.0")}),-1.0]])]});
            var Q494;
            Q494=makeQuery(id+"F4.imprint","IMPRINT",FACE,{"disambiguationData":[TD([[makeQuery(id+"F4.imprint","IMPRINT",EDGE,{"derivedFrom":sQuery(id+"F4.wireOp",EDGE,"E3.0.12.0")}),-1.0]])]});
            var Q495;
            Q495=makeQuery(id+"F4.imprint","IMPRINT",FACE,{"disambiguationData":[TD([[makeQuery(id+"F4.imprint","IMPRINT",EDGE,{"derivedFrom":sQuery(id+"F4.wireOp",EDGE,"E3.0.11.0")}),-1.0]])]});
            var Q496;
            Q496=makeQuery(id+"F4.imprint","IMPRINT",FACE,{"disambiguationData":[TD([[makeQuery(id+"F4.imprint","IMPRINT",EDGE,{"derivedFrom":sQuery(id+"F4.wireOp",EDGE,"E3.0.10.0")}),-1.0]])]});
            var Q497;
            Q497=makeQuery(id+"F4.imprint","IMPRINT",FACE,{"disambiguationData":[TD([[makeQuery(id+"F4.imprint","IMPRINT",EDGE,{"derivedFrom":sQuery(id+"F4.wireOp",EDGE,"E3.0.9.0")}),-1.0]])]});
            var Q498;
            Q498=makeQuery(id+"F4.imprint","IMPRINT",FACE,{"disambiguationData":[TD([[makeQuery(id+"F4.imprint","IMPRINT",EDGE,{"derivedFrom":sQuery(id+"F4.wireOp",EDGE,"E3.0.8.0")}),-1.0]])]});
            var Q499;
            Q499=makeQuery(id+"F4.imprint","IMPRINT",FACE,{"disambiguationData":[TD([[makeQuery(id+"F4.imprint","IMPRINT",EDGE,{"derivedFrom":sQuery(id+"F4.wireOp",EDGE,"E3.0.7.0")}),-1.0]])]});
            var Q500;
            Q500=makeQuery(id+"F4.imprint","IMPRINT",FACE,{"disambiguationData":[TD([[makeQuery(id+"F4.imprint","IMPRINT",EDGE,{"derivedFrom":sQuery(id+"F4.wireOp",EDGE,"E3.0.6.0")}),-1.0]])]});
            var Q501;
            Q501=makeQuery(id+"F4.imprint","IMPRINT",FACE,{"disambiguationData":[TD([[makeQuery(id+"F4.imprint","IMPRINT",EDGE,{"derivedFrom":sQuery(id+"F4.wireOp",EDGE,"E3.0.5.0")}),-1.0]])]});
            var Q502;
            Q502=makeQuery(id+"F4.imprint","IMPRINT",FACE,{"disambiguationData":[TD([[makeQuery(id+"F4.imprint","IMPRINT",EDGE,{"derivedFrom":sQuery(id+"F4.wireOp",EDGE,"E3.0.16.0")}),-1.0]])]});
            var Q503;
            Q503=makeQuery(id+"F4.imprint","IMPRINT",FACE,{"disambiguationData":[TD([[makeQuery(id+"F4.imprint","IMPRINT",EDGE,{"derivedFrom":sQuery(id+"F4.wireOp",EDGE,"E3.0.17.0")}),-1.0]])]});
            var Q504;
            Q504=makeQuery(id+"F4.imprint","IMPRINT",FACE,{"disambiguationData":[TD([[makeQuery(id+"F4.imprint","IMPRINT",EDGE,{"derivedFrom":sQuery(id+"F4.wireOp",EDGE,"E3.0.4.0")}),-1.0]])]});
            var Q505;
            Q505=makeQuery(id+"F4.imprint","IMPRINT",FACE,{"disambiguationData":[TD([[makeQuery(id+"F4.imprint","IMPRINT",EDGE,{"derivedFrom":sQuery(id+"F4.wireOp",EDGE,"E2")}),1.0]])]});
            extrude(context, id + "F5", {"entities" : qUnion([Q0, Q1, Q2, Q3, Q4, Q5, Q6, Q7, Q8, Q9, Q10, Q11, Q12, Q13, Q14, Q15, Q16, Q17, Q18, Q19, Q20, Q21, Q22, Q23, Q24, Q25, Q26, Q27, Q28, Q29, Q30, Q31, Q32, Q33, Q34, Q35, Q36, Q37, Q38, Q39, Q40, Q41, Q42, Q43, Q44, Q45, Q46, Q47, Q48, Q49, Q50, Q51, Q52, Q53, Q54, Q55, Q56, Q57, Q58, Q59, Q60, Q61, Q62, Q63, Q64, Q65, Q66, Q67, Q68, Q69, Q70, Q71, Q72, Q73, Q74, Q75, Q76, Q77, Q78, Q79, Q80, Q81, Q82, Q83, Q84, Q85, Q86, Q87, Q88, Q89, Q90, Q91, Q92, Q93, Q94, Q95, Q96, Q97, Q98, Q99, Q100, Q101, Q102, Q103, Q104, Q105, Q106, Q107, Q108, Q109, Q110, Q111, Q112, Q113, Q114, Q115, Q116, Q117, Q118, Q119, Q120, Q121, Q122, Q123, Q124, Q125, Q126, Q127, Q128, Q129, Q130, Q131, Q132, Q133, Q134, Q135, Q136, Q137, Q138, Q139, Q140, Q141, Q142, Q143, Q144, Q145, Q146, Q147, Q148, Q149, Q150, Q151, Q152, Q153, Q154, Q155, Q156, Q157, Q158, Q159, Q160, Q161, Q162, Q163, Q164, Q165, Q166, Q167, Q168, Q169, Q170, Q171, Q172, Q173, Q174, Q175, Q176, Q177, Q178, Q179, Q180, Q181, Q182, Q183, Q184, Q185, Q186, Q187, Q188, Q189, Q190, Q191, Q192, Q193, Q194, Q195, Q196, Q197, Q198, Q199, Q200, Q201, Q202, Q203, Q204, Q205, Q206, Q207, Q208, Q209, Q210, Q211, Q212, Q213, Q214, Q215, Q216, Q217, Q218, Q219, Q220, Q221, Q222, Q223, Q224, Q225, Q226, Q227, Q228, Q229, Q230, Q231, Q232, Q233, Q234, Q235, Q236, Q237, Q238, Q239, Q240, Q241, Q242, Q243, Q244, Q245, Q246, Q247, Q248, Q249, Q250, Q251, Q252, Q253, Q254, Q255, Q256, Q257, Q258, Q259, Q260, Q261, Q262, Q263, Q264, Q265, Q266, Q267, Q268, Q269, Q270, Q271, Q272, Q273, Q274, Q275, Q276, Q277, Q278, Q279, Q280, Q281, Q282, Q283, Q284, Q285, Q286, Q287, Q288, Q289, Q290, Q291, Q292, Q293, Q294, Q295, Q296, Q297, Q298, Q299, Q300, Q301, Q302, Q303, Q304, Q305, Q306, Q307, Q308, Q309, Q310, Q311, Q312, Q313, Q314, Q315, Q316, Q317, Q318, Q319, Q320, Q321, Q322, Q323, Q324, Q325, Q326, Q327, Q328, Q329, Q330, Q331, Q332, Q333, Q334, Q335, Q336, Q337, Q338, Q339, Q340, Q341, Q342, Q343, Q344, Q345, Q346, Q347, Q348, Q349, Q350, Q351, Q352, Q353, Q354, Q355, Q356, Q357, Q358, Q359, Q360, Q361, Q362, Q363, Q364, Q365, Q366, Q367, Q368, Q369, Q370, Q371, Q372, Q373, Q374, Q375, Q376, Q377, Q378, Q379, Q380, Q381, Q382, Q383, Q384, Q385, Q386, Q387, Q388, Q389, Q390, Q391, Q392, Q393, Q394, Q395, Q396, Q397, Q398, Q399, Q400, Q401, Q402, Q403, Q404, Q405, Q406, Q407, Q408, Q409, Q410, Q411, Q412, Q413, Q414, Q415, Q416, Q417, Q418, Q419, Q420, Q421, Q422, Q423, Q424, Q425, Q426, Q427, Q428, Q429, Q430, Q431, Q432, Q433, Q434, Q435, Q436, Q437, Q438, Q439, Q440, Q441, Q442, Q443, Q444, Q445, Q446, Q447, Q448, Q449, Q450, Q451, Q452, Q453, Q454, Q455, Q456, Q457, Q458, Q459, Q460, Q461, Q462, Q463, Q464, Q465, Q466, Q467, Q468, Q469, Q470, Q471, Q472, Q473, Q474, Q475, Q476, Q477, Q478, Q479, Q480, Q481, Q482, Q483, Q484, Q485, Q486, Q487, Q488, Q489, Q490, Q491, Q492, Q493, Q494, Q495, Q496, Q497, Q498, Q499, Q500, Q501, Q502, Q503, Q504, Q505]), "operationType" : NewBodyOperationType.REMOVE, "endBound" : BoundingType.THROUGH_ALL, "oppositeDirection" : true, "depth" : 25.4 * mm});
        }
    });
